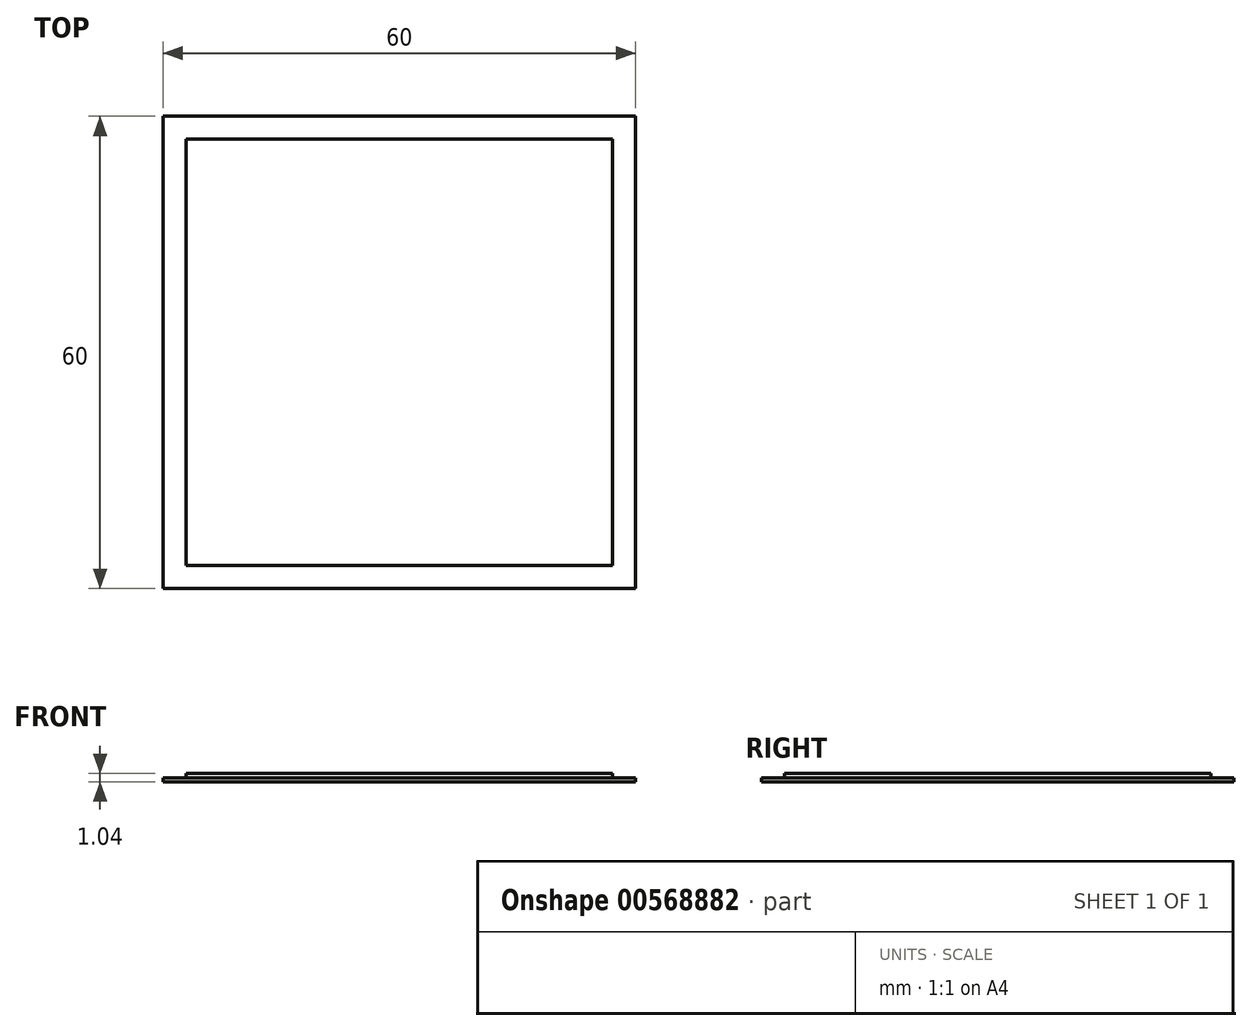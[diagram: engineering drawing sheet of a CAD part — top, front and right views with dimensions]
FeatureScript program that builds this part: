
annotation { "Feature Type Name" : "Feature", "Feature Type Description" : "" }
export const myFeature = defineFeature(function(context is Context, id is Id, definition is map)
    precondition{}
    {
        {
            var Q0;
            Q0=qCreatedBy(makeId("Top.planeOp"),FACE);
            var sketch = newSketch(context, id + "F0", { "sketchPlane" : qUnion([Q0])});
            skLineSegment(sketch, "E0.bottom", {"start": v(3, -3) * mm, "end": v(-3, -3) * mm});
            skLineSegment(sketch, "E0.top", {"start": v(3, 3) * mm, "end": v(-3, 3) * mm});
            skLineSegment(sketch, "E0.left", {"start": v(3, -3) * mm, "end": v(3, 3) * mm});
            skLineSegment(sketch, "E0.right", {"start": v(-3, -3) * mm, "end": v(-3, 3) * mm});
            skSolve(sketch);
        }
        {
            var Q0;
            Q0 = qSketchRegion(id + "F0", true);
            var Q1;
            Q1=makeQuery(id+"F0.imprint","IMPRINT",FACE,{"disambiguationData":[TD([[makeQuery(id+"F0.imprint","IMPRINT",EDGE,{"derivedFrom":sQuery(id+"F0.wireOp",EDGE,"3195768e-dd08-421b-a517-f94ed740182d")}),1.0]])]});
            var Q2;
            Q2=makeQuery(id+"F0.imprint","IMPRINT",FACE,{"disambiguationData":[TD([[makeQuery(id+"F0.imprint","IMPRINT",EDGE,{"derivedFrom":sQuery(id+"F0.wireOp",EDGE,"99365f39-84bf-4d14-bde5-4bdda7643e0d")}),1.0]])]});
            var Q3;
            Q3=makeQuery(id+"F0.imprint","IMPRINT",FACE,{"disambiguationData":[TD([[makeQuery(id+"F0.imprint","IMPRINT",EDGE,{"derivedFrom":sQuery(id+"F0.wireOp",EDGE,"a9b0deac-9651-4806-95d7-b4778e970440")}),1.0]])]});
            var Q4;
            Q4=makeQuery(id+"F0.imprint","IMPRINT",FACE,{"disambiguationData":[TD([[makeQuery(id+"F0.imprint","IMPRINT",EDGE,{"derivedFrom":sQuery(id+"F0.wireOp",EDGE,"e3f9c86c-c5da-4ea8-b7f3-f17e3de16e99")}),1.0]])]});
            var Q5;
            Q5=makeQuery(id+"F0.imprint","IMPRINT",FACE,{"disambiguationData":[TD([[makeQuery(id+"F0.imprint","IMPRINT",EDGE,{"derivedFrom":sQuery(id+"F0.wireOp",EDGE,"0799e189-6896-4580-8602-fb586a51e5e5")}),1.0]])]});
            var Q6;
            Q6=makeQuery(id+"F0.imprint","IMPRINT",FACE,{"disambiguationData":[TD([[makeQuery(id+"F0.imprint","IMPRINT",EDGE,{"derivedFrom":sQuery(id+"F0.wireOp",EDGE,"4af3724b-39f9-40e6-87d7-aee2c64644f4")}),1.0]])]});
            var Q7;
            Q7=makeQuery(id+"F0.imprint","IMPRINT",FACE,{"disambiguationData":[TD([[makeQuery(id+"F0.imprint","IMPRINT",EDGE,{"derivedFrom":sQuery(id+"F0.wireOp",EDGE,"dbd310c0-aaaf-4fef-bc50-6cb66c9705c9")}),1.0]])]});
            var Q8;
            Q8=makeQuery(id+"F0.imprint","IMPRINT",FACE,{"disambiguationData":[TD([[makeQuery(id+"F0.imprint","IMPRINT",EDGE,{"derivedFrom":sQuery(id+"F0.wireOp",EDGE,"8f1b4460-da73-453b-86da-44b5cc01f122")}),1.0]])]});
            var Q9;
            Q9=makeQuery(id+"F0.imprint","IMPRINT",FACE,{"disambiguationData":[TD([[makeQuery(id+"F0.imprint","IMPRINT",EDGE,{"derivedFrom":sQuery(id+"F0.wireOp",EDGE,"ee4c995a-49f5-4f9c-93ae-5fdf9cce8992")}),1.0]])]});
            var Q10;
            Q10=makeQuery(id+"F0.imprint","IMPRINT",FACE,{"disambiguationData":[TD([[makeQuery(id+"F0.imprint","IMPRINT",EDGE,{"derivedFrom":sQuery(id+"F0.wireOp",EDGE,"33e57519-050b-4a84-9a16-697477c51025")}),1.0]])]});
            var Q11;
            Q11=makeQuery(id+"F0.imprint","IMPRINT",FACE,{"disambiguationData":[TD([[makeQuery(id+"F0.imprint","IMPRINT",EDGE,{"derivedFrom":sQuery(id+"F0.wireOp",EDGE,"be71d767-2dd2-4a31-b7f5-905de18da15a")}),1.0]])]});
            var Q12;
            Q12=makeQuery(id+"F0.imprint","IMPRINT",FACE,{"disambiguationData":[TD([[makeQuery(id+"F0.imprint","IMPRINT",EDGE,{"derivedFrom":sQuery(id+"F0.wireOp",EDGE,"703af41d-b022-42bc-8811-11c2ffb21b86")}),1.0]])]});
            var Q13;
            Q13=makeQuery(id+"F0.imprint","IMPRINT",FACE,{"disambiguationData":[TD([[makeQuery(id+"F0.imprint","IMPRINT",EDGE,{"derivedFrom":sQuery(id+"F0.wireOp",EDGE,"1cf93dc1-08e6-4c8b-baeb-da0c2a0960a5")}),1.0]])]});
            var Q14;
            Q14=makeQuery(id+"F0.imprint","IMPRINT",FACE,{"disambiguationData":[TD([[makeQuery(id+"F0.imprint","IMPRINT",EDGE,{"derivedFrom":sQuery(id+"F0.wireOp",EDGE,"951dbc04-e7e7-431c-b509-9a55957cb495")}),1.0]])]});
            var Q15;
            Q15=makeQuery(id+"F0.imprint","IMPRINT",FACE,{"disambiguationData":[TD([[makeQuery(id+"F0.imprint","IMPRINT",EDGE,{"derivedFrom":sQuery(id+"F0.wireOp",EDGE,"82349083-6ecb-4763-8a3f-b2f68fb64006")}),1.0]])]});
            var Q16;
            Q16=makeQuery(id+"F0.imprint","IMPRINT",FACE,{"disambiguationData":[TD([[makeQuery(id+"F0.imprint","IMPRINT",EDGE,{"derivedFrom":sQuery(id+"F0.wireOp",EDGE,"40c397c2-dbba-4eb3-9c68-bade8745c26b")}),1.0]])]});
            var Q17;
            Q17=makeQuery(id+"F0.imprint","IMPRINT",FACE,{"disambiguationData":[TD([[makeQuery(id+"F0.imprint","IMPRINT",EDGE,{"derivedFrom":sQuery(id+"F0.wireOp",EDGE,"1296daf1-cca8-41f8-a248-591c8d4edc7d")}),1.0]])]});
            var Q18;
            Q18=makeQuery(id+"F0.imprint","IMPRINT",FACE,{"disambiguationData":[TD([[makeQuery(id+"F0.imprint","IMPRINT",EDGE,{"derivedFrom":sQuery(id+"F0.wireOp",EDGE,"f8264f38-76e0-493a-aef4-62b8dbf1ef44")}),-1.0]])]});
            var Q19;
            Q19=makeQuery(id+"F0.imprint","IMPRINT",FACE,{"disambiguationData":[TD([[makeQuery(id+"F0.imprint","IMPRINT",EDGE,{"derivedFrom":sQuery(id+"F0.wireOp",EDGE,"834d6977-e806-4c23-b116-ce7edfcfaa7b")}),-1.0]])]});
            var Q20;
            Q20=makeQuery(id+"F0.imprint","IMPRINT",FACE,{"disambiguationData":[TD([[makeQuery(id+"F0.imprint","IMPRINT",EDGE,{"derivedFrom":sQuery(id+"F0.wireOp",EDGE,"abdaa881-ba7a-4edb-bdbc-db0cbd3f6efc")}),-1.0]])]});
            var Q21;
            Q21=makeQuery(id+"F0.imprint","IMPRINT",FACE,{"disambiguationData":[TD([[makeQuery(id+"F0.imprint","IMPRINT",EDGE,{"derivedFrom":sQuery(id+"F0.wireOp",EDGE,"da8af10c-896a-4133-b8ce-ebc45f5c24c5")}),-1.0]])]});
            var Q22;
            Q22=makeQuery(id+"F0.imprint","IMPRINT",FACE,{"disambiguationData":[TD([[makeQuery(id+"F0.imprint","IMPRINT",EDGE,{"derivedFrom":sQuery(id+"F0.wireOp",EDGE,"85b238a3-1cd6-4965-8cfa-3052cf196f0d")}),1.0]])]});
            var Q23;
            Q23=makeQuery(id+"F0.imprint","IMPRINT",FACE,{"disambiguationData":[TD([[makeQuery(id+"F0.imprint","IMPRINT",EDGE,{"derivedFrom":sQuery(id+"F0.wireOp",EDGE,"65e1c758-dbae-4b52-ac89-c4899e5be1b6")}),1.0]])]});
            extrude(context, id + "F1", {"entities" : qUnion([Q0, Q1, Q2, Q3, Q4, Q5, Q6, Q7, Q8, Q9, Q10, Q11, Q12, Q13, Q14, Q15, Q16, Q17, Q18, Q19, Q20, Q21, Q22, Q23]), "depth" : 0.06 * mm, "offsetDistance" : 25 * mm});
        }
        {
            var Q0;
            Q0=makeQuery(id+"F1.opExtrude","SWEPT_BODY",BODY,{"disambiguationData":[OSD([sQuery(id+"F0.wireOp",EDGE,"E0.bottom"),sQuery(id+"F0.wireOp",EDGE,"E0.top"),sQuery(id+"F0.wireOp",EDGE,"E0.left"),sQuery(id+"F0.wireOp",EDGE,"E0.right"),sQuery(id+"F0.wireOp",EDGE,"3ec7afe0-a1e0-457c-be4a-088452004a96"),sQuery(id+"F0.wireOp",EDGE,"d83f218b-7086-4efd-8b13-d209db19827c"),sQuery(id+"F0.wireOp",EDGE,"02d8bd81-b223-4a02-9b2f-538ae8beb5a6"),sQuery(id+"F0.wireOp",EDGE,"2d902582-cd20-4641-8568-96b7fb684a02"),sQuery(id+"F0.wireOp",EDGE,"f5096a21-a806-46d9-b6c2-ae8de96a788b"),sQuery(id+"F0.wireOp",EDGE,"3b47cd1d-8fba-4731-8d0e-cda14d99b06e"),sQuery(id+"F0.wireOp",EDGE,"41564daa-fe03-4dbd-9e56-aa0510e19988"),sQuery(id+"F0.wireOp",EDGE,"02388e9d-f7fc-4dad-9147-57d1375461ec"),sQuery(id+"F0.wireOp",EDGE,"22264fa0-5d3e-4774-86a0-50946ccf6ead"),sQuery(id+"F0.wireOp",EDGE,"a467128b-4a78-4aa8-9340-e2e247e980d2"),sQuery(id+"F0.wireOp",EDGE,"1619cbc9-05f0-4f5a-8f65-62f3c9434277"),sQuery(id+"F0.wireOp",EDGE,"99e10741-56a3-4363-82b4-1b7282e7ca4c"),sQuery(id+"F0.wireOp",EDGE,"24693340-a1d5-4308-b41e-ebabe64e6a8c"),sQuery(id+"F0.wireOp",EDGE,"64b93bc5-bd2d-41f4-a006-fbb3c3e2de2e"),sQuery(id+"F0.wireOp",EDGE,"55426dc8-b2e5-4f94-be62-9a8d58c9ab38"),sQuery(id+"F0.wireOp",EDGE,"5bce8405-4400-4a37-8856-f7f68e24ea4c"),sQuery(id+"F0.wireOp",EDGE,"c21bd593-22bc-4b69-8e4e-1fb222cef98b"),sQuery(id+"F0.wireOp",EDGE,"f8c3e9e9-656d-4477-9170-02d9ece8e834"),sQuery(id+"F0.wireOp",EDGE,"8a779292-eed6-45a9-b757-0a415a321d37"),sQuery(id+"F0.wireOp",EDGE,"5f832a96-d78e-4e74-b481-aab9e5c15b8e"),sQuery(id+"F0.wireOp",EDGE,"430f9e32-9bfc-4471-b983-62e587525792"),sQuery(id+"F0.wireOp",EDGE,"9e28f7ca-141b-4c07-b7ad-4c5ca4b71de8"),sQuery(id+"F0.wireOp",EDGE,"7ab17df3-aba0-41db-9353-0b5ccab53e5f"),sQuery(id+"F0.wireOp",EDGE,"e171d48b-26fe-4f5a-a888-7f954c3a5218"),sQuery(id+"F0.wireOp",EDGE,"e79f6706-141e-4c0d-adc8-7167a5aa39dc"),sQuery(id+"F0.wireOp",EDGE,"c8e1bd4d-aee9-41e8-ade3-5be9cbb654e8"),sQuery(id+"F0.wireOp",EDGE,"47d54f73-4b4e-483b-a749-b05e58b45576"),sQuery(id+"F0.wireOp",EDGE,"7973314d-2740-4cf3-b868-1b8a999ba722"),sQuery(id+"F0.wireOp",EDGE,"720fcdf6-7b9d-4216-8e72-eb40a41dce0a"),sQuery(id+"F0.wireOp",EDGE,"d29978c5-a1be-4d4b-8944-da0213377966"),sQuery(id+"F0.wireOp",EDGE,"e5daffcd-b5ce-4dea-ac11-20f20ff523b4"),sQuery(id+"F0.wireOp",EDGE,"50641089-9504-40b9-8477-96adc3d40a89"),sQuery(id+"F0.wireOp",EDGE,"6d270dd2-b7c0-458e-a9ee-65726ff07b0c"),sQuery(id+"F0.wireOp",EDGE,"b3e48804-5e06-4876-8223-ffe42bf3636a"),sQuery(id+"F0.wireOp",EDGE,"63cc2df1-c457-4d14-b5f3-d92c72be0608"),sQuery(id+"F0.wireOp",EDGE,"811def09-c990-4daf-ba8c-b148da244ebc"),sQuery(id+"F0.wireOp",EDGE,"4d1e2a3c-fd62-4d4c-bcf6-9f666ab0c452"),sQuery(id+"F0.wireOp",EDGE,"81fce658-763d-4a5d-a611-0a742473717a"),sQuery(id+"F0.wireOp",EDGE,"f822a7c1-ac77-462a-b5c0-4338f93c980d"),sQuery(id+"F0.wireOp",EDGE,"f1bb49a8-6e90-4657-99b0-fe3ee6e9b850"),sQuery(id+"F0.wireOp",EDGE,"62310ddd-0304-494f-90b3-e6686b61077f"),sQuery(id+"F0.wireOp",EDGE,"c2033112-2bf2-40f2-861c-00d87bee8627"),sQuery(id+"F0.wireOp",EDGE,"14c75d5e-7332-4c27-bd92-261d4fd848ba"),sQuery(id+"F0.wireOp",EDGE,"22950e56-f2bd-479b-ad15-ca8860f234eb"),sQuery(id+"F0.wireOp",EDGE,"0c1f7b48-368b-462f-880e-93a51e1aa555"),sQuery(id+"F0.wireOp",EDGE,"b5a827ad-50b1-4835-9a05-472a480554c8"),sQuery(id+"F0.wireOp",EDGE,"44def7af-5edd-4bc8-b590-da631150d928"),sQuery(id+"F0.wireOp",EDGE,"5b539bd8-9961-45a0-92ed-a386129d0a0b"),sQuery(id+"F0.wireOp",EDGE,"e7b18de2-00d5-44c6-b284-184d2c0b6658"),sQuery(id+"F0.wireOp",EDGE,"d9bf9977-81ab-4193-b2fa-4848e88f6ea1"),sQuery(id+"F0.wireOp",EDGE,"5ebeac3d-4b27-4cb7-bf5d-219251f9516b"),sQuery(id+"F0.wireOp",EDGE,"a416a0db-305d-478f-8e7c-7a8594db7948"),sQuery(id+"F0.wireOp",EDGE,"5670b267-cfff-421d-b539-6a539cfda789"),sQuery(id+"F0.wireOp",EDGE,"3dac470b-4319-4a66-ae29-b8d3f215b9bd"),sQuery(id+"F0.wireOp",EDGE,"03b27164-48bf-4732-9087-733abdd1034d"),sQuery(id+"F0.wireOp",EDGE,"8120ee63-c910-4b66-ac7d-0f760dbf99e2"),sQuery(id+"F0.wireOp",EDGE,"c9e787c0-baf7-46a9-b42b-2670cd472db3"),sQuery(id+"F0.wireOp",EDGE,"851d0d47-70d4-462b-aa0f-03065de4ac0c"),sQuery(id+"F0.wireOp",EDGE,"e77e26e9-0bc8-48ac-b61c-24ad1caf3c9c"),sQuery(id+"F0.wireOp",EDGE,"d6e28216-d606-4f2b-8d32-bb6ccec41566"),sQuery(id+"F0.wireOp",EDGE,"8c67bd25-36d2-4afe-bd64-c387e52d00c2"),sQuery(id+"F0.wireOp",EDGE,"e4aac0d1-a521-48c7-9d6c-724ae50099b9"),sQuery(id+"F0.wireOp",EDGE,"61536177-4917-47db-bde2-8d2a4f733d81"),sQuery(id+"F0.wireOp",EDGE,"47ab3f07-b9b0-4f7d-aaf9-d7cfa683d4aa"),sQuery(id+"F0.wireOp",EDGE,"72710534-632b-4c55-849d-ec722133dbc1"),sQuery(id+"F0.wireOp",EDGE,"5e43d561-e149-44a2-9fca-b4b008a3a7d6"),sQuery(id+"F0.wireOp",EDGE,"9279be7f-0be9-4663-98e7-e996f2be473d"),sQuery(id+"F0.wireOp",EDGE,"c44d038a-da18-41ec-8afa-1d1866d1f861"),sQuery(id+"F0.wireOp",EDGE,"e3798a42-469f-46b9-9ab3-bacfc8b42f00"),sQuery(id+"F0.wireOp",EDGE,"f034fc37-7e18-494d-834f-c8e07136fe97"),sQuery(id+"F0.wireOp",EDGE,"ffba7b79-0caf-4550-9ef0-48fd2c2eedc0"),sQuery(id+"F0.wireOp",EDGE,"f7a3de90-2f3c-43dc-9883-e84d532b549c"),sQuery(id+"F0.wireOp",EDGE,"c750c932-4bbb-417d-bdea-0f72397a7019"),sQuery(id+"F0.wireOp",EDGE,"a3412e4e-3ed4-4017-94ce-3c13780d5bf9"),sQuery(id+"F0.wireOp",EDGE,"f6e69c40-12d3-4752-8b7f-c0431ab5c846"),sQuery(id+"F0.wireOp",EDGE,"767176a0-43e3-4645-a59e-1272894fbf7a"),sQuery(id+"F0.wireOp",EDGE,"6f2bbe3a-c317-49b8-94a2-a87eb011ea02"),sQuery(id+"F0.wireOp",EDGE,"a1520ac8-22ba-49e5-93e5-20ceff7b8af7"),sQuery(id+"F0.wireOp",EDGE,"cb4930a2-9a3a-4684-ab62-77c10cece2a2"),sQuery(id+"F0.wireOp",EDGE,"20b6dfe0-11c6-493f-8d24-8f66077ccf5c"),sQuery(id+"F0.wireOp",EDGE,"2ca8a1b8-9df9-411f-8d1c-6445228a5ca8"),sQuery(id+"F0.wireOp",EDGE,"699309a4-edb1-411f-8ef3-7794c42be602"),sQuery(id+"F0.wireOp",EDGE,"bd74286a-29d0-4114-a072-0032613366e6"),sQuery(id+"F0.wireOp",EDGE,"fc658b50-a5ca-4d86-a88e-b76cf9467b0b"),sQuery(id+"F0.wireOp",EDGE,"27fdd899-d6b1-4d30-8442-3c03dd78eba2"),sQuery(id+"F0.wireOp",EDGE,"440f6f4a-16b8-4354-8233-1d1744525dae"),sQuery(id+"F0.wireOp",EDGE,"3d98288c-f389-4f90-9d39-60cb79a00bb8"),sQuery(id+"F0.wireOp",EDGE,"f79bcbc1-5df4-4b7b-80fa-43563f779b76"),sQuery(id+"F0.wireOp",EDGE,"1051ae6e-5939-4fe6-8811-fbc80e0b9638"),sQuery(id+"F0.wireOp",EDGE,"76698742-e0db-49a3-82d9-61ed44e431b8"),sQuery(id+"F0.wireOp",EDGE,"ba61a141-cac1-4778-9c9e-74bcd335542e"),sQuery(id+"F0.wireOp",EDGE,"81f51e81-3098-4b38-81a7-bde5e4d849b4"),sQuery(id+"F0.wireOp",EDGE,"c7cc50c0-9e9f-467a-9f0c-185cd03e4846"),sQuery(id+"F0.wireOp",EDGE,"3275c11a-791a-4694-a09e-df3df0d70a3d"),sQuery(id+"F0.wireOp",EDGE,"bc3e4385-77d7-4447-8bec-42d880316bfd"),sQuery(id+"F0.wireOp",EDGE,"ea27d34e-d2f1-4b3e-92c9-6e89909bea16"),sQuery(id+"F0.wireOp",EDGE,"379d4164-5f7a-4c05-baa5-cc58e4694ce7"),sQuery(id+"F0.wireOp",EDGE,"1062bfd7-c4fc-4b28-b988-7fe4492de22f"),sQuery(id+"F0.wireOp",EDGE,"fc213567-08de-486d-b4ca-ff95bb5b6401"),sQuery(id+"F0.wireOp",EDGE,"a14c394f-738c-49f1-a45f-159cd0637914"),sQuery(id+"F0.wireOp",EDGE,"166781b6-f08b-48b1-bac9-12c9ea3421ab"),sQuery(id+"F0.wireOp",EDGE,"35f9fbb9-e8a9-44e7-8893-e82d580ff6ca"),sQuery(id+"F0.wireOp",EDGE,"d55b8e85-21c7-4f06-b75f-d413d399493a"),sQuery(id+"F0.wireOp",EDGE,"f78b1f4a-3af2-4aca-b1f1-9c95252bd1fc"),sQuery(id+"F0.wireOp",EDGE,"8ff1015e-a657-4219-b192-62bd4060579d"),sQuery(id+"F0.wireOp",EDGE,"712e7e8e-a0b3-4a78-b3cf-5035268c3b1b"),sQuery(id+"F0.wireOp",EDGE,"dd7306b4-5a59-4d03-b176-b2ecc48ed0c9"),sQuery(id+"F0.wireOp",EDGE,"a4f7c66e-2dea-453d-a349-4ee5712a776d"),sQuery(id+"F0.wireOp",EDGE,"eee453a0-aeb0-49ac-a5a0-f2e9f7f4152a"),sQuery(id+"F0.wireOp",EDGE,"b8c53693-8c12-4e66-8b60-6595c828f9ef"),sQuery(id+"F0.wireOp",EDGE,"ba798e71-e747-4192-bb8a-8c61b35e6316"),sQuery(id+"F0.wireOp",EDGE,"e1604eea-9b7d-491b-83e4-51499261206a"),sQuery(id+"F0.wireOp",EDGE,"bc5efcf9-bb2f-4e29-a1ca-58298c4f8a7b"),sQuery(id+"F0.wireOp",EDGE,"6319af28-edc9-4555-9ad3-ebef588b88ae"),sQuery(id+"F0.wireOp",EDGE,"2e15575d-92d4-45b8-aba9-d4b5887d4759"),sQuery(id+"F0.wireOp",EDGE,"593a8dbb-b7b4-4bd3-9e56-5ac97cc9a1ec"),sQuery(id+"F0.wireOp",EDGE,"02380fbd-832a-4dc9-aae5-dbf10ebaaf3d"),sQuery(id+"F0.wireOp",EDGE,"13981ab7-9961-4e34-9086-dceaa1c7b3be"),sQuery(id+"F0.wireOp",EDGE,"3a046d59-f46e-467a-9278-2a68960cf58b"),sQuery(id+"F0.wireOp",EDGE,"a75f2866-233f-4df0-b6f9-14dd6b91b060"),sQuery(id+"F0.wireOp",EDGE,"f2732e12-788a-45ca-9c56-273da7a29a0e"),sQuery(id+"F0.wireOp",EDGE,"8ee60f07-1099-4ca2-9ebe-5424af49e3b5"),sQuery(id+"F0.wireOp",EDGE,"4f58ddd7-5aa5-438a-b942-bca2248868eb"),sQuery(id+"F0.wireOp",EDGE,"ea4bc371-bac6-43d1-8ec8-77b3c77d1d08"),sQuery(id+"F0.wireOp",EDGE,"fabef4ac-eedc-4238-adcb-865e221dc712"),sQuery(id+"F0.wireOp",EDGE,"c34c20a1-9834-4408-bf79-1be559bfa9ba"),sQuery(id+"F0.wireOp",EDGE,"5e8330d4-b02b-4a67-8497-a16df57a01fc"),sQuery(id+"F0.wireOp",EDGE,"1ce77aba-b302-47d2-8b68-c2e856514517"),sQuery(id+"F0.wireOp",EDGE,"834b12ab-1ad9-49dd-b164-8d70879f156f"),sQuery(id+"F0.wireOp",EDGE,"bed03741-100b-4911-8924-3d714ec53786"),sQuery(id+"F0.wireOp",EDGE,"f5ef7e46-89d9-4f7d-8693-a5c8aed4e8d6"),sQuery(id+"F0.wireOp",EDGE,"3f11fecd-cc23-4907-9c92-c85356b89d33"),sQuery(id+"F0.wireOp",EDGE,"5e1d7c4c-f824-4253-95c8-758a53e5f7d8"),sQuery(id+"F0.wireOp",EDGE,"81e188b5-2422-419b-9d61-c4ff843a2b7d"),sQuery(id+"F0.wireOp",EDGE,"e9228d95-9eeb-42dc-909a-163fbb938afe"),sQuery(id+"F0.wireOp",EDGE,"959069a5-4158-4b4e-aaea-50d8de0d1250"),sQuery(id+"F0.wireOp",EDGE,"50333e4b-2514-429b-8c4f-ca88dfc82600"),sQuery(id+"F0.wireOp",EDGE,"075de889-d11b-4e8b-9c31-040acac3b58d"),sQuery(id+"F0.wireOp",EDGE,"c7c70318-40be-436f-b5fd-08fe0706d55e"),sQuery(id+"F0.wireOp",EDGE,"5723ddac-3b46-4be1-afdb-4c7638558a6f"),sQuery(id+"F0.wireOp",EDGE,"d590f57a-681e-43fc-ad37-4c356b537c3a"),sQuery(id+"F0.wireOp",EDGE,"f6af2cb9-de3d-4e7c-866f-a3e7c472d7b8"),sQuery(id+"F0.wireOp",EDGE,"b6c00460-730a-4222-a33a-3643a2ef3fe4"),sQuery(id+"F0.wireOp",EDGE,"827ff635-27c5-4321-831d-4920dab6c213"),sQuery(id+"F0.wireOp",EDGE,"38421385-35fb-40d3-bf68-990b4a57970c"),sQuery(id+"F0.wireOp",EDGE,"18ad6ecc-b386-4713-bde1-9b9bd5a2318a"),sQuery(id+"F0.wireOp",EDGE,"0711714c-1d40-418f-8cd7-8681d9630629"),sQuery(id+"F0.wireOp",EDGE,"98796be2-b74d-4e80-bb13-dd88d4f5ec73"),sQuery(id+"F0.wireOp",EDGE,"88c95ccb-a92a-4622-ad8b-6e7e745f93e2"),sQuery(id+"F0.wireOp",EDGE,"e3605e1b-24de-43cc-8fe1-493b685f07a9"),sQuery(id+"F0.wireOp",EDGE,"f781a5ef-2e9d-4487-aa95-33630d70acaa"),sQuery(id+"F0.wireOp",EDGE,"fd6c0f24-dea2-4d7b-a979-02eed4e90b37"),sQuery(id+"F0.wireOp",EDGE,"05fbe2cf-c617-47ae-a1cf-4fe9e66abefc"),sQuery(id+"F0.wireOp",EDGE,"7a299a4e-a918-4890-99c3-7a67ee3f4166"),sQuery(id+"F0.wireOp",EDGE,"0a5a90e0-eb3c-4e0d-ab2a-89f6e7f68dfe"),sQuery(id+"F0.wireOp",EDGE,"70afa412-88dc-4f5e-a859-925588698aba"),sQuery(id+"F0.wireOp",EDGE,"2913be52-9a0c-4146-a4c9-76e64dcde4e6"),sQuery(id+"F0.wireOp",EDGE,"d0417cf6-5bfb-45b9-a084-899a6a988cf6"),sQuery(id+"F0.wireOp",EDGE,"2538756b-0ef2-41bd-b8c8-6d272a99fe31"),sQuery(id+"F0.wireOp",EDGE,"0198ab2a-8068-43de-bfce-0b2b70d5decd"),sQuery(id+"F0.wireOp",EDGE,"31aaf3f3-bc7b-4674-810a-75f22c7ab986"),sQuery(id+"F0.wireOp",EDGE,"8fe21c58-7b24-4e10-9c93-26b82d9e6d21"),sQuery(id+"F0.wireOp",EDGE,"3a426131-fa73-4696-ac6e-bdb9b449d5ce"),sQuery(id+"F0.wireOp",EDGE,"03eeec74-ae2a-46bb-9ee7-4ceb3502b2a6"),sQuery(id+"F0.wireOp",EDGE,"618a0795-a880-4c47-997d-98bac031e887"),sQuery(id+"F0.wireOp",EDGE,"3ad50032-8811-49f1-96ac-81b191064997"),sQuery(id+"F0.wireOp",EDGE,"496fcda9-6dd8-4934-baf7-14d3f409cee7"),sQuery(id+"F0.wireOp",EDGE,"692feb32-5741-4b3b-9193-cd2f3880199d"),sQuery(id+"F0.wireOp",EDGE,"859ace9e-6eac-4f18-a080-abca9f5452dc"),sQuery(id+"F0.wireOp",EDGE,"0a587952-0d6a-4492-addb-1eb97c7d4114"),sQuery(id+"F0.wireOp",EDGE,"c014b403-4438-4a75-9310-698630d0f26c"),sQuery(id+"F0.wireOp",EDGE,"e4c50579-3f17-4124-8f98-613c4078bb63"),sQuery(id+"F0.wireOp",EDGE,"510b368e-4dd2-421a-a9d0-86b946da967d"),sQuery(id+"F0.wireOp",EDGE,"651565fc-69bc-4961-b2b7-ef0527e41ecc"),sQuery(id+"F0.wireOp",EDGE,"23e80a2d-6976-4a1c-a60a-a5e4b68532fd"),sQuery(id+"F0.wireOp",EDGE,"a6ad6e05-5a2c-4e61-9f80-cdbf757a204d"),sQuery(id+"F0.wireOp",EDGE,"3e5aa7f2-2fc2-4aac-a952-e5bcad74a832"),sQuery(id+"F0.wireOp",EDGE,"df52b165-db6a-4f60-bffd-e9240c9c772f"),sQuery(id+"F0.wireOp",EDGE,"c3733b21-a760-48e9-a77a-88576df8cad6"),sQuery(id+"F0.wireOp",EDGE,"ec350596-bf51-4731-b449-2f407bf6303f"),sQuery(id+"F0.wireOp",EDGE,"70cc3cca-0fee-441a-b4d7-96843ff51759"),sQuery(id+"F0.wireOp",EDGE,"c3d1a2ba-bd2a-49b8-bea6-459ef0d2576b"),sQuery(id+"F0.wireOp",EDGE,"23c7a7ae-7321-47e6-a06e-f4653b5178e5"),sQuery(id+"F0.wireOp",EDGE,"e487ad68-183a-4f24-9bd6-de54da96e15a"),sQuery(id+"F0.wireOp",EDGE,"5fa12f74-eda4-4c68-af2c-a4252f408fd3"),sQuery(id+"F0.wireOp",EDGE,"155640c1-ebf2-4dfb-8ef7-75cccd395f21"),sQuery(id+"F0.wireOp",EDGE,"e6ac35a8-d854-4e89-9e33-bea3e269d9a9"),sQuery(id+"F0.wireOp",EDGE,"cb9e2b8c-6de3-4701-937a-1e5628a11478"),sQuery(id+"F0.wireOp",EDGE,"e6808a8c-d175-4686-93c2-d832b162152e"),sQuery(id+"F0.wireOp",EDGE,"356ed25e-81ff-40a8-9200-19a22ad69f1a"),sQuery(id+"F0.wireOp",EDGE,"3b75a134-16d4-4a6b-bad6-df067ae33d35"),sQuery(id+"F0.wireOp",EDGE,"6826a5ab-7ce6-4ac5-b70b-e668ad123194"),sQuery(id+"F0.wireOp",EDGE,"4d99424e-51b7-426f-8c94-c72b14d11e31"),sQuery(id+"F0.wireOp",EDGE,"d860b5f2-e0dd-40a9-8acd-6e3a757f8406"),sQuery(id+"F0.wireOp",EDGE,"39f266b8-2d6b-452a-a185-b1af436a92a6"),sQuery(id+"F0.wireOp",EDGE,"31866575-b77f-4788-8f5d-84bcd0349519"),sQuery(id+"F0.wireOp",EDGE,"5d551245-3a28-4603-9d08-9c0ccb735e6d"),sQuery(id+"F0.wireOp",EDGE,"9b0dd94d-059d-4297-8c38-4640a45fed80"),sQuery(id+"F0.wireOp",EDGE,"2920166d-42de-4cff-aff8-3d29da85a708"),sQuery(id+"F0.wireOp",EDGE,"38e33062-00b2-423a-9adf-0dbdc295fc21"),sQuery(id+"F0.wireOp",EDGE,"817ef9cf-887c-4d38-8025-1a9fee5b0c85"),sQuery(id+"F0.wireOp",EDGE,"4d48468a-d922-400c-add1-5cda9d138ebd"),sQuery(id+"F0.wireOp",EDGE,"ff677f1f-a331-463e-ad12-0f0b2d816477"),sQuery(id+"F0.wireOp",EDGE,"0fe15785-9fea-410f-ad1f-32f88843b595"),sQuery(id+"F0.wireOp",EDGE,"8d09f6c3-07f2-4eb2-aa7f-694363c195a6"),sQuery(id+"F0.wireOp",EDGE,"ec3514e2-3f68-4b88-aecf-a0ee5f06dbea"),sQuery(id+"F0.wireOp",EDGE,"19cb8244-8a3e-4d20-b4f2-7ecd0c712cb2"),sQuery(id+"F0.wireOp",EDGE,"d1091000-42f3-4bcd-9e7a-0692b83df9ec"),sQuery(id+"F0.wireOp",EDGE,"3b397f38-0c49-45a4-a347-98b3a47d70fb"),sQuery(id+"F0.wireOp",EDGE,"d3a4285d-9d01-49b4-b990-b3f73cc7f7e6"),sQuery(id+"F0.wireOp",EDGE,"eed04ee1-c9da-4961-a22d-363b71bae0c2"),sQuery(id+"F0.wireOp",EDGE,"c6171e94-0cba-4356-a26f-247245c8c466"),sQuery(id+"F0.wireOp",EDGE,"6c7643e3-9710-4967-95d2-9ba02bf7ea3e"),sQuery(id+"F0.wireOp",EDGE,"a5f0d80a-626b-4f41-820c-24ba71a7cde6"),sQuery(id+"F0.wireOp",EDGE,"275f012e-7d73-4b9e-b8af-7366cfb6fb08"),sQuery(id+"F0.wireOp",EDGE,"dda7959b-0520-412b-a0df-24aa169fb8fa"),sQuery(id+"F0.wireOp",EDGE,"bd6a2b4a-0797-431f-b7b7-b4e64eae0bb1"),sQuery(id+"F0.wireOp",EDGE,"a1529b2f-f819-429b-97a1-27107fec5de5"),sQuery(id+"F0.wireOp",EDGE,"56fb065c-a381-4615-8b32-7e704d515f56"),sQuery(id+"F0.wireOp",EDGE,"3a80e261-097b-466e-b523-ebbeb2b08257"),sQuery(id+"F0.wireOp",EDGE,"aad8cfd8-81ef-4e44-8af1-503e01a83ad9"),sQuery(id+"F0.wireOp",EDGE,"384a4556-9810-4801-9165-3d7c89c49f93"),sQuery(id+"F0.wireOp",EDGE,"e80a3cc5-1d65-4b1f-a697-de30cccef087"),sQuery(id+"F0.wireOp",EDGE,"beb5745a-8d9d-4c3f-9ca8-9fae599df75e"),sQuery(id+"F0.wireOp",EDGE,"e636cc4a-5226-4be0-a810-a5596ba0a380"),sQuery(id+"F0.wireOp",EDGE,"11aa103c-fcc8-4654-b695-160f80f03844"),sQuery(id+"F0.wireOp",EDGE,"13544508-c267-4dfe-b823-0fcb28622b0a"),sQuery(id+"F0.wireOp",EDGE,"32665112-ab27-4cdc-b08d-6fbfa26e143d"),sQuery(id+"F0.wireOp",EDGE,"64d7f8b8-0fad-4658-a91b-32d9fbade6e0"),sQuery(id+"F0.wireOp",EDGE,"693aa929-2a0d-4d07-b657-d91b5e5a50a4"),sQuery(id+"F0.wireOp",EDGE,"562a9f06-3999-4e31-92ba-a9bce39a5457"),sQuery(id+"F0.wireOp",EDGE,"3550bb31-bca9-4bce-b05e-749f01d8052d"),sQuery(id+"F0.wireOp",EDGE,"bbf2bd7e-b04a-49ad-87d0-94be879a1fd7"),sQuery(id+"F0.wireOp",EDGE,"1fad1780-c111-45d6-814f-8d3daf33c57c"),sQuery(id+"F0.wireOp",EDGE,"46bed204-b29f-48ce-927f-8664db11d61a"),sQuery(id+"F0.wireOp",EDGE,"f0a3a87c-a356-4ed7-9ea9-3fe54c8eb788"),sQuery(id+"F0.wireOp",EDGE,"488fb58e-355f-4e3c-b1e7-120df6e007f1"),sQuery(id+"F0.wireOp",EDGE,"057317ff-4fa0-403f-9dcc-5dd07fa112e6"),sQuery(id+"F0.wireOp",EDGE,"776f4298-1da3-4d88-ad34-446ef64a6436"),sQuery(id+"F0.wireOp",EDGE,"05d2f769-4c8d-45ba-a53f-3ee7aa0143e9"),sQuery(id+"F0.wireOp",EDGE,"3acd6a5d-3e6a-44c9-add7-099d0dc45fd1"),sQuery(id+"F0.wireOp",EDGE,"99ef3a0c-bd7a-43b8-874e-5091dcbb12c6"),sQuery(id+"F0.wireOp",EDGE,"a745c91b-db9b-4d60-9eba-4c8d32b1ce48"),sQuery(id+"F0.wireOp",EDGE,"ae27dad9-0eac-4b26-995c-815bc9562704"),sQuery(id+"F0.wireOp",EDGE,"b1f83ba6-ca34-49e5-be1d-05832cf887cd"),sQuery(id+"F0.wireOp",EDGE,"8d0cbd76-b6bd-4cb3-a90e-8176a7b89b0b"),sQuery(id+"F0.wireOp",EDGE,"e28f3772-e90c-4ccd-a8f7-2999747c42b9"),sQuery(id+"F0.wireOp",EDGE,"d087fa0c-7451-4ade-9ee1-dc5deba4127e"),sQuery(id+"F0.wireOp",EDGE,"305cecbe-32df-4af8-9aa8-eb6e0cbefc33"),sQuery(id+"F0.wireOp",EDGE,"b276f448-4e9e-4b86-8792-3961f9ade319"),sQuery(id+"F0.wireOp",EDGE,"adf8b33b-826a-4871-b007-8920910c91b7"),sQuery(id+"F0.wireOp",EDGE,"dc45c407-1dac-4814-b0fc-ab15237525e3"),sQuery(id+"F0.wireOp",EDGE,"89c15a6f-255b-4596-a352-01cb142e8ea3"),sQuery(id+"F0.wireOp",EDGE,"891983f6-cd49-4685-b1c2-6261785afe29"),sQuery(id+"F0.wireOp",EDGE,"195d7b5e-cf70-4873-a130-775555191c23"),sQuery(id+"F0.wireOp",EDGE,"161664fa-06e0-4b53-aa7c-47aebda18fc0"),sQuery(id+"F0.wireOp",EDGE,"13462a86-41b2-4154-bb45-709530ddebf9"),sQuery(id+"F0.wireOp",EDGE,"1048e858-88a8-4d62-b03b-009175f937ff"),sQuery(id+"F0.wireOp",EDGE,"88706604-e75d-43fd-bb66-8c5ebd036529"),sQuery(id+"F0.wireOp",EDGE,"6223e2d5-1c3d-4484-9c8a-7c924faae836"),sQuery(id+"F0.wireOp",EDGE,"3f74fce0-9d09-47ec-b53f-1c2d4db3a1ab"),sQuery(id+"F0.wireOp",EDGE,"ddd09eff-a1ba-477a-987a-56e31009e4af"),sQuery(id+"F0.wireOp",EDGE,"6edb5fd7-54d7-42ad-92ee-4fd85836db77"),sQuery(id+"F0.wireOp",EDGE,"bc6cd693-f8fa-459a-9074-b617ec0104da"),sQuery(id+"F0.wireOp",EDGE,"132fc3af-a9a2-4640-87b1-e560ac0033a1"),sQuery(id+"F0.wireOp",EDGE,"508947bb-8de4-4d64-b81e-b9e2ca31af85"),sQuery(id+"F0.wireOp",EDGE,"263ae8a8-90c7-498b-adf2-94af4d08f381"),sQuery(id+"F0.wireOp",EDGE,"3c3fdada-33fa-4300-959f-1652c7e04f6f"),sQuery(id+"F0.wireOp",EDGE,"5a2aeb15-d6ef-4279-a2f0-f14d4b96b63e"),sQuery(id+"F0.wireOp",EDGE,"148bec1a-b59e-4291-9602-0e668bb3d098"),sQuery(id+"F0.wireOp",EDGE,"a1b19cf1-cf94-4a44-bc22-0c00d1b35e40"),sQuery(id+"F0.wireOp",EDGE,"b99aee4d-3f0d-48ee-b4ff-0ebc7f0d6d8a"),sQuery(id+"F0.wireOp",EDGE,"ecf27dbc-66c4-407c-8919-6ccf24f790f3"),sQuery(id+"F0.wireOp",EDGE,"84cf82ef-edac-41b9-a85a-52613d906b4f"),sQuery(id+"F0.wireOp",EDGE,"6f9bf3da-cc22-4046-8398-726881e65be8"),sQuery(id+"F0.wireOp",EDGE,"2cd02f45-4707-4b19-8dd1-68e3a048a7ed"),sQuery(id+"F0.wireOp",EDGE,"37396fa6-3296-48a8-b41d-f09d90a4feb7"),sQuery(id+"F0.wireOp",EDGE,"16ba9f7e-b05a-42c2-9539-ea36d1e6b86a"),sQuery(id+"F0.wireOp",EDGE,"d231a9ad-2026-44ee-a8e7-0275c1f8ec7d"),sQuery(id+"F0.wireOp",EDGE,"9f2dcf6f-a8de-437f-87c6-6b6e7ba86ed4"),sQuery(id+"F0.wireOp",EDGE,"52981f33-067a-4c2c-8828-b65ca661ad9c"),sQuery(id+"F0.wireOp",EDGE,"408cb5d9-231a-45ac-9bc4-41ac58c850e2"),sQuery(id+"F0.wireOp",EDGE,"9c21c1e0-d1b5-48d7-abac-f7b2b27de3de"),sQuery(id+"F0.wireOp",EDGE,"ffec0fd8-18a6-48fd-bf9a-7957bed396b8"),sQuery(id+"F0.wireOp",EDGE,"d5f5b610-cce5-4a58-adbd-be45ea3871aa"),sQuery(id+"F0.wireOp",EDGE,"eabe1d8d-9ed9-49f3-89ee-a4827284ac98"),sQuery(id+"F0.wireOp",EDGE,"cbc9e552-14e3-4b93-ae99-33b61fc300db"),sQuery(id+"F0.wireOp",EDGE,"30ecbc7d-613a-4bcc-817d-513a33f7f0e3"),sQuery(id+"F0.wireOp",EDGE,"18e8bb2b-b683-494f-a511-82aaf8420edb"),sQuery(id+"F0.wireOp",EDGE,"ddafc5e0-30d6-40e1-81d6-725c5972dba5"),sQuery(id+"F0.wireOp",EDGE,"fa8f1ce2-166e-48cb-afe0-128b0491fb0b"),sQuery(id+"F0.wireOp",EDGE,"1407d160-d278-4643-89c7-3521a8615b1f"),sQuery(id+"F0.wireOp",EDGE,"596a3357-e609-4669-af30-35b89a1584c6"),sQuery(id+"F0.wireOp",EDGE,"aaa4bf7b-662e-4ef3-a93a-3e9ffd297c4a"),sQuery(id+"F0.wireOp",EDGE,"9e65a868-0fb0-4d7e-9214-2ab33384a621"),sQuery(id+"F0.wireOp",EDGE,"8d5e906f-d52c-4eb1-9858-520727ad48c6"),sQuery(id+"F0.wireOp",EDGE,"cdc1a19b-cab9-41d1-a0a0-ce410699439c"),sQuery(id+"F0.wireOp",EDGE,"9b914fc0-16d4-47ca-8d9b-6efdd6fab2a3"),sQuery(id+"F0.wireOp",EDGE,"6e8fda0c-ef1d-458d-97ad-7745eaae0de2"),sQuery(id+"F0.wireOp",EDGE,"9db401f3-bab6-4f9c-a4f5-060f44c71ed1"),sQuery(id+"F0.wireOp",EDGE,"64e30ee5-41fe-43f3-8d91-b5800c139c95"),sQuery(id+"F0.wireOp",EDGE,"ec9cbeda-cb19-48ba-8dad-ec7cb6960f07"),sQuery(id+"F0.wireOp",EDGE,"92b309bb-47f7-4e8d-b569-b5f4bacc4261"),sQuery(id+"F0.wireOp",EDGE,"ef0f9529-8913-4cc2-bdb9-173a1dcbd115"),sQuery(id+"F0.wireOp",EDGE,"a2642eba-f641-4a26-a32b-bfcfb862dfa9"),sQuery(id+"F0.wireOp",EDGE,"8fec02c0-0363-4921-b789-f8c7a246b991"),sQuery(id+"F0.wireOp",EDGE,"b7c46eba-08fe-43a1-849b-bd1cca90a192"),sQuery(id+"F0.wireOp",EDGE,"6404b644-1840-45f7-8d0c-8accd017dd66"),sQuery(id+"F0.wireOp",EDGE,"93b70d59-cc48-402b-abd9-8d28f111c5ae"),sQuery(id+"F0.wireOp",EDGE,"0165fdec-1e62-4ad5-b3bc-38bb427360d7"),sQuery(id+"F0.wireOp",EDGE,"dccbc5c7-b9c2-4a71-bee8-2d60517ef9bd"),sQuery(id+"F0.wireOp",EDGE,"11e15b41-16a7-466e-96b0-076cef006174"),sQuery(id+"F0.wireOp",EDGE,"32dd4082-3509-4317-b6b9-6983ee8b7eff"),sQuery(id+"F0.wireOp",EDGE,"d55de4be-f282-485c-8cc2-362e4dcf16e6"),sQuery(id+"F0.wireOp",EDGE,"066d381d-f4a1-483b-8420-2492fa9c0dee"),sQuery(id+"F0.wireOp",EDGE,"5973b24d-27e9-4c40-b27f-8a40e30e9e32"),sQuery(id+"F0.wireOp",EDGE,"dd5682a7-0c74-4785-b55a-80176aa887f3"),sQuery(id+"F0.wireOp",EDGE,"8970e274-b150-45a8-bd0e-b3dda6f19f5b"),sQuery(id+"F0.wireOp",EDGE,"1a6e99f7-6c19-4570-8469-593ea103196b"),sQuery(id+"F0.wireOp",EDGE,"fb2402fe-453c-4e08-a8d0-2d908824c35c"),sQuery(id+"F0.wireOp",EDGE,"f908f7fd-2308-4a7d-b3b0-0a0b636c3764"),sQuery(id+"F0.wireOp",EDGE,"013f7eed-213f-4062-b37a-07f860009d78"),sQuery(id+"F0.wireOp",EDGE,"4a9e8910-ab63-4e98-8661-fd4f87db198f"),sQuery(id+"F0.wireOp",EDGE,"24a2a741-2185-4e06-9c02-27ec9086295c"),sQuery(id+"F0.wireOp",EDGE,"6835a710-b641-496c-bb60-bce9f4523c9e"),sQuery(id+"F0.wireOp",EDGE,"cdcfba0a-b4bd-403d-b96b-7301683a2622"),sQuery(id+"F0.wireOp",EDGE,"b9c45430-50bb-4e9d-8b0c-94a2aa1b7db1"),sQuery(id+"F0.wireOp",EDGE,"3d92a9fd-ad5b-4e3d-a7d9-05251f90bfbf"),sQuery(id+"F0.wireOp",EDGE,"6bdf556d-bc69-48f3-abf7-2d4d15e80244"),sQuery(id+"F0.wireOp",EDGE,"53b29f34-d141-49cf-8ecb-5610867f1fe1"),sQuery(id+"F0.wireOp",EDGE,"19573c38-7ee5-4907-b512-03d4f02fe7fb"),sQuery(id+"F0.wireOp",EDGE,"faf7ae07-8462-4f63-8af4-a3e6b0a81886"),sQuery(id+"F0.wireOp",EDGE,"05abe8ee-4be5-42de-ac33-4a24a8ee80d9"),sQuery(id+"F0.wireOp",EDGE,"de4761e7-ba1c-4691-850e-ea6e348e24be"),sQuery(id+"F0.wireOp",EDGE,"dac8c1c3-0d12-4fbf-b8ed-c2276810aec3"),sQuery(id+"F0.wireOp",EDGE,"3d50c741-c91f-4076-9353-8bc19711a71a"),sQuery(id+"F0.wireOp",EDGE,"dcb86853-e0ec-4ea4-8223-daa0ca295cb2"),sQuery(id+"F0.wireOp",EDGE,"4860a458-28ee-4d85-b6b2-514179390969"),sQuery(id+"F0.wireOp",EDGE,"863a4de6-e62c-4218-b5f0-2dd120242739"),sQuery(id+"F0.wireOp",EDGE,"1a4824a5-aa08-4c33-a72a-700e6606d007"),sQuery(id+"F0.wireOp",EDGE,"7da0cf67-c0e7-4bf9-b176-b73716ecd21e"),sQuery(id+"F0.wireOp",EDGE,"aee0c4cd-c753-4a05-b9bc-a1b32bcff9ab"),sQuery(id+"F0.wireOp",EDGE,"2b34d226-a438-4445-a074-3bbff589a12c"),sQuery(id+"F0.wireOp",EDGE,"ebb1c9a2-ae9c-45bc-8668-3fca7c21c9f8"),sQuery(id+"F0.wireOp",EDGE,"01c04197-1e48-4140-af38-0e1c6338c7cd"),sQuery(id+"F0.wireOp",EDGE,"49f0dd93-1389-4d00-81c6-36f6d01e0acc"),sQuery(id+"F0.wireOp",EDGE,"b4d31c4c-d272-4c9f-bae1-896e32a638b9"),sQuery(id+"F0.wireOp",EDGE,"0871fd1b-e3df-428e-9adf-ca3fcc696a25"),sQuery(id+"F0.wireOp",EDGE,"902e6c5c-9be4-49d6-99a8-803def05f00e"),sQuery(id+"F0.wireOp",EDGE,"03598667-7d25-4f0b-a50b-539104a50732"),sQuery(id+"F0.wireOp",EDGE,"190856f5-b755-44da-860d-ca5b4252228c"),sQuery(id+"F0.wireOp",EDGE,"6a1a2d63-a907-40fc-8bf7-ba97b39d8e7b"),sQuery(id+"F0.wireOp",EDGE,"fd5f3a51-52b9-4138-bb86-8b6a4700a89f"),sQuery(id+"F0.wireOp",EDGE,"2a3701fa-a3c5-4d80-b8ea-44c45627bcf0"),sQuery(id+"F0.wireOp",EDGE,"fa5d5fc2-ae96-4ab6-9e49-0351f26fc7b6"),sQuery(id+"F0.wireOp",EDGE,"e7ee2680-a35a-4d00-a959-63c1e9090b4c"),sQuery(id+"F0.wireOp",EDGE,"56cd987c-73de-43c7-b7e7-9d145fbb61d1"),sQuery(id+"F0.wireOp",EDGE,"5007d5d5-27f6-4491-896c-7dbb7ec46efb"),sQuery(id+"F0.wireOp",EDGE,"e190d2b4-efe9-4e46-acb6-eea77c7750eb"),sQuery(id+"F0.wireOp",EDGE,"479cbb70-0ac4-4098-9652-b2a87cac6553"),sQuery(id+"F0.wireOp",EDGE,"57c44ddd-76f8-49e1-83e0-e39e14421621"),sQuery(id+"F0.wireOp",EDGE,"b611a3f5-8dbc-4886-947f-fcd555503140"),sQuery(id+"F0.wireOp",EDGE,"06da85e9-838a-4f38-83cb-3d4113e69b32"),sQuery(id+"F0.wireOp",EDGE,"106c5fd0-f510-44a4-89f0-21162d4a1c0a"),sQuery(id+"F0.wireOp",EDGE,"5b6c80ac-1378-4d9a-af25-24f0d3f4cbac"),sQuery(id+"F0.wireOp",EDGE,"48948ce6-4ff7-4bbf-a070-428be44556bf"),sQuery(id+"F0.wireOp",EDGE,"ec884fcc-42de-4706-833d-90be3815d586"),sQuery(id+"F0.wireOp",EDGE,"81c4cbd6-e2ef-45cc-8291-ebd9ec264de1"),sQuery(id+"F0.wireOp",EDGE,"b2180cd8-9f8d-40fc-809e-6f038e9e6d7f"),sQuery(id+"F0.wireOp",EDGE,"b95729eb-fd2a-49de-b7c5-2099ac2c1fe1"),sQuery(id+"F0.wireOp",EDGE,"f341f5ef-ef4b-44d2-bbf0-2e3f0e31eab8"),sQuery(id+"F0.wireOp",EDGE,"a47b10b5-172f-4576-b746-98cc0bd9115f"),sQuery(id+"F0.wireOp",EDGE,"bdeb045e-e9e6-4f3d-bf3c-57d47329860d"),sQuery(id+"F0.wireOp",EDGE,"f97a3218-2a13-49ba-ad6f-89afafa004a2"),sQuery(id+"F0.wireOp",EDGE,"619c096f-86a8-4dfb-9653-5fd9eecd998a"),sQuery(id+"F0.wireOp",EDGE,"d0f89b8e-6007-4e81-9aee-9f3ad6569f13"),sQuery(id+"F0.wireOp",EDGE,"6790b9e0-7c1e-4f57-844e-70dc42300314"),sQuery(id+"F0.wireOp",EDGE,"cc83a62f-1fd4-47dd-8c3c-e763de5b27c2"),sQuery(id+"F0.wireOp",EDGE,"a35115cf-91f0-444a-90e6-3ff1a4b93f76"),sQuery(id+"F0.wireOp",EDGE,"1ddb8f84-f822-43b7-adaf-1f05a94ccb75"),sQuery(id+"F0.wireOp",EDGE,"47a3c889-4339-44a4-a945-e61c64b84eb7"),sQuery(id+"F0.wireOp",EDGE,"2af5b045-2a63-4e5f-ba14-8b5f69cc8cba"),sQuery(id+"F0.wireOp",EDGE,"f9e1c701-329e-48c4-b27f-765083167c74"),sQuery(id+"F0.wireOp",EDGE,"19618c68-4d1d-4cf7-91ca-0bdcb9d0fbf0"),sQuery(id+"F0.wireOp",EDGE,"23edb927-c75a-46ac-92eb-00791728a506"),sQuery(id+"F0.wireOp",EDGE,"2a8ff039-eef2-413c-a668-2a859320d89f"),sQuery(id+"F0.wireOp",EDGE,"fad287d6-2bb9-4622-accd-3ba0246237f3"),sQuery(id+"F0.wireOp",EDGE,"2cb2ba93-be74-46d4-88c6-69e04584695c"),sQuery(id+"F0.wireOp",EDGE,"5064c32e-df9e-488d-a9ad-9732fbd11f64"),sQuery(id+"F0.wireOp",EDGE,"1b72502b-0aad-4e50-9227-89f6630dab28"),sQuery(id+"F0.wireOp",EDGE,"5cb1ae26-d3e4-4358-87d9-602ca285b8bd"),sQuery(id+"F0.wireOp",EDGE,"7c32ab9f-19a5-4b67-a7f8-a0daddc378c4"),sQuery(id+"F0.wireOp",EDGE,"73296e7b-a954-4a39-99af-19c76bc3b81d"),sQuery(id+"F0.wireOp",EDGE,"64fbcc9c-0e51-43d4-8dc1-84c2bb7acfa4"),sQuery(id+"F0.wireOp",EDGE,"5e196178-a669-4fbb-b5b8-b5765a895a2f"),sQuery(id+"F0.wireOp",EDGE,"bab93f60-94f4-475b-a2a8-85b7d3f98929"),sQuery(id+"F0.wireOp",EDGE,"04e6edd2-5439-4c3a-8322-9073194e9b57"),sQuery(id+"F0.wireOp",EDGE,"5af41a84-4c87-4b43-9ddd-e31fddf844f1"),sQuery(id+"F0.wireOp",EDGE,"b8f01260-ba5f-4297-a4e8-81b4a7f9b968"),sQuery(id+"F0.wireOp",EDGE,"8f55b24c-2efe-498a-986b-860bc9d6cd62"),sQuery(id+"F0.wireOp",EDGE,"2c8e42cc-6f60-4f6a-be4c-85decde6bf3f"),sQuery(id+"F0.wireOp",EDGE,"70a84c8a-e315-4ed8-9662-987b4c45fff3"),sQuery(id+"F0.wireOp",EDGE,"220e9e1f-b452-49f1-a8c2-dc11710d8829"),sQuery(id+"F0.wireOp",EDGE,"9f378ead-aa27-47e6-8c62-cde23577b32d"),sQuery(id+"F0.wireOp",EDGE,"68de62c7-b686-45e9-9d1e-9fa7e5bc618e"),sQuery(id+"F0.wireOp",EDGE,"f2014a56-10f8-44ca-bf32-e221ee8ad32c"),sQuery(id+"F0.wireOp",EDGE,"cf6c1533-56d7-40ce-b47d-dd6e8e09b61c"),sQuery(id+"F0.wireOp",EDGE,"c721f733-9a75-4826-9c17-0644a6e1c414"),sQuery(id+"F0.wireOp",EDGE,"368b4ca7-e84b-4f92-981b-463213aeef25"),sQuery(id+"F0.wireOp",EDGE,"1c890408-7fd5-4f80-a989-c0cac3289d88"),sQuery(id+"F0.wireOp",EDGE,"d25b4a45-5b30-4ccf-9de1-d661d6489a37"),sQuery(id+"F0.wireOp",EDGE,"a107cb7b-62f0-4eb4-bf4d-3ed1c2a4ff78"),sQuery(id+"F0.wireOp",EDGE,"e5de749d-678c-46ca-b855-3fe615f08225"),sQuery(id+"F0.wireOp",EDGE,"2957ea33-4171-4f00-91c2-95ccdc445836"),sQuery(id+"F0.wireOp",EDGE,"83730173-db89-47a2-bcfc-1532d87d5f36"),sQuery(id+"F0.wireOp",EDGE,"56082139-6c9e-4a8e-8e40-eaf54a4f1120"),sQuery(id+"F0.wireOp",EDGE,"ea7689ac-adf6-457e-8852-03326ef56f7a"),sQuery(id+"F0.wireOp",EDGE,"5fb9af14-7811-4668-ac88-c56c07112ad6"),sQuery(id+"F0.wireOp",EDGE,"527925de-cf95-42d0-bb4d-5594059b2ff4"),sQuery(id+"F0.wireOp",EDGE,"74f4b52b-eebe-4d7b-b208-5bcd777e5ec2"),sQuery(id+"F0.wireOp",EDGE,"66314b9e-1996-4563-9226-e5e3be6b3aed"),sQuery(id+"F0.wireOp",EDGE,"1ead1fcb-a463-4bab-9d32-397705594f24"),sQuery(id+"F0.wireOp",EDGE,"613ce62b-f68f-4c15-a27c-9b50a5fa2a00"),sQuery(id+"F0.wireOp",EDGE,"a8c22376-5072-4371-b465-9ad4376e86dc"),sQuery(id+"F0.wireOp",EDGE,"08ef1cda-83df-40e6-84e5-941aed97a636"),sQuery(id+"F0.wireOp",EDGE,"251eacbe-8c6e-42fe-a1e3-71854ba044cf"),sQuery(id+"F0.wireOp",EDGE,"1dcf136b-b80e-497e-98d9-22fde25308dd"),sQuery(id+"F0.wireOp",EDGE,"4150e4c4-13a6-443e-92dc-7a9371a1877a"),sQuery(id+"F0.wireOp",EDGE,"29b06639-b109-4d70-9f8e-288401b0f229"),sQuery(id+"F0.wireOp",EDGE,"48c1294c-14a0-4b8b-9ad7-77ebedf7ee54"),sQuery(id+"F0.wireOp",EDGE,"25d626b8-3abd-43ef-9732-81caddf6bd82"),sQuery(id+"F0.wireOp",EDGE,"275b94ba-070b-4ead-a560-9e8b6b5bf311"),sQuery(id+"F0.wireOp",EDGE,"2933ded0-0d17-4d1d-846c-eeafafe6ccef"),sQuery(id+"F0.wireOp",EDGE,"5618fc39-da46-4527-93dd-0cc252efd7f7"),sQuery(id+"F0.wireOp",EDGE,"e13ba41f-e87c-4875-92d6-6a6be78c2523"),sQuery(id+"F0.wireOp",EDGE,"8c56cf67-9d34-4a0c-ab5b-c2c227bdd369"),sQuery(id+"F0.wireOp",EDGE,"29bf8a71-d6e7-4392-9fc8-749ee2964058"),sQuery(id+"F0.wireOp",EDGE,"b207ba18-1668-4809-ab9b-46f572db75c3"),sQuery(id+"F0.wireOp",EDGE,"16964af4-acd1-46d3-8050-b6c3ecf75b83"),sQuery(id+"F0.wireOp",EDGE,"6ecc3c55-6353-496e-acb4-d7247a16f50a"),sQuery(id+"F0.wireOp",EDGE,"6070db21-0c69-4749-b50e-18b8beab8b46"),sQuery(id+"F0.wireOp",EDGE,"c83d7944-b2e9-4616-958f-c815d7cbbe68"),sQuery(id+"F0.wireOp",EDGE,"5641a79a-c677-425c-b636-e1455cd0c030"),sQuery(id+"F0.wireOp",EDGE,"a5c13a0f-1164-448d-b50c-e6a205f75f86"),sQuery(id+"F0.wireOp",EDGE,"c35948c1-1d81-4a9d-9036-f8655d5d768b"),sQuery(id+"F0.wireOp",EDGE,"2c78cc5c-248a-4f40-af22-8a480499544e"),sQuery(id+"F0.wireOp",EDGE,"4c9af1d3-321e-43b7-8815-0e0836b24b58"),sQuery(id+"F0.wireOp",EDGE,"e9b215d5-5831-44a5-b760-fff7739d57ad"),sQuery(id+"F0.wireOp",EDGE,"2ba6f365-018e-40d0-9632-bde13f701955"),sQuery(id+"F0.wireOp",EDGE,"1d7c8e9c-567f-4ad6-a6e3-a809e78dc5fb"),sQuery(id+"F0.wireOp",EDGE,"72b6ff33-1d1d-488f-9fe8-152f75bf9776"),sQuery(id+"F0.wireOp",EDGE,"3ba2185f-48b3-4960-a53b-45459a3187af"),sQuery(id+"F0.wireOp",EDGE,"16b304db-3aab-46db-bd7c-6038e2d06a36"),sQuery(id+"F0.wireOp",EDGE,"f7b2b68c-f7c3-4f20-a51a-22e466f0231b"),sQuery(id+"F0.wireOp",EDGE,"991967c3-0b82-4b0e-bb55-12cab17636d5"),sQuery(id+"F0.wireOp",EDGE,"3576d61e-5b5e-4531-a86a-f9efaca913da"),sQuery(id+"F0.wireOp",EDGE,"c02db23e-b5ca-470f-ac65-69292ecf0cff"),sQuery(id+"F0.wireOp",EDGE,"eacbd2d9-2ed9-488f-944f-e8b7c3f78b3e"),sQuery(id+"F0.wireOp",EDGE,"1d0faf6c-a6d6-4096-9695-70604f8bad30"),sQuery(id+"F0.wireOp",EDGE,"ed5fb044-77ce-4ebb-a972-410f85b43bcb"),sQuery(id+"F0.wireOp",EDGE,"4df1c09a-3ffe-4816-8055-92edefc8a979"),sQuery(id+"F0.wireOp",EDGE,"5d4f7706-194f-48db-b873-a9f4989af888"),sQuery(id+"F0.wireOp",EDGE,"55cfc2c3-1ea2-49ca-93eb-e17f8b718343"),sQuery(id+"F0.wireOp",EDGE,"809a955d-ec6b-4ae8-a64a-96d2fa6f5298"),sQuery(id+"F0.wireOp",EDGE,"21cef66d-b80c-47da-a2dc-bc4cce8c7499"),sQuery(id+"F0.wireOp",EDGE,"bad0dfcd-52b2-4523-8167-51d2fa12cfee"),sQuery(id+"F0.wireOp",EDGE,"1e851b01-f015-45ca-a3bd-944fed59f9bd"),sQuery(id+"F0.wireOp",EDGE,"288ed6a4-c1e4-47b9-a233-7a95a7e455dc"),sQuery(id+"F0.wireOp",EDGE,"1eebe39a-53b4-499d-808d-a6975eb08b26"),sQuery(id+"F0.wireOp",EDGE,"1f64f298-b624-4d5f-93d8-653285cd1a5a"),sQuery(id+"F0.wireOp",EDGE,"7e1dfb90-5d4b-4035-8835-30a716cddff3"),sQuery(id+"F0.wireOp",EDGE,"a88f835b-43e7-4252-bb37-98e18cc451d9"),sQuery(id+"F0.wireOp",EDGE,"16d0170e-8391-4c54-84ce-0bbb9f535a07"),sQuery(id+"F0.wireOp",EDGE,"0879a2e5-c5f1-4117-9092-0e5e50c9141c"),sQuery(id+"F0.wireOp",EDGE,"05dcddf3-43ff-413f-b239-01f8f0f300ab"),sQuery(id+"F0.wireOp",EDGE,"04fccccf-0270-4038-a351-b721053f8429"),sQuery(id+"F0.wireOp",EDGE,"4faae2fc-fc27-4668-9f74-9cd9bee7b172"),sQuery(id+"F0.wireOp",EDGE,"05ca1c94-fa00-481d-a8e0-5a3ef8eaeacd"),sQuery(id+"F0.wireOp",EDGE,"d51a453d-3a9e-4675-93a8-59a99ec92bf4"),sQuery(id+"F0.wireOp",EDGE,"378b3c31-047d-46fb-b3a7-ac4ac1ba39b5"),sQuery(id+"F0.wireOp",EDGE,"82995fb6-bbff-4e37-9fca-e1cbc1db7ea8"),sQuery(id+"F0.wireOp",EDGE,"67563e4a-9b15-4152-867c-7c0e0df2a8c6"),sQuery(id+"F0.wireOp",EDGE,"6762e91b-83ed-4cbd-b532-a9b9ac7daf3f"),sQuery(id+"F0.wireOp",EDGE,"d3d51cab-dd0d-481e-b13f-520640a59d9e"),sQuery(id+"F0.wireOp",EDGE,"1ec3cf08-34fd-4720-93de-f84705f1b800"),sQuery(id+"F0.wireOp",EDGE,"37f301b2-37a0-4fdd-b58f-006c0550b2d5"),sQuery(id+"F0.wireOp",EDGE,"e19d5450-bd9a-4681-8df2-b78e537cea7e"),sQuery(id+"F0.wireOp",EDGE,"496c4abb-7432-4992-9ecb-fd8fb5807a96"),sQuery(id+"F0.wireOp",EDGE,"94930b1e-be43-476e-bbb5-0f71a74e4c82"),sQuery(id+"F0.wireOp",EDGE,"29bdb6a1-db5c-4b2f-a601-b8748da45dd4"),sQuery(id+"F0.wireOp",EDGE,"fdb63760-3eaf-4dbc-bb96-0ec81feeabb3"),sQuery(id+"F0.wireOp",EDGE,"6abc993b-5d6f-41e0-9d30-613df7748e2c"),sQuery(id+"F0.wireOp",EDGE,"cf51ced2-33cc-433d-a8e3-0a8e6ab4633e"),sQuery(id+"F0.wireOp",EDGE,"bd2df422-7c8b-4672-a167-a1e070c14377"),sQuery(id+"F0.wireOp",EDGE,"ac9b7676-6196-4fe7-8dc0-8b4c7f19035d"),sQuery(id+"F0.wireOp",EDGE,"0412b906-dab3-4683-8589-cecdf6cf9c8a"),sQuery(id+"F0.wireOp",EDGE,"6537b941-1335-4505-8017-8627c3c043be"),sQuery(id+"F0.wireOp",EDGE,"5f1e7276-0115-45c7-82e5-f330e3c2fb74"),sQuery(id+"F0.wireOp",EDGE,"a4489bfa-5ba1-44e6-b65f-7ed1139340bc"),sQuery(id+"F0.wireOp",EDGE,"23d198d4-9637-4b64-b350-3d9b97209b93"),sQuery(id+"F0.wireOp",EDGE,"42dc715e-67ce-47dd-bc7e-9565251bcfd0"),sQuery(id+"F0.wireOp",EDGE,"cd9e4183-7cc9-413d-bd94-20a9d3a74fc9"),sQuery(id+"F0.wireOp",EDGE,"03de00b4-bee8-4db3-8c6f-fbf8bb530c55"),sQuery(id+"F0.wireOp",EDGE,"8b2c66e1-2722-4951-8ff3-82a7355ef1c2"),sQuery(id+"F0.wireOp",EDGE,"7f58e016-16fa-4bda-becf-3a110b6b0ba8"),sQuery(id+"F0.wireOp",EDGE,"2e4b4eea-771e-44e1-a790-7858300a958c"),sQuery(id+"F0.wireOp",EDGE,"66edb572-61a0-458d-acb6-a9c38e7c9817"),sQuery(id+"F0.wireOp",EDGE,"ef92da9d-23fe-45d1-a911-75a33661f011"),sQuery(id+"F0.wireOp",EDGE,"5bfa7897-d6c6-48be-be5b-6def31250002"),sQuery(id+"F0.wireOp",EDGE,"8231bbcd-b2a9-4737-b60c-249983317a18"),sQuery(id+"F0.wireOp",EDGE,"fbc1c214-68d0-42ec-9c45-bee98f097555"),sQuery(id+"F0.wireOp",EDGE,"8a3a4b2a-3e59-4b07-8100-140c4c981be5"),sQuery(id+"F0.wireOp",EDGE,"7e709ee0-ea37-4f65-a946-660b1798bdf2"),sQuery(id+"F0.wireOp",EDGE,"500b1576-4e8a-47ef-af30-215078d273ce"),sQuery(id+"F0.wireOp",EDGE,"3c244ecb-d982-4908-a7af-12a24f38b454"),sQuery(id+"F0.wireOp",EDGE,"8de3b702-b5a6-42dc-b70a-b8532fbf20c6"),sQuery(id+"F0.wireOp",EDGE,"10e3de8a-fc30-4cff-9237-3e22bd9e3232"),sQuery(id+"F0.wireOp",EDGE,"b6f9acd2-4eee-4475-a5b4-9e1ce02e0f0a"),sQuery(id+"F0.wireOp",EDGE,"19d699ee-cbd7-4546-800e-109ea1046660"),sQuery(id+"F0.wireOp",EDGE,"8a712665-6dc5-4123-969b-d9c7bdb6eea8"),sQuery(id+"F0.wireOp",EDGE,"29c2415b-a683-44f6-9851-56f80d3d0f17"),sQuery(id+"F0.wireOp",EDGE,"fc8e5354-b49d-4e90-8587-4fad446cdc7a"),sQuery(id+"F0.wireOp",EDGE,"1d97e188-d88c-40ec-b67b-ebeadd9dbc9b"),sQuery(id+"F0.wireOp",EDGE,"83a5129d-c98b-4703-85cf-65f83663392a"),sQuery(id+"F0.wireOp",EDGE,"38459e7b-decf-425a-80e7-dd305edb38a6"),sQuery(id+"F0.wireOp",EDGE,"8a94d0ab-b270-411c-a6b1-3108556eeb98"),sQuery(id+"F0.wireOp",EDGE,"c00de532-d654-4b73-808b-7e7d03ecc37a"),sQuery(id+"F0.wireOp",EDGE,"9baffacd-999b-4c18-91c6-c5dda2931f50"),sQuery(id+"F0.wireOp",EDGE,"da6f64c5-5353-44d2-9fa2-6d1f2e632f35"),sQuery(id+"F0.wireOp",EDGE,"14e3b729-da8a-4127-8f21-d55b9a6fb4aa"),sQuery(id+"F0.wireOp",EDGE,"9df101d5-80ed-4980-8b55-10ecc94a02d8"),sQuery(id+"F0.wireOp",EDGE,"e638abd0-6801-4534-9919-44cde57cbd5b"),sQuery(id+"F0.wireOp",EDGE,"c0059b76-6e1b-4eaa-8415-b4e65df05b37"),sQuery(id+"F0.wireOp",EDGE,"c04777a8-102f-4856-b92a-2e358a58d09e"),sQuery(id+"F0.wireOp",EDGE,"9b06d21f-a5f0-48cc-8ba2-fa8c291e5086"),sQuery(id+"F0.wireOp",EDGE,"e7ee14ce-ee89-4084-aa7f-54b2d9003392"),sQuery(id+"F0.wireOp",EDGE,"8dc047b9-710b-48d6-adec-864b411053f1"),sQuery(id+"F0.wireOp",EDGE,"fb02d67f-8f5c-45fb-a3a7-b39d9548de9f"),sQuery(id+"F0.wireOp",EDGE,"3f1c47f8-75a6-4e30-ae12-d541cd37cc83"),sQuery(id+"F0.wireOp",EDGE,"ae22e717-8f71-49b8-9e39-3b406532921e"),sQuery(id+"F0.wireOp",EDGE,"22017561-5b3b-4ff9-b42c-8ec01e4276ca"),sQuery(id+"F0.wireOp",EDGE,"bed059a4-dd32-4a75-b05a-074b6281357f"),sQuery(id+"F0.wireOp",EDGE,"c0586c55-c3ea-4c35-a08c-15e696a43b99"),sQuery(id+"F0.wireOp",EDGE,"303c49fd-fa39-47ae-a902-4dccbb48fc6a"),sQuery(id+"F0.wireOp",EDGE,"fb68c198-0212-4bcb-bf57-08a5b7e91de6"),sQuery(id+"F0.wireOp",EDGE,"ee4d1f3c-998d-4543-9810-a37c8be260cc"),sQuery(id+"F0.wireOp",EDGE,"325099e8-ab89-4a35-a291-7fe3fc5821f3"),sQuery(id+"F0.wireOp",EDGE,"60f210ef-b77f-4b66-abb3-8deec2e0e0bb"),sQuery(id+"F0.wireOp",EDGE,"547cdca8-b857-4bb6-9f4f-58ef7bc8e838"),sQuery(id+"F0.wireOp",EDGE,"d16bc155-9374-4df2-b6f8-ff9b66236ed3"),sQuery(id+"F0.wireOp",EDGE,"9ef04104-79ef-4c74-9da8-eceb0cb3a4fe"),sQuery(id+"F0.wireOp",EDGE,"bcee84cf-422a-4575-87c7-1479d367d2cf"),sQuery(id+"F0.wireOp",EDGE,"b9c310c4-f7ad-4dbd-8673-34254f61f560"),sQuery(id+"F0.wireOp",EDGE,"497fc37e-f6f6-4b99-8b07-0360bc2a9d0e"),sQuery(id+"F0.wireOp",EDGE,"c10a195e-950b-4ef1-81a0-f20b35e1dadd"),sQuery(id+"F0.wireOp",EDGE,"ff1639dc-0830-432c-9654-0467c31231af"),sQuery(id+"F0.wireOp",EDGE,"23ad70da-acb1-4188-a4a8-c5af692e904a"),sQuery(id+"F0.wireOp",EDGE,"a8dd13a0-8968-46c5-acfa-195848781c1c"),sQuery(id+"F0.wireOp",EDGE,"8156b7ce-230b-48e1-aa1b-894d7316a82f"),sQuery(id+"F0.wireOp",EDGE,"b6facb5f-a5bd-40a4-9b11-e35c975b3f11"),sQuery(id+"F0.wireOp",EDGE,"07a15268-51ad-4d49-aca9-99fb6002e07d"),sQuery(id+"F0.wireOp",EDGE,"b56aef46-9202-4632-96a0-d00f2144ea35"),sQuery(id+"F0.wireOp",EDGE,"5439e26b-5952-4da8-bd75-4901e0e357cf"),sQuery(id+"F0.wireOp",EDGE,"127deab1-32e5-43cb-be08-b1c22e829773"),sQuery(id+"F0.wireOp",EDGE,"20ff72b7-5221-4f09-9edb-d3e930f05ba0"),sQuery(id+"F0.wireOp",EDGE,"1a24371d-c4cb-490c-97cd-55eedcdae095"),sQuery(id+"F0.wireOp",EDGE,"ea3ea07d-1b41-4802-b222-d96af10a48ef"),sQuery(id+"F0.wireOp",EDGE,"07ec1ecc-1a48-4fe7-b261-08e6caac05a2"),sQuery(id+"F0.wireOp",EDGE,"f6eee84f-0b84-41bf-92cd-571c99526fdb"),sQuery(id+"F0.wireOp",EDGE,"50106d84-7118-4f31-aab1-b25162fad229"),sQuery(id+"F0.wireOp",EDGE,"a8ec2e87-9788-4528-96c4-8cc6e6622ee4"),sQuery(id+"F0.wireOp",EDGE,"dd9bd91e-b22f-4125-8bc9-33acf8a34fb6"),sQuery(id+"F0.wireOp",EDGE,"23ceb77e-1dbe-4fb1-b360-71852dcd5f4f"),sQuery(id+"F0.wireOp",EDGE,"5971fce1-1edd-4e73-a59e-1bf903e028e7"),sQuery(id+"F0.wireOp",EDGE,"07e886e8-8b31-45f3-bf7e-5377ab8aaa6c"),sQuery(id+"F0.wireOp",EDGE,"b02181cd-1141-4195-931e-27cd5f67d936"),sQuery(id+"F0.wireOp",EDGE,"f404ba3d-95fe-497c-b900-a3e38243fd2c"),sQuery(id+"F0.wireOp",EDGE,"a724a2a2-e5d7-4f6e-b09d-3cee00442056"),sQuery(id+"F0.wireOp",EDGE,"826c2464-77cb-4336-9c5d-7eb6201290fe"),sQuery(id+"F0.wireOp",EDGE,"09e1373d-1870-49ef-8ab9-8036af7e093e"),sQuery(id+"F0.wireOp",EDGE,"14ebac5c-4536-4251-81bc-087c3384b32f"),sQuery(id+"F0.wireOp",EDGE,"bd8efbcf-97c7-41e9-8274-be8eab9fb382"),sQuery(id+"F0.wireOp",EDGE,"3e574c1f-8cdc-4690-b463-ff136dfcd360"),sQuery(id+"F0.wireOp",EDGE,"e4056e94-2d8a-4956-9234-2c9a5943a90a"),sQuery(id+"F0.wireOp",EDGE,"86da7161-c18f-49d9-93c7-1a22064837e4"),sQuery(id+"F0.wireOp",EDGE,"622f2018-0628-406c-9b5b-8f0f21c4a4dc"),sQuery(id+"F0.wireOp",EDGE,"0b9b8fe2-6d5f-4fa9-b0a1-efe2fda969b1"),sQuery(id+"F0.wireOp",EDGE,"5ef0ff38-6ebe-48cf-9e3e-1cfc3091928c"),sQuery(id+"F0.wireOp",EDGE,"78e54c78-bf96-4352-a758-ba91713fc725"),sQuery(id+"F0.wireOp",EDGE,"8e88edc4-cb30-4baf-968f-ebfe73424514"),sQuery(id+"F0.wireOp",EDGE,"8965327c-dd52-40d3-bf32-6a3949e96a9b"),sQuery(id+"F0.wireOp",EDGE,"8d87fff9-b896-4c97-bd6d-f2766d30679d"),sQuery(id+"F0.wireOp",EDGE,"89866aad-1e9a-4de7-a745-e64d56412f35"),sQuery(id+"F0.wireOp",EDGE,"905ac5f9-c21d-412c-8d54-d50402b60c54"),sQuery(id+"F0.wireOp",EDGE,"467ab422-03aa-417e-b913-b5e80ddb0c79"),sQuery(id+"F0.wireOp",EDGE,"58dbdb81-e612-40fb-95c5-ab7bf1a3d2de"),sQuery(id+"F0.wireOp",EDGE,"984d3f0b-13f2-487f-b755-4a0bba7058a4"),sQuery(id+"F0.wireOp",EDGE,"0a03f4d7-e756-4fd7-b006-fca0c5a48bca"),sQuery(id+"F0.wireOp",EDGE,"101bfc79-94c6-4c89-aecc-1a2471e45639"),sQuery(id+"F0.wireOp",EDGE,"bafda8bc-ec10-4e44-93de-7f3a36b19821"),sQuery(id+"F0.wireOp",EDGE,"057079dd-d07b-477b-8ded-5477aa495cb4"),sQuery(id+"F0.wireOp",EDGE,"1fb1e1a4-6633-473d-9e7c-d715702e041d"),sQuery(id+"F0.wireOp",EDGE,"06677649-1231-4f91-92a7-bae0b2f99e4e"),sQuery(id+"F0.wireOp",EDGE,"c673a0ec-5590-423f-b00a-c47544d5ce3e"),sQuery(id+"F0.wireOp",EDGE,"35866d11-f724-410c-99f3-ef9d173eaa3e"),sQuery(id+"F0.wireOp",EDGE,"50ebca05-b06f-4a84-9183-6c9ef9454d81"),sQuery(id+"F0.wireOp",EDGE,"02ccba90-f602-4031-b836-1d7658534b58"),sQuery(id+"F0.wireOp",EDGE,"d477b567-8937-45cc-afcc-cc7fd9d94498"),sQuery(id+"F0.wireOp",EDGE,"e7b6ada3-6ca2-4ffc-9d90-25d2595f40ac"),sQuery(id+"F0.wireOp",EDGE,"9892b1b2-e034-4a0d-a43c-ad3cfea8fe83"),sQuery(id+"F0.wireOp",EDGE,"7eb55d43-f956-4008-80c8-b4ab5805bcb7"),sQuery(id+"F0.wireOp",EDGE,"59a98bf0-71ee-4f28-abec-2204bb7d477a"),sQuery(id+"F0.wireOp",EDGE,"a879b169-3dcc-40eb-8ff6-a461203dd6dd"),sQuery(id+"F0.wireOp",EDGE,"fde519b3-a6ef-4a7d-aef6-996c976b111e"),sQuery(id+"F0.wireOp",EDGE,"1ae5a593-5d85-4dc8-86f0-c812bc5b5aba"),sQuery(id+"F0.wireOp",EDGE,"914f2caf-3d6b-4c35-ba92-f6993b2fbc88"),sQuery(id+"F0.wireOp",EDGE,"0f978844-0975-4ef8-8208-a486fd79bb82"),sQuery(id+"F0.wireOp",EDGE,"5a25cdce-64f0-4099-80ce-602216827c90"),sQuery(id+"F0.wireOp",EDGE,"d3bc9758-d3a8-4820-8c46-5f7e7d42b4e3"),sQuery(id+"F0.wireOp",EDGE,"17fd1400-0a30-4e68-a373-c4e5d2f26af7"),sQuery(id+"F0.wireOp",EDGE,"75660254-19bd-4f5f-a0a2-bcee4d00c499"),sQuery(id+"F0.wireOp",EDGE,"9e8646c9-e721-4e54-a392-2f54c8f7b81b"),sQuery(id+"F0.wireOp",EDGE,"9ab30725-9705-408f-a94e-ecf0a6bbe568"),sQuery(id+"F0.wireOp",EDGE,"308d3d82-aebc-4eb4-bfa0-cdf01e8c387e"),sQuery(id+"F0.wireOp",EDGE,"c0a0d6b5-ca63-4314-93ea-3eaaef76272b"),sQuery(id+"F0.wireOp",EDGE,"f757b01b-a185-4ce0-832d-5ad9c622d69f"),sQuery(id+"F0.wireOp",EDGE,"ab4fee9c-1f4b-4b8d-a66b-7a33e98ee4fa"),sQuery(id+"F0.wireOp",EDGE,"73d98c56-dcfc-443c-9903-d209168277be"),sQuery(id+"F0.wireOp",EDGE,"e73cdc64-0ab5-4634-a86d-ccacd0f9ba69"),sQuery(id+"F0.wireOp",EDGE,"a39e3194-2c4c-4f73-8f81-beee18b7d4fb"),sQuery(id+"F0.wireOp",EDGE,"2d2d454e-a145-4402-9430-90765ca3ef39"),sQuery(id+"F0.wireOp",EDGE,"9b395d58-f0b2-45b7-9d38-3ba5c381c6b3"),sQuery(id+"F0.wireOp",EDGE,"d6e9afce-2052-45c1-a3cd-bc5c770fcc30"),sQuery(id+"F0.wireOp",EDGE,"58005fae-83f3-48d1-a1f3-7d7777f9102a"),sQuery(id+"F0.wireOp",EDGE,"55503e77-bfe1-477f-b6fa-769a57791085"),sQuery(id+"F0.wireOp",EDGE,"e3dece3a-4bf9-41fe-b60e-19e8eb760ec8"),sQuery(id+"F0.wireOp",EDGE,"e225004e-7c7a-4b1a-9d9c-bd8d5587ed73"),sQuery(id+"F0.wireOp",EDGE,"cafc7d21-8e1d-4988-9c3d-06c1626d1c78"),sQuery(id+"F0.wireOp",EDGE,"ba598920-6e2e-4a75-bfbe-3ffb7267c3f5"),sQuery(id+"F0.wireOp",EDGE,"084abf44-e056-4a2d-a8fe-978bda86ebed"),sQuery(id+"F0.wireOp",EDGE,"17dad1b1-9393-4f55-915c-28a70ace4381"),sQuery(id+"F0.wireOp",EDGE,"cf9cfd1c-cf0f-46fc-97df-dc42e5e02bc1"),sQuery(id+"F0.wireOp",EDGE,"520eeedb-eaf4-49ce-9d4d-96e7e921b325"),sQuery(id+"F0.wireOp",EDGE,"3260c2d0-a2cf-4cdf-a4d5-f4cbabbaf893"),sQuery(id+"F0.wireOp",EDGE,"f982051d-3c11-4c54-829a-76b7c6ab8a72"),sQuery(id+"F0.wireOp",EDGE,"e1493711-f827-47d6-8ed1-1d269d3dc0ea"),sQuery(id+"F0.wireOp",EDGE,"da87f092-cb25-4d5d-91d0-7d91c7cbd832"),sQuery(id+"F0.wireOp",EDGE,"b42b8699-d04e-475a-819f-08834b8a2bf6"),sQuery(id+"F0.wireOp",EDGE,"db176a9b-6a75-4e8e-bdda-4bbc5e733d20"),sQuery(id+"F0.wireOp",EDGE,"c76bc4ed-5e99-4e89-92f0-be5fd1922589"),sQuery(id+"F0.wireOp",EDGE,"041b93a8-293a-47b3-8f3a-a8973a17d960"),sQuery(id+"F0.wireOp",EDGE,"ba561d6b-0882-440b-b78d-15d78bdf95ee"),sQuery(id+"F0.wireOp",EDGE,"ad989c4c-a779-4d37-9193-1c4c5a1f90d2"),sQuery(id+"F0.wireOp",EDGE,"ce10184d-55c2-488a-9e2b-e780ec6733b7"),sQuery(id+"F0.wireOp",EDGE,"92646d3e-ea16-4ce9-9b98-f3d2afacf624"),sQuery(id+"F0.wireOp",EDGE,"1fef100a-8b69-47c6-ad45-17a7e9016646"),sQuery(id+"F0.wireOp",EDGE,"a9abf371-aaae-4980-97c3-618588223727"),sQuery(id+"F0.wireOp",EDGE,"9c051174-52e1-4caa-a03b-b18f81b07894"),sQuery(id+"F0.wireOp",EDGE,"09011d5e-2227-49ee-8a4f-ca06ef3bf9c9"),sQuery(id+"F0.wireOp",EDGE,"61318397-4f19-4a74-8977-958978d30da7"),sQuery(id+"F0.wireOp",EDGE,"3dd6c7c8-d307-49b4-bd14-b574e65bdeda"),sQuery(id+"F0.wireOp",EDGE,"6d587b47-ad53-4508-8fc8-b49e35483090"),sQuery(id+"F0.wireOp",EDGE,"c7b96cc4-2c11-4c08-9bc1-964cc6eae071"),sQuery(id+"F0.wireOp",EDGE,"d368f493-27cc-4be4-929c-f14eaf5c93de"),sQuery(id+"F0.wireOp",EDGE,"a0ab345c-276c-4998-a397-334cc7dec3a7"),sQuery(id+"F0.wireOp",EDGE,"fda3a3b5-c850-4c64-9562-c1df2376066b")])]});
            var Q1;
            Q1=makeQuery(id+"F1.opExtrude","SWEPT_BODY",BODY,{"disambiguationData":[OSD([sQuery(id+"F0.wireOp",EDGE,"da8af10c-896a-4133-b8ce-ebc45f5c24c5"),sQuery(id+"F0.wireOp",EDGE,"fad43c48-8b96-4971-a3f8-a184fc84315d"),sQuery(id+"F0.wireOp",EDGE,"e824da6a-9a5d-4185-85a7-30f1779f5760"),sQuery(id+"F0.wireOp",EDGE,"e1f86524-0aa2-48b8-82f7-e1304b778493"),sQuery(id+"F0.wireOp",EDGE,"cedc760c-091d-4eff-80df-05e96602bab6"),sQuery(id+"F0.wireOp",EDGE,"4c4edb97-8102-4b1a-97ba-730e25cc4ce8"),sQuery(id+"F0.wireOp",EDGE,"1d077ac3-8147-4ec8-abbe-1a2426ff541b"),sQuery(id+"F0.wireOp",EDGE,"432a942c-892c-4fad-ad11-d3edb4bf1eae"),sQuery(id+"F0.wireOp",EDGE,"4a9af2a0-81e3-4ec4-9d85-930770fa216b"),sQuery(id+"F0.wireOp",EDGE,"c84b2160-e281-45ce-8bdd-d7112c410c7f"),sQuery(id+"F0.wireOp",EDGE,"8401ae59-d9e7-4d1c-a86d-2a7d002904f6"),sQuery(id+"F0.wireOp",EDGE,"a4cb5fc4-0534-4dde-9732-5f1b3187bb3d"),sQuery(id+"F0.wireOp",EDGE,"898f730d-662a-4e74-922f-5fdb97f3a5e6"),sQuery(id+"F0.wireOp",EDGE,"bc045cdd-e9af-4036-b57c-ab4c9277f3e0"),sQuery(id+"F0.wireOp",EDGE,"a17a652d-d068-4f66-8a43-3621f9fde6ec"),sQuery(id+"F0.wireOp",EDGE,"9ac69f94-cb6a-4ca2-aa46-a7017f96a846"),sQuery(id+"F0.wireOp",EDGE,"c0c1cd1f-fcfe-40e4-8eec-0c8a7bae0b72"),sQuery(id+"F0.wireOp",EDGE,"f961c44e-8911-4777-af77-bc67517e8ce9"),sQuery(id+"F0.wireOp",EDGE,"69a6b619-cc2c-402e-ac67-ac24db60b4dc"),sQuery(id+"F0.wireOp",EDGE,"b30eef3a-b403-4089-8567-fa634c93204e"),sQuery(id+"F0.wireOp",EDGE,"014f38a3-4935-4915-8f6b-a76ea6e17068"),sQuery(id+"F0.wireOp",EDGE,"e276b7f3-0eca-4ad4-b053-0de55390ecf7"),sQuery(id+"F0.wireOp",EDGE,"753451c3-ac60-496c-8a00-c56fb99ae01e"),sQuery(id+"F0.wireOp",EDGE,"485ea49e-4760-46a9-95e6-ca681362c593"),sQuery(id+"F0.wireOp",EDGE,"75978265-d901-4d3b-9aa6-4f3f6013a116"),sQuery(id+"F0.wireOp",EDGE,"d13b9512-d136-433b-94b0-8dab7293442f"),sQuery(id+"F0.wireOp",EDGE,"072bf8f9-adf3-4fe1-9208-2f138e797777"),sQuery(id+"F0.wireOp",EDGE,"5c50cb7f-f035-451e-8110-aca223018d2a"),sQuery(id+"F0.wireOp",EDGE,"5a7af554-05fd-4dd2-b9cd-08d602c1684c"),sQuery(id+"F0.wireOp",EDGE,"95910d90-95cf-4e20-bc45-3ab85eec725a"),sQuery(id+"F0.wireOp",EDGE,"d68d32cc-c6c8-434f-bb80-601df3c9029a"),sQuery(id+"F0.wireOp",EDGE,"af75c8e8-6c4a-4a6b-ae23-8a88c47c9d18"),sQuery(id+"F0.wireOp",EDGE,"126a8443-3b56-40b2-b22a-89680e5e0d0b"),sQuery(id+"F0.wireOp",EDGE,"bbd3bb65-f112-4ae4-ac6d-678825be19d4"),sQuery(id+"F0.wireOp",EDGE,"3a337f22-8a5d-4ead-a7c6-a825c502f9a7"),sQuery(id+"F0.wireOp",EDGE,"e70a4fe1-2f20-4b89-8bab-1af8f7172cf4"),sQuery(id+"F0.wireOp",EDGE,"ccd77402-fb58-4298-8050-fb7e9e5f4582")])]});
            var Q2;
            Q2=makeQuery(id+"F1.opExtrude","SWEPT_BODY",BODY,{"disambiguationData":[OSD([sQuery(id+"F0.wireOp",EDGE,"834d6977-e806-4c23-b116-ce7edfcfaa7b"),sQuery(id+"F0.wireOp",EDGE,"bbcfc019-eed5-43d7-a190-8ec99b558aa0"),sQuery(id+"F0.wireOp",EDGE,"9a4184db-0aae-4f45-ad7c-4b2b94c45a01"),sQuery(id+"F0.wireOp",EDGE,"8e69ba7a-3209-4999-ae18-25fcfc38a144"),sQuery(id+"F0.wireOp",EDGE,"f9f003bd-df55-431c-818b-a14cc66eb9e4"),sQuery(id+"F0.wireOp",EDGE,"1fe5a7f7-2ef1-4c5e-b3fd-84fa455971a0"),sQuery(id+"F0.wireOp",EDGE,"488f2699-b0ba-45a8-b50f-3d9fe69c2a8c"),sQuery(id+"F0.wireOp",EDGE,"c45a37f5-da09-469e-b9b8-35e389e3391e"),sQuery(id+"F0.wireOp",EDGE,"1a7d6763-7add-49c1-8f91-b479956b3bdd"),sQuery(id+"F0.wireOp",EDGE,"3c07824b-5e8d-4e3c-8e8e-63d60d567141"),sQuery(id+"F0.wireOp",EDGE,"cfbb93e0-6d08-40a2-ad55-468a279fb9d9"),sQuery(id+"F0.wireOp",EDGE,"83e9ae67-ec3b-4327-b88d-d63562766e85"),sQuery(id+"F0.wireOp",EDGE,"9f6ca2bb-afd0-4eb3-946d-e821414f4453"),sQuery(id+"F0.wireOp",EDGE,"78c4557f-24f0-4844-8723-1914135b9086"),sQuery(id+"F0.wireOp",EDGE,"729ab94b-8344-4b8d-86d0-70ca1228f094"),sQuery(id+"F0.wireOp",EDGE,"41dcdb67-f35a-43a6-904a-26b9d81cd482"),sQuery(id+"F0.wireOp",EDGE,"b589fc30-224c-45ae-8f04-c8f0b329a975"),sQuery(id+"F0.wireOp",EDGE,"ac93deb6-e36c-4faf-b7e8-be605a122d44"),sQuery(id+"F0.wireOp",EDGE,"cff47f3d-35f8-44f2-81e1-008e6c47914b"),sQuery(id+"F0.wireOp",EDGE,"60de687e-3e15-44c5-b952-e2ce6254445f"),sQuery(id+"F0.wireOp",EDGE,"b1016adb-9947-4184-b1bc-ce3563b3735c"),sQuery(id+"F0.wireOp",EDGE,"545d3c0b-898b-4230-ae14-f998d2998a38"),sQuery(id+"F0.wireOp",EDGE,"154a4b1b-c065-4acd-a0a5-c6c3c2832def"),sQuery(id+"F0.wireOp",EDGE,"fb88536a-74b1-4537-a401-69c9f17bdc00"),sQuery(id+"F0.wireOp",EDGE,"b475e7fb-895a-44d1-aec8-f6a768487a6f"),sQuery(id+"F0.wireOp",EDGE,"fb47703b-c7f4-4907-836e-a0efbfa74f83"),sQuery(id+"F0.wireOp",EDGE,"c7b333f8-5ea6-4e71-869c-a260f16f53c2"),sQuery(id+"F0.wireOp",EDGE,"7deb210f-5948-4701-bbd2-8f02af6f34d8"),sQuery(id+"F0.wireOp",EDGE,"969aaeec-a49e-46b4-9919-1400294a42b0"),sQuery(id+"F0.wireOp",EDGE,"1bce26d7-747b-45b6-b5c2-169380ec867a"),sQuery(id+"F0.wireOp",EDGE,"1e49d8df-43cc-42b2-959f-511e5fb61356"),sQuery(id+"F0.wireOp",EDGE,"e0888c83-f72d-4896-80da-29aa6788b278"),sQuery(id+"F0.wireOp",EDGE,"96df53eb-5a98-4fb5-9bb6-38855f902298"),sQuery(id+"F0.wireOp",EDGE,"6fda5c3f-91a0-4b64-a804-5b930671645c"),sQuery(id+"F0.wireOp",EDGE,"dd59d7a0-41b9-4586-8584-ad372d9d9feb"),sQuery(id+"F0.wireOp",EDGE,"7cdea323-e78b-44de-81f0-5ea57691cfc0"),sQuery(id+"F0.wireOp",EDGE,"66e5abd2-7fa9-44c8-8e12-07f4fd3415af"),sQuery(id+"F0.wireOp",EDGE,"c0484ff3-e252-449a-9aff-25e9b7fdd824"),sQuery(id+"F0.wireOp",EDGE,"861bec80-f9d2-41ad-a927-deec84385102"),sQuery(id+"F0.wireOp",EDGE,"18895a8b-b0e4-4d14-b739-38220920ed8d"),sQuery(id+"F0.wireOp",EDGE,"2b8d466d-bb64-47ce-997b-9fdb4208ba9e"),sQuery(id+"F0.wireOp",EDGE,"c5fe9e2a-daee-4458-85e5-73372f51893a"),sQuery(id+"F0.wireOp",EDGE,"5fafdeb4-5ee5-4335-9de2-32af32adf409"),sQuery(id+"F0.wireOp",EDGE,"38be46ad-3ba0-4f1e-ab98-6ef6957e0ad3"),sQuery(id+"F0.wireOp",EDGE,"81593a27-88fb-42ce-a11d-7b59687bab93"),sQuery(id+"F0.wireOp",EDGE,"b56e9680-86c7-4f64-9e97-b0da4090dff7"),sQuery(id+"F0.wireOp",EDGE,"9a9fe6b4-1034-4f95-80a4-a6c1065ced3d"),sQuery(id+"F0.wireOp",EDGE,"ddf392df-0001-4e82-81b9-2daa65fcbca3"),sQuery(id+"F0.wireOp",EDGE,"86624942-74a5-4a0d-9dd9-3b6386b9ca4d"),sQuery(id+"F0.wireOp",EDGE,"ac50c577-bb50-4b46-ac5c-ab5e28101c5e"),sQuery(id+"F0.wireOp",EDGE,"871f0b44-4c0f-4e86-82ab-2d257ee3cb12"),sQuery(id+"F0.wireOp",EDGE,"ff1c2565-fa25-4425-a86d-9ea9597e0e2b"),sQuery(id+"F0.wireOp",EDGE,"ac59df92-587e-4228-9d6c-9a40246f1372"),sQuery(id+"F0.wireOp",EDGE,"a3ebab74-9c75-4a4c-a4ff-db670de74b1c"),sQuery(id+"F0.wireOp",EDGE,"7c9abaaf-ef9b-4c60-bb6c-2ca3b4ed9fab"),sQuery(id+"F0.wireOp",EDGE,"162d51b3-2021-45a9-b29b-d1fc2d27acc7"),sQuery(id+"F0.wireOp",EDGE,"32ef2770-9bcd-4514-8f03-248a2e52f14b"),sQuery(id+"F0.wireOp",EDGE,"8c652639-17b5-4942-a16e-ae6208f1ae53"),sQuery(id+"F0.wireOp",EDGE,"9f8bae2a-d9d1-4f9e-977e-27c661ebd892"),sQuery(id+"F0.wireOp",EDGE,"7e25c861-4d42-4d47-9b62-378ede528c33"),sQuery(id+"F0.wireOp",EDGE,"1978665c-2d5b-4ddc-99a1-8abe01775d66"),sQuery(id+"F0.wireOp",EDGE,"75cddc41-74a4-48e9-a8cb-09f8045fe106"),sQuery(id+"F0.wireOp",EDGE,"364c012f-464a-405b-a0e1-bbddd11ab3aa")])]});
            var Q3;
            Q3=makeQuery(id+"F1.opExtrude","SWEPT_BODY",BODY,{"disambiguationData":[OSD([sQuery(id+"F0.wireOp",EDGE,"abdaa881-ba7a-4edb-bdbc-db0cbd3f6efc"),sQuery(id+"F0.wireOp",EDGE,"f8895262-161b-4711-b5da-c7ffd2a350af"),sQuery(id+"F0.wireOp",EDGE,"f49e5ece-0761-4cec-91d1-9bcc2200a900"),sQuery(id+"F0.wireOp",EDGE,"cfcd18ba-fdd5-469c-91bd-894e146aa95b"),sQuery(id+"F0.wireOp",EDGE,"afd42db7-46b9-4924-ba23-a08fdedc66ef"),sQuery(id+"F0.wireOp",EDGE,"fb143438-88c8-4788-8821-21e718cfb00b"),sQuery(id+"F0.wireOp",EDGE,"85c292fa-0e16-4b5d-a30a-18be1996600c"),sQuery(id+"F0.wireOp",EDGE,"ba9f27f5-d96c-40f4-a942-8830aae30a0e"),sQuery(id+"F0.wireOp",EDGE,"772db54a-8b9b-4e0d-9d04-fa1df947a18b"),sQuery(id+"F0.wireOp",EDGE,"9c6c19a0-8f18-4163-9b5e-3a948657e163"),sQuery(id+"F0.wireOp",EDGE,"47dc4b81-4111-4518-8220-22d75ea80592"),sQuery(id+"F0.wireOp",EDGE,"b12d8e1b-5cfd-4479-9421-75358dd440f7"),sQuery(id+"F0.wireOp",EDGE,"e3b0688f-fb9f-4df7-8a1c-6c69eec66f7c"),sQuery(id+"F0.wireOp",EDGE,"56673cb4-c2ff-4ddc-a764-ba91a0c65527"),sQuery(id+"F0.wireOp",EDGE,"b4ff2c96-af1f-44c3-bfcf-f014b856332c"),sQuery(id+"F0.wireOp",EDGE,"eef97820-e528-49c8-9d18-5cad30e9687e"),sQuery(id+"F0.wireOp",EDGE,"b9cbb424-48e6-4987-9ac9-c534665f57a3"),sQuery(id+"F0.wireOp",EDGE,"01f51e96-2d7a-4479-a9be-ba627a86642a"),sQuery(id+"F0.wireOp",EDGE,"69c21511-aab7-4d4f-9314-12972920d45b"),sQuery(id+"F0.wireOp",EDGE,"436ffd40-10bc-437e-a305-7a019e482c66"),sQuery(id+"F0.wireOp",EDGE,"33b36176-ac8f-4457-85b3-2a54d364cf0c"),sQuery(id+"F0.wireOp",EDGE,"0bc01331-38d7-48de-aef1-0b42b3685b72"),sQuery(id+"F0.wireOp",EDGE,"08d8f21f-2e7e-478d-8467-8154c10c2551"),sQuery(id+"F0.wireOp",EDGE,"4d8fcb29-c4ba-4d7a-b196-0818d4bc7f5d"),sQuery(id+"F0.wireOp",EDGE,"edc01665-8ce5-48e2-a884-5b0c2e6a62f1"),sQuery(id+"F0.wireOp",EDGE,"13170063-ef24-40c4-a6cc-f3ef1b29d7be"),sQuery(id+"F0.wireOp",EDGE,"ea421fa7-9d2e-4020-9c5c-427c74a14d84")])]});
            var Q4;
            Q4=makeQuery(id+"F1.opExtrude","SWEPT_BODY",BODY,{"disambiguationData":[OSD([sQuery(id+"F0.wireOp",EDGE,"f8264f38-76e0-493a-aef4-62b8dbf1ef44"),sQuery(id+"F0.wireOp",EDGE,"d8897f10-affa-437c-9764-e51b3f8e4fb5"),sQuery(id+"F0.wireOp",EDGE,"ebf8b383-b9a8-431a-9820-62c749c1b9d9"),sQuery(id+"F0.wireOp",EDGE,"e2816e06-6508-4cc7-b884-6f41445406bf"),sQuery(id+"F0.wireOp",EDGE,"fc5d0cf1-8162-4fc3-acb7-bc6d8a8da133"),sQuery(id+"F0.wireOp",EDGE,"46bf5116-ff26-431c-80e7-f5b44f581864"),sQuery(id+"F0.wireOp",EDGE,"81167a38-bb7d-44d3-9f94-87b2e889fb1a"),sQuery(id+"F0.wireOp",EDGE,"080497b4-9865-4f14-b752-0510f14b5fdb"),sQuery(id+"F0.wireOp",EDGE,"f1e4595e-1cc2-4526-ba90-8bd452b784c5"),sQuery(id+"F0.wireOp",EDGE,"afb072c2-5ed9-4193-a3e7-8909ea57c41c"),sQuery(id+"F0.wireOp",EDGE,"8971ca2a-99a0-4839-b2ca-5443215bc511"),sQuery(id+"F0.wireOp",EDGE,"dccb6175-b576-4c78-9e0b-9ebff6a19a64"),sQuery(id+"F0.wireOp",EDGE,"4a54dae4-934d-46be-8312-796a6487e6ef"),sQuery(id+"F0.wireOp",EDGE,"85b91a2e-3c40-426e-84d6-2563701cfc6c"),sQuery(id+"F0.wireOp",EDGE,"33c3f32e-8e5c-4755-a765-329ba88c8bb7"),sQuery(id+"F0.wireOp",EDGE,"4de21b76-b660-481c-8e4c-19d6af45992a"),sQuery(id+"F0.wireOp",EDGE,"e6cea38e-7f07-48ef-8f73-0ab99a1210f6"),sQuery(id+"F0.wireOp",EDGE,"f31502d5-fc1e-4c9e-a77d-627467fbc7eb"),sQuery(id+"F0.wireOp",EDGE,"f4c4f95d-b029-4d27-b07a-8363059b6d8d"),sQuery(id+"F0.wireOp",EDGE,"d0579631-1e8f-4c22-a40a-e55f1683e7d4"),sQuery(id+"F0.wireOp",EDGE,"ced2008a-de6e-41b8-8516-fb0cce489d81"),sQuery(id+"F0.wireOp",EDGE,"70ce0675-d606-48a0-baa7-191ecdd1761f"),sQuery(id+"F0.wireOp",EDGE,"de6fcb88-4c05-4d6f-a4a8-a49d7c915b99"),sQuery(id+"F0.wireOp",EDGE,"e2c35a7f-3195-4b58-ab43-128dac7b8a54"),sQuery(id+"F0.wireOp",EDGE,"b6bbed9d-981b-4b4b-a50b-dddcf5991096"),sQuery(id+"F0.wireOp",EDGE,"af6f39af-9986-4983-8323-862af6664aa7"),sQuery(id+"F0.wireOp",EDGE,"2536ecd0-8fd4-443d-87d2-e26b2c1ecfea"),sQuery(id+"F0.wireOp",EDGE,"99d9e848-9d33-4a72-8b31-ab048eee31b3"),sQuery(id+"F0.wireOp",EDGE,"cf332e66-b020-4fa5-a5e3-780ec89063b7"),sQuery(id+"F0.wireOp",EDGE,"0a7ca1e3-4fef-4496-bdc9-832b12135c57"),sQuery(id+"F0.wireOp",EDGE,"cf019119-8762-4829-b210-9dd5020cd454"),sQuery(id+"F0.wireOp",EDGE,"5c01ba5f-257d-4158-b2d2-ddb4cba41e60"),sQuery(id+"F0.wireOp",EDGE,"0f108e4b-2557-465b-9f11-ec35a8fff2e6"),sQuery(id+"F0.wireOp",EDGE,"1aacafbf-d299-4384-b4b3-674371db8afd"),sQuery(id+"F0.wireOp",EDGE,"3e854f72-ab69-4580-bd07-726a14d0d7e4"),sQuery(id+"F0.wireOp",EDGE,"12a495ea-355e-4a8f-ade2-e31f4b15c56f"),sQuery(id+"F0.wireOp",EDGE,"df0b72c0-568a-406e-9e39-1cadae64f46f"),sQuery(id+"F0.wireOp",EDGE,"5ddbf886-8df0-4983-8dcb-b448269bf126"),sQuery(id+"F0.wireOp",EDGE,"1e4f65e0-a5bc-423e-b177-d95b3970842f"),sQuery(id+"F0.wireOp",EDGE,"a09cb809-06aa-4f42-af00-5e926e1700a1")])]});
            var Q5;
            Q5=makeQuery(id+"F1.opExtrude","SWEPT_BODY",BODY,{"disambiguationData":[OSD([sQuery(id+"F0.wireOp",EDGE,"85b238a3-1cd6-4965-8cfa-3052cf196f0d"),sQuery(id+"F0.wireOp",EDGE,"70edcf11-fbc5-4599-a71e-9b550eab2f90"),sQuery(id+"F0.wireOp",EDGE,"5a6780af-b702-4be3-afdd-3dca98534a88"),sQuery(id+"F0.wireOp",EDGE,"bae35ea5-85ca-4c89-bdd8-2898bc6a1e68"),sQuery(id+"F0.wireOp",EDGE,"01bb16dc-0673-4a44-83de-c37bc0aa209e"),sQuery(id+"F0.wireOp",EDGE,"7255d6e3-bb35-4340-98a5-1c55be13c511"),sQuery(id+"F0.wireOp",EDGE,"ee4e2727-4cd4-4d0c-8d13-57f2bbc0301d"),sQuery(id+"F0.wireOp",EDGE,"a04b9af4-1979-4680-8793-a24c63298af2"),sQuery(id+"F0.wireOp",EDGE,"146f780b-d1fa-4398-8347-460315796d2c"),sQuery(id+"F0.wireOp",EDGE,"4b62b659-aad4-408b-9277-186feadfaf43"),sQuery(id+"F0.wireOp",EDGE,"913d4862-f2a9-4e08-9746-09ebece39780"),sQuery(id+"F0.wireOp",EDGE,"3ae381d7-7efa-4169-8e5d-3d56b06bd280"),sQuery(id+"F0.wireOp",EDGE,"bc3f93e8-5710-4636-b266-7057c4d39d64"),sQuery(id+"F0.wireOp",EDGE,"54a30c0a-e1f7-4c67-8191-5bfce738994f"),sQuery(id+"F0.wireOp",EDGE,"1af8a38a-8d64-4526-be99-68604aadbfa7"),sQuery(id+"F0.wireOp",EDGE,"6c88c0c8-9c46-4eb2-9bde-14b1b02206fb"),sQuery(id+"F0.wireOp",EDGE,"f47671a0-db6f-4dd8-be4f-8aded57ab578"),sQuery(id+"F0.wireOp",EDGE,"f2fa72e2-7b67-4f99-b215-01f0421dae37"),sQuery(id+"F0.wireOp",EDGE,"2110f30a-bba8-4cdf-a2e2-ac46314e948e"),sQuery(id+"F0.wireOp",EDGE,"d7996510-a69a-4084-ad8c-a72c00f51dfe"),sQuery(id+"F0.wireOp",EDGE,"7c38496c-6790-47e2-a559-613f01789d50"),sQuery(id+"F0.wireOp",EDGE,"02855af9-b67a-4a19-943a-73c938888430"),sQuery(id+"F0.wireOp",EDGE,"94441b53-03fe-4a1f-a9fe-d1992a78a6a7"),sQuery(id+"F0.wireOp",EDGE,"93dd7935-908e-4a76-958e-bb14ae0c67f6"),sQuery(id+"F0.wireOp",EDGE,"14d8fffe-8ab9-4d0b-9dc1-18e0b0667027"),sQuery(id+"F0.wireOp",EDGE,"63c54116-b1a2-4b26-8252-670ede0e7d0a"),sQuery(id+"F0.wireOp",EDGE,"5a47e90a-58d7-43fe-9853-1f9cb66a5e61"),sQuery(id+"F0.wireOp",EDGE,"57215f64-f05b-42fe-9a27-8fb6dbfa4f0a"),sQuery(id+"F0.wireOp",EDGE,"46d0d38d-68f6-4915-b9b9-4b6da60aa98f"),sQuery(id+"F0.wireOp",EDGE,"c1ba83dd-3b30-4382-9a8e-09465e651ef5"),sQuery(id+"F0.wireOp",EDGE,"70a7736d-9afd-41f1-871a-e92eb515e714"),sQuery(id+"F0.wireOp",EDGE,"34261fba-a2c5-40d6-8575-bda6afdd00ca")])]});
            var Q6;
            Q6=makeQuery(id+"F1.opExtrude","SWEPT_BODY",BODY,{"disambiguationData":[OSD([sQuery(id+"F0.wireOp",EDGE,"65e1c758-dbae-4b52-ac89-c4899e5be1b6"),sQuery(id+"F0.wireOp",EDGE,"6fd0cb1d-9cda-4887-98d1-188edc325bba"),sQuery(id+"F0.wireOp",EDGE,"b63dcb22-cdc6-459d-8258-5d11f2a21b64"),sQuery(id+"F0.wireOp",EDGE,"238f7e32-69f7-439e-8c3f-d5b2fca109d1"),sQuery(id+"F0.wireOp",EDGE,"eaccb499-a832-4193-9241-1820b82b02ae"),sQuery(id+"F0.wireOp",EDGE,"8f5315dd-865b-4b8f-854e-f0be736f4d01"),sQuery(id+"F0.wireOp",EDGE,"d743e7e8-76e2-4366-adf2-4b7635e813d6"),sQuery(id+"F0.wireOp",EDGE,"80638b0b-a855-4703-9f04-e4721920dbfa"),sQuery(id+"F0.wireOp",EDGE,"11277302-57ab-4fb1-810d-7ab629cf953a"),sQuery(id+"F0.wireOp",EDGE,"7d8c8dd7-6264-4372-a371-ef4d35750084"),sQuery(id+"F0.wireOp",EDGE,"a4e5db81-dec4-41e6-8cd4-ba84cb84489b"),sQuery(id+"F0.wireOp",EDGE,"a45b2837-c160-45a1-a3ab-14e6d80dc04f"),sQuery(id+"F0.wireOp",EDGE,"7e8a8949-ef33-412b-803e-79ee4ab58fe1"),sQuery(id+"F0.wireOp",EDGE,"a638f4b8-450f-426d-82dd-fc4e6d093d95"),sQuery(id+"F0.wireOp",EDGE,"76ebcb0d-1716-49a7-bf6b-ccac2a9c7c2b"),sQuery(id+"F0.wireOp",EDGE,"0ba12e77-94d9-4bf8-9d25-edd8eeb623e6"),sQuery(id+"F0.wireOp",EDGE,"a247a5f8-7273-47ac-92f8-db608fcdc2a2"),sQuery(id+"F0.wireOp",EDGE,"af3f62ef-aa4c-4107-a732-7e5039f71f50"),sQuery(id+"F0.wireOp",EDGE,"e4175979-e9bf-4a8d-85c2-a2a5a119980f"),sQuery(id+"F0.wireOp",EDGE,"1fde1c44-c2ab-41d5-813c-a697ea59fc9f"),sQuery(id+"F0.wireOp",EDGE,"f1619ab8-78c8-4f7b-86e9-77cd9515e302"),sQuery(id+"F0.wireOp",EDGE,"1f2e3aff-d41e-438e-ba2a-0905688e443b"),sQuery(id+"F0.wireOp",EDGE,"bcf3dbe1-711a-41b9-8464-bb562f66deec"),sQuery(id+"F0.wireOp",EDGE,"1da650cd-9852-471b-befe-912197337acb"),sQuery(id+"F0.wireOp",EDGE,"541591e6-93c5-4ed9-a47d-d0f5f5540662"),sQuery(id+"F0.wireOp",EDGE,"599c93b8-85ec-4fe5-af88-17749cdfc58f"),sQuery(id+"F0.wireOp",EDGE,"2c374f98-06e7-475a-9abd-4d0ae29f07b1"),sQuery(id+"F0.wireOp",EDGE,"250285ac-59aa-42e8-b82d-edf32f8e71ab"),sQuery(id+"F0.wireOp",EDGE,"5beca186-5c3a-489c-904f-7fbfd7f2e08a"),sQuery(id+"F0.wireOp",EDGE,"06a673dd-3b56-423a-8f4e-3421e38e8780"),sQuery(id+"F0.wireOp",EDGE,"c2b7b29b-a481-478e-a8e7-92f43f83adfb"),sQuery(id+"F0.wireOp",EDGE,"764a73a9-e478-4a54-9631-e927ed2e01e8")])]});
            var Q7;
            Q7=qCreatedBy(makeId("Origin.pointOp"),VERTEX);
            transform(context, id + "F2", {"entities" : qUnion([Q0, Q1, Q2, Q3, Q4, Q5, Q6]), "transformType" : TransformType.SCALE_UNIFORMLY, "scale" : 10, "scalePoint" : qUnion([Q7]), "makeCopy" : false});
        }
        {
            var Q0;
            Q0=qCreatedBy(makeId("Top.planeOp"),FACE);
            cPlane(context, id + "F3", {"entities" : qUnion([Q0]), "cplaneType" : CPlaneType.OFFSET, "offset" : 2 * mm, "width" : 150 * mm, "height" : 150 * mm});
        }
        {
            var Q0;
            Q0=qCreatedBy(id+"F3.planeOp",FACE);
            var sketch = newSketch(context, id + "F4", { "sketchPlane" : qUnion([Q0])});
            skLineSegment(sketch, "E1.bottom", {"start": v(-30, -30) * mm, "end": v(30, -30) * mm});
            skLineSegment(sketch, "E1.top", {"start": v(-30, 30) * mm, "end": v(30, 30) * mm});
            skLineSegment(sketch, "E1.left", {"start": v(-30, -30) * mm, "end": v(-30, 30) * mm});
            skLineSegment(sketch, "E1.right", {"start": v(30, -30) * mm, "end": v(30, 30) * mm});
            skSolve(sketch);
        }
        {
            var Q0;
            Q0 = qSketchRegion(id + "F4", true);
            extrude(context, id + "F5", {"entities" : qUnion([Q0]), "oppositeDirection" : true, "depth" : 2.5 * mm, "offsetDistance" : 25 * mm, "hasSecondDirection" : true, "secondDirectionOppositeDirection" : true, "secondDirectionDepth" : 2 * mm});
        }
        {
            var Q0;
            Q0=makeQuery(id+"F1.opExtrude","SWEPT_BODY",BODY,{"disambiguationData":[OSD([sQuery(id+"F0.wireOp",EDGE,"E0.bottom"),sQuery(id+"F0.wireOp",EDGE,"E0.top"),sQuery(id+"F0.wireOp",EDGE,"E0.left"),sQuery(id+"F0.wireOp",EDGE,"E0.right"),sQuery(id+"F0.wireOp",EDGE,"3ec7afe0-a1e0-457c-be4a-088452004a96"),sQuery(id+"F0.wireOp",EDGE,"d83f218b-7086-4efd-8b13-d209db19827c"),sQuery(id+"F0.wireOp",EDGE,"02d8bd81-b223-4a02-9b2f-538ae8beb5a6"),sQuery(id+"F0.wireOp",EDGE,"2d902582-cd20-4641-8568-96b7fb684a02"),sQuery(id+"F0.wireOp",EDGE,"f5096a21-a806-46d9-b6c2-ae8de96a788b"),sQuery(id+"F0.wireOp",EDGE,"3b47cd1d-8fba-4731-8d0e-cda14d99b06e"),sQuery(id+"F0.wireOp",EDGE,"41564daa-fe03-4dbd-9e56-aa0510e19988"),sQuery(id+"F0.wireOp",EDGE,"02388e9d-f7fc-4dad-9147-57d1375461ec"),sQuery(id+"F0.wireOp",EDGE,"22264fa0-5d3e-4774-86a0-50946ccf6ead"),sQuery(id+"F0.wireOp",EDGE,"a467128b-4a78-4aa8-9340-e2e247e980d2"),sQuery(id+"F0.wireOp",EDGE,"1619cbc9-05f0-4f5a-8f65-62f3c9434277"),sQuery(id+"F0.wireOp",EDGE,"99e10741-56a3-4363-82b4-1b7282e7ca4c"),sQuery(id+"F0.wireOp",EDGE,"24693340-a1d5-4308-b41e-ebabe64e6a8c"),sQuery(id+"F0.wireOp",EDGE,"64b93bc5-bd2d-41f4-a006-fbb3c3e2de2e"),sQuery(id+"F0.wireOp",EDGE,"55426dc8-b2e5-4f94-be62-9a8d58c9ab38"),sQuery(id+"F0.wireOp",EDGE,"5bce8405-4400-4a37-8856-f7f68e24ea4c"),sQuery(id+"F0.wireOp",EDGE,"c21bd593-22bc-4b69-8e4e-1fb222cef98b"),sQuery(id+"F0.wireOp",EDGE,"f8c3e9e9-656d-4477-9170-02d9ece8e834"),sQuery(id+"F0.wireOp",EDGE,"8a779292-eed6-45a9-b757-0a415a321d37"),sQuery(id+"F0.wireOp",EDGE,"5f832a96-d78e-4e74-b481-aab9e5c15b8e"),sQuery(id+"F0.wireOp",EDGE,"430f9e32-9bfc-4471-b983-62e587525792"),sQuery(id+"F0.wireOp",EDGE,"9e28f7ca-141b-4c07-b7ad-4c5ca4b71de8"),sQuery(id+"F0.wireOp",EDGE,"7ab17df3-aba0-41db-9353-0b5ccab53e5f"),sQuery(id+"F0.wireOp",EDGE,"e171d48b-26fe-4f5a-a888-7f954c3a5218"),sQuery(id+"F0.wireOp",EDGE,"e79f6706-141e-4c0d-adc8-7167a5aa39dc"),sQuery(id+"F0.wireOp",EDGE,"c8e1bd4d-aee9-41e8-ade3-5be9cbb654e8"),sQuery(id+"F0.wireOp",EDGE,"47d54f73-4b4e-483b-a749-b05e58b45576"),sQuery(id+"F0.wireOp",EDGE,"7973314d-2740-4cf3-b868-1b8a999ba722"),sQuery(id+"F0.wireOp",EDGE,"720fcdf6-7b9d-4216-8e72-eb40a41dce0a"),sQuery(id+"F0.wireOp",EDGE,"d29978c5-a1be-4d4b-8944-da0213377966"),sQuery(id+"F0.wireOp",EDGE,"e5daffcd-b5ce-4dea-ac11-20f20ff523b4"),sQuery(id+"F0.wireOp",EDGE,"50641089-9504-40b9-8477-96adc3d40a89"),sQuery(id+"F0.wireOp",EDGE,"6d270dd2-b7c0-458e-a9ee-65726ff07b0c"),sQuery(id+"F0.wireOp",EDGE,"b3e48804-5e06-4876-8223-ffe42bf3636a"),sQuery(id+"F0.wireOp",EDGE,"63cc2df1-c457-4d14-b5f3-d92c72be0608"),sQuery(id+"F0.wireOp",EDGE,"811def09-c990-4daf-ba8c-b148da244ebc"),sQuery(id+"F0.wireOp",EDGE,"4d1e2a3c-fd62-4d4c-bcf6-9f666ab0c452"),sQuery(id+"F0.wireOp",EDGE,"81fce658-763d-4a5d-a611-0a742473717a"),sQuery(id+"F0.wireOp",EDGE,"f822a7c1-ac77-462a-b5c0-4338f93c980d"),sQuery(id+"F0.wireOp",EDGE,"f1bb49a8-6e90-4657-99b0-fe3ee6e9b850"),sQuery(id+"F0.wireOp",EDGE,"62310ddd-0304-494f-90b3-e6686b61077f"),sQuery(id+"F0.wireOp",EDGE,"c2033112-2bf2-40f2-861c-00d87bee8627"),sQuery(id+"F0.wireOp",EDGE,"14c75d5e-7332-4c27-bd92-261d4fd848ba"),sQuery(id+"F0.wireOp",EDGE,"22950e56-f2bd-479b-ad15-ca8860f234eb"),sQuery(id+"F0.wireOp",EDGE,"0c1f7b48-368b-462f-880e-93a51e1aa555"),sQuery(id+"F0.wireOp",EDGE,"b5a827ad-50b1-4835-9a05-472a480554c8"),sQuery(id+"F0.wireOp",EDGE,"44def7af-5edd-4bc8-b590-da631150d928"),sQuery(id+"F0.wireOp",EDGE,"5b539bd8-9961-45a0-92ed-a386129d0a0b"),sQuery(id+"F0.wireOp",EDGE,"e7b18de2-00d5-44c6-b284-184d2c0b6658"),sQuery(id+"F0.wireOp",EDGE,"d9bf9977-81ab-4193-b2fa-4848e88f6ea1"),sQuery(id+"F0.wireOp",EDGE,"5ebeac3d-4b27-4cb7-bf5d-219251f9516b"),sQuery(id+"F0.wireOp",EDGE,"a416a0db-305d-478f-8e7c-7a8594db7948"),sQuery(id+"F0.wireOp",EDGE,"5670b267-cfff-421d-b539-6a539cfda789"),sQuery(id+"F0.wireOp",EDGE,"3dac470b-4319-4a66-ae29-b8d3f215b9bd"),sQuery(id+"F0.wireOp",EDGE,"03b27164-48bf-4732-9087-733abdd1034d"),sQuery(id+"F0.wireOp",EDGE,"8120ee63-c910-4b66-ac7d-0f760dbf99e2"),sQuery(id+"F0.wireOp",EDGE,"c9e787c0-baf7-46a9-b42b-2670cd472db3"),sQuery(id+"F0.wireOp",EDGE,"851d0d47-70d4-462b-aa0f-03065de4ac0c"),sQuery(id+"F0.wireOp",EDGE,"e77e26e9-0bc8-48ac-b61c-24ad1caf3c9c"),sQuery(id+"F0.wireOp",EDGE,"d6e28216-d606-4f2b-8d32-bb6ccec41566"),sQuery(id+"F0.wireOp",EDGE,"8c67bd25-36d2-4afe-bd64-c387e52d00c2"),sQuery(id+"F0.wireOp",EDGE,"e4aac0d1-a521-48c7-9d6c-724ae50099b9"),sQuery(id+"F0.wireOp",EDGE,"61536177-4917-47db-bde2-8d2a4f733d81"),sQuery(id+"F0.wireOp",EDGE,"47ab3f07-b9b0-4f7d-aaf9-d7cfa683d4aa"),sQuery(id+"F0.wireOp",EDGE,"72710534-632b-4c55-849d-ec722133dbc1"),sQuery(id+"F0.wireOp",EDGE,"5e43d561-e149-44a2-9fca-b4b008a3a7d6"),sQuery(id+"F0.wireOp",EDGE,"9279be7f-0be9-4663-98e7-e996f2be473d"),sQuery(id+"F0.wireOp",EDGE,"c44d038a-da18-41ec-8afa-1d1866d1f861"),sQuery(id+"F0.wireOp",EDGE,"e3798a42-469f-46b9-9ab3-bacfc8b42f00"),sQuery(id+"F0.wireOp",EDGE,"f034fc37-7e18-494d-834f-c8e07136fe97"),sQuery(id+"F0.wireOp",EDGE,"ffba7b79-0caf-4550-9ef0-48fd2c2eedc0"),sQuery(id+"F0.wireOp",EDGE,"f7a3de90-2f3c-43dc-9883-e84d532b549c"),sQuery(id+"F0.wireOp",EDGE,"c750c932-4bbb-417d-bdea-0f72397a7019"),sQuery(id+"F0.wireOp",EDGE,"a3412e4e-3ed4-4017-94ce-3c13780d5bf9"),sQuery(id+"F0.wireOp",EDGE,"f6e69c40-12d3-4752-8b7f-c0431ab5c846"),sQuery(id+"F0.wireOp",EDGE,"767176a0-43e3-4645-a59e-1272894fbf7a"),sQuery(id+"F0.wireOp",EDGE,"6f2bbe3a-c317-49b8-94a2-a87eb011ea02"),sQuery(id+"F0.wireOp",EDGE,"a1520ac8-22ba-49e5-93e5-20ceff7b8af7"),sQuery(id+"F0.wireOp",EDGE,"cb4930a2-9a3a-4684-ab62-77c10cece2a2"),sQuery(id+"F0.wireOp",EDGE,"20b6dfe0-11c6-493f-8d24-8f66077ccf5c"),sQuery(id+"F0.wireOp",EDGE,"2ca8a1b8-9df9-411f-8d1c-6445228a5ca8"),sQuery(id+"F0.wireOp",EDGE,"699309a4-edb1-411f-8ef3-7794c42be602"),sQuery(id+"F0.wireOp",EDGE,"bd74286a-29d0-4114-a072-0032613366e6"),sQuery(id+"F0.wireOp",EDGE,"fc658b50-a5ca-4d86-a88e-b76cf9467b0b"),sQuery(id+"F0.wireOp",EDGE,"27fdd899-d6b1-4d30-8442-3c03dd78eba2"),sQuery(id+"F0.wireOp",EDGE,"440f6f4a-16b8-4354-8233-1d1744525dae"),sQuery(id+"F0.wireOp",EDGE,"3d98288c-f389-4f90-9d39-60cb79a00bb8"),sQuery(id+"F0.wireOp",EDGE,"f79bcbc1-5df4-4b7b-80fa-43563f779b76"),sQuery(id+"F0.wireOp",EDGE,"1051ae6e-5939-4fe6-8811-fbc80e0b9638"),sQuery(id+"F0.wireOp",EDGE,"76698742-e0db-49a3-82d9-61ed44e431b8"),sQuery(id+"F0.wireOp",EDGE,"ba61a141-cac1-4778-9c9e-74bcd335542e"),sQuery(id+"F0.wireOp",EDGE,"81f51e81-3098-4b38-81a7-bde5e4d849b4"),sQuery(id+"F0.wireOp",EDGE,"c7cc50c0-9e9f-467a-9f0c-185cd03e4846"),sQuery(id+"F0.wireOp",EDGE,"3275c11a-791a-4694-a09e-df3df0d70a3d"),sQuery(id+"F0.wireOp",EDGE,"bc3e4385-77d7-4447-8bec-42d880316bfd"),sQuery(id+"F0.wireOp",EDGE,"ea27d34e-d2f1-4b3e-92c9-6e89909bea16"),sQuery(id+"F0.wireOp",EDGE,"379d4164-5f7a-4c05-baa5-cc58e4694ce7"),sQuery(id+"F0.wireOp",EDGE,"1062bfd7-c4fc-4b28-b988-7fe4492de22f"),sQuery(id+"F0.wireOp",EDGE,"fc213567-08de-486d-b4ca-ff95bb5b6401"),sQuery(id+"F0.wireOp",EDGE,"a14c394f-738c-49f1-a45f-159cd0637914"),sQuery(id+"F0.wireOp",EDGE,"166781b6-f08b-48b1-bac9-12c9ea3421ab"),sQuery(id+"F0.wireOp",EDGE,"35f9fbb9-e8a9-44e7-8893-e82d580ff6ca"),sQuery(id+"F0.wireOp",EDGE,"d55b8e85-21c7-4f06-b75f-d413d399493a"),sQuery(id+"F0.wireOp",EDGE,"f78b1f4a-3af2-4aca-b1f1-9c95252bd1fc"),sQuery(id+"F0.wireOp",EDGE,"8ff1015e-a657-4219-b192-62bd4060579d"),sQuery(id+"F0.wireOp",EDGE,"712e7e8e-a0b3-4a78-b3cf-5035268c3b1b"),sQuery(id+"F0.wireOp",EDGE,"dd7306b4-5a59-4d03-b176-b2ecc48ed0c9"),sQuery(id+"F0.wireOp",EDGE,"a4f7c66e-2dea-453d-a349-4ee5712a776d"),sQuery(id+"F0.wireOp",EDGE,"eee453a0-aeb0-49ac-a5a0-f2e9f7f4152a"),sQuery(id+"F0.wireOp",EDGE,"b8c53693-8c12-4e66-8b60-6595c828f9ef"),sQuery(id+"F0.wireOp",EDGE,"ba798e71-e747-4192-bb8a-8c61b35e6316"),sQuery(id+"F0.wireOp",EDGE,"e1604eea-9b7d-491b-83e4-51499261206a"),sQuery(id+"F0.wireOp",EDGE,"bc5efcf9-bb2f-4e29-a1ca-58298c4f8a7b"),sQuery(id+"F0.wireOp",EDGE,"6319af28-edc9-4555-9ad3-ebef588b88ae"),sQuery(id+"F0.wireOp",EDGE,"2e15575d-92d4-45b8-aba9-d4b5887d4759"),sQuery(id+"F0.wireOp",EDGE,"593a8dbb-b7b4-4bd3-9e56-5ac97cc9a1ec"),sQuery(id+"F0.wireOp",EDGE,"02380fbd-832a-4dc9-aae5-dbf10ebaaf3d"),sQuery(id+"F0.wireOp",EDGE,"13981ab7-9961-4e34-9086-dceaa1c7b3be"),sQuery(id+"F0.wireOp",EDGE,"3a046d59-f46e-467a-9278-2a68960cf58b"),sQuery(id+"F0.wireOp",EDGE,"a75f2866-233f-4df0-b6f9-14dd6b91b060"),sQuery(id+"F0.wireOp",EDGE,"f2732e12-788a-45ca-9c56-273da7a29a0e"),sQuery(id+"F0.wireOp",EDGE,"8ee60f07-1099-4ca2-9ebe-5424af49e3b5"),sQuery(id+"F0.wireOp",EDGE,"4f58ddd7-5aa5-438a-b942-bca2248868eb"),sQuery(id+"F0.wireOp",EDGE,"ea4bc371-bac6-43d1-8ec8-77b3c77d1d08"),sQuery(id+"F0.wireOp",EDGE,"fabef4ac-eedc-4238-adcb-865e221dc712"),sQuery(id+"F0.wireOp",EDGE,"c34c20a1-9834-4408-bf79-1be559bfa9ba"),sQuery(id+"F0.wireOp",EDGE,"5e8330d4-b02b-4a67-8497-a16df57a01fc"),sQuery(id+"F0.wireOp",EDGE,"1ce77aba-b302-47d2-8b68-c2e856514517"),sQuery(id+"F0.wireOp",EDGE,"834b12ab-1ad9-49dd-b164-8d70879f156f"),sQuery(id+"F0.wireOp",EDGE,"bed03741-100b-4911-8924-3d714ec53786"),sQuery(id+"F0.wireOp",EDGE,"f5ef7e46-89d9-4f7d-8693-a5c8aed4e8d6"),sQuery(id+"F0.wireOp",EDGE,"3f11fecd-cc23-4907-9c92-c85356b89d33"),sQuery(id+"F0.wireOp",EDGE,"5e1d7c4c-f824-4253-95c8-758a53e5f7d8"),sQuery(id+"F0.wireOp",EDGE,"81e188b5-2422-419b-9d61-c4ff843a2b7d"),sQuery(id+"F0.wireOp",EDGE,"e9228d95-9eeb-42dc-909a-163fbb938afe"),sQuery(id+"F0.wireOp",EDGE,"959069a5-4158-4b4e-aaea-50d8de0d1250"),sQuery(id+"F0.wireOp",EDGE,"50333e4b-2514-429b-8c4f-ca88dfc82600"),sQuery(id+"F0.wireOp",EDGE,"075de889-d11b-4e8b-9c31-040acac3b58d"),sQuery(id+"F0.wireOp",EDGE,"c7c70318-40be-436f-b5fd-08fe0706d55e"),sQuery(id+"F0.wireOp",EDGE,"5723ddac-3b46-4be1-afdb-4c7638558a6f"),sQuery(id+"F0.wireOp",EDGE,"d590f57a-681e-43fc-ad37-4c356b537c3a"),sQuery(id+"F0.wireOp",EDGE,"f6af2cb9-de3d-4e7c-866f-a3e7c472d7b8"),sQuery(id+"F0.wireOp",EDGE,"b6c00460-730a-4222-a33a-3643a2ef3fe4"),sQuery(id+"F0.wireOp",EDGE,"827ff635-27c5-4321-831d-4920dab6c213"),sQuery(id+"F0.wireOp",EDGE,"38421385-35fb-40d3-bf68-990b4a57970c"),sQuery(id+"F0.wireOp",EDGE,"18ad6ecc-b386-4713-bde1-9b9bd5a2318a"),sQuery(id+"F0.wireOp",EDGE,"0711714c-1d40-418f-8cd7-8681d9630629"),sQuery(id+"F0.wireOp",EDGE,"98796be2-b74d-4e80-bb13-dd88d4f5ec73"),sQuery(id+"F0.wireOp",EDGE,"88c95ccb-a92a-4622-ad8b-6e7e745f93e2"),sQuery(id+"F0.wireOp",EDGE,"e3605e1b-24de-43cc-8fe1-493b685f07a9"),sQuery(id+"F0.wireOp",EDGE,"f781a5ef-2e9d-4487-aa95-33630d70acaa"),sQuery(id+"F0.wireOp",EDGE,"fd6c0f24-dea2-4d7b-a979-02eed4e90b37"),sQuery(id+"F0.wireOp",EDGE,"05fbe2cf-c617-47ae-a1cf-4fe9e66abefc"),sQuery(id+"F0.wireOp",EDGE,"7a299a4e-a918-4890-99c3-7a67ee3f4166"),sQuery(id+"F0.wireOp",EDGE,"0a5a90e0-eb3c-4e0d-ab2a-89f6e7f68dfe"),sQuery(id+"F0.wireOp",EDGE,"70afa412-88dc-4f5e-a859-925588698aba"),sQuery(id+"F0.wireOp",EDGE,"2913be52-9a0c-4146-a4c9-76e64dcde4e6"),sQuery(id+"F0.wireOp",EDGE,"d0417cf6-5bfb-45b9-a084-899a6a988cf6"),sQuery(id+"F0.wireOp",EDGE,"2538756b-0ef2-41bd-b8c8-6d272a99fe31"),sQuery(id+"F0.wireOp",EDGE,"0198ab2a-8068-43de-bfce-0b2b70d5decd"),sQuery(id+"F0.wireOp",EDGE,"31aaf3f3-bc7b-4674-810a-75f22c7ab986"),sQuery(id+"F0.wireOp",EDGE,"8fe21c58-7b24-4e10-9c93-26b82d9e6d21"),sQuery(id+"F0.wireOp",EDGE,"3a426131-fa73-4696-ac6e-bdb9b449d5ce"),sQuery(id+"F0.wireOp",EDGE,"03eeec74-ae2a-46bb-9ee7-4ceb3502b2a6"),sQuery(id+"F0.wireOp",EDGE,"618a0795-a880-4c47-997d-98bac031e887"),sQuery(id+"F0.wireOp",EDGE,"3ad50032-8811-49f1-96ac-81b191064997"),sQuery(id+"F0.wireOp",EDGE,"496fcda9-6dd8-4934-baf7-14d3f409cee7"),sQuery(id+"F0.wireOp",EDGE,"692feb32-5741-4b3b-9193-cd2f3880199d"),sQuery(id+"F0.wireOp",EDGE,"859ace9e-6eac-4f18-a080-abca9f5452dc"),sQuery(id+"F0.wireOp",EDGE,"0a587952-0d6a-4492-addb-1eb97c7d4114"),sQuery(id+"F0.wireOp",EDGE,"c014b403-4438-4a75-9310-698630d0f26c"),sQuery(id+"F0.wireOp",EDGE,"e4c50579-3f17-4124-8f98-613c4078bb63"),sQuery(id+"F0.wireOp",EDGE,"510b368e-4dd2-421a-a9d0-86b946da967d"),sQuery(id+"F0.wireOp",EDGE,"651565fc-69bc-4961-b2b7-ef0527e41ecc"),sQuery(id+"F0.wireOp",EDGE,"23e80a2d-6976-4a1c-a60a-a5e4b68532fd"),sQuery(id+"F0.wireOp",EDGE,"a6ad6e05-5a2c-4e61-9f80-cdbf757a204d"),sQuery(id+"F0.wireOp",EDGE,"3e5aa7f2-2fc2-4aac-a952-e5bcad74a832"),sQuery(id+"F0.wireOp",EDGE,"df52b165-db6a-4f60-bffd-e9240c9c772f"),sQuery(id+"F0.wireOp",EDGE,"c3733b21-a760-48e9-a77a-88576df8cad6"),sQuery(id+"F0.wireOp",EDGE,"ec350596-bf51-4731-b449-2f407bf6303f"),sQuery(id+"F0.wireOp",EDGE,"70cc3cca-0fee-441a-b4d7-96843ff51759"),sQuery(id+"F0.wireOp",EDGE,"c3d1a2ba-bd2a-49b8-bea6-459ef0d2576b"),sQuery(id+"F0.wireOp",EDGE,"23c7a7ae-7321-47e6-a06e-f4653b5178e5"),sQuery(id+"F0.wireOp",EDGE,"e487ad68-183a-4f24-9bd6-de54da96e15a"),sQuery(id+"F0.wireOp",EDGE,"5fa12f74-eda4-4c68-af2c-a4252f408fd3"),sQuery(id+"F0.wireOp",EDGE,"155640c1-ebf2-4dfb-8ef7-75cccd395f21"),sQuery(id+"F0.wireOp",EDGE,"e6ac35a8-d854-4e89-9e33-bea3e269d9a9"),sQuery(id+"F0.wireOp",EDGE,"cb9e2b8c-6de3-4701-937a-1e5628a11478"),sQuery(id+"F0.wireOp",EDGE,"e6808a8c-d175-4686-93c2-d832b162152e"),sQuery(id+"F0.wireOp",EDGE,"356ed25e-81ff-40a8-9200-19a22ad69f1a"),sQuery(id+"F0.wireOp",EDGE,"3b75a134-16d4-4a6b-bad6-df067ae33d35"),sQuery(id+"F0.wireOp",EDGE,"6826a5ab-7ce6-4ac5-b70b-e668ad123194"),sQuery(id+"F0.wireOp",EDGE,"4d99424e-51b7-426f-8c94-c72b14d11e31"),sQuery(id+"F0.wireOp",EDGE,"d860b5f2-e0dd-40a9-8acd-6e3a757f8406"),sQuery(id+"F0.wireOp",EDGE,"39f266b8-2d6b-452a-a185-b1af436a92a6"),sQuery(id+"F0.wireOp",EDGE,"31866575-b77f-4788-8f5d-84bcd0349519"),sQuery(id+"F0.wireOp",EDGE,"5d551245-3a28-4603-9d08-9c0ccb735e6d"),sQuery(id+"F0.wireOp",EDGE,"9b0dd94d-059d-4297-8c38-4640a45fed80"),sQuery(id+"F0.wireOp",EDGE,"2920166d-42de-4cff-aff8-3d29da85a708"),sQuery(id+"F0.wireOp",EDGE,"38e33062-00b2-423a-9adf-0dbdc295fc21"),sQuery(id+"F0.wireOp",EDGE,"817ef9cf-887c-4d38-8025-1a9fee5b0c85"),sQuery(id+"F0.wireOp",EDGE,"4d48468a-d922-400c-add1-5cda9d138ebd"),sQuery(id+"F0.wireOp",EDGE,"ff677f1f-a331-463e-ad12-0f0b2d816477"),sQuery(id+"F0.wireOp",EDGE,"0fe15785-9fea-410f-ad1f-32f88843b595"),sQuery(id+"F0.wireOp",EDGE,"8d09f6c3-07f2-4eb2-aa7f-694363c195a6"),sQuery(id+"F0.wireOp",EDGE,"ec3514e2-3f68-4b88-aecf-a0ee5f06dbea"),sQuery(id+"F0.wireOp",EDGE,"19cb8244-8a3e-4d20-b4f2-7ecd0c712cb2"),sQuery(id+"F0.wireOp",EDGE,"d1091000-42f3-4bcd-9e7a-0692b83df9ec"),sQuery(id+"F0.wireOp",EDGE,"3b397f38-0c49-45a4-a347-98b3a47d70fb"),sQuery(id+"F0.wireOp",EDGE,"d3a4285d-9d01-49b4-b990-b3f73cc7f7e6"),sQuery(id+"F0.wireOp",EDGE,"eed04ee1-c9da-4961-a22d-363b71bae0c2"),sQuery(id+"F0.wireOp",EDGE,"c6171e94-0cba-4356-a26f-247245c8c466"),sQuery(id+"F0.wireOp",EDGE,"6c7643e3-9710-4967-95d2-9ba02bf7ea3e"),sQuery(id+"F0.wireOp",EDGE,"a5f0d80a-626b-4f41-820c-24ba71a7cde6"),sQuery(id+"F0.wireOp",EDGE,"275f012e-7d73-4b9e-b8af-7366cfb6fb08"),sQuery(id+"F0.wireOp",EDGE,"dda7959b-0520-412b-a0df-24aa169fb8fa"),sQuery(id+"F0.wireOp",EDGE,"bd6a2b4a-0797-431f-b7b7-b4e64eae0bb1"),sQuery(id+"F0.wireOp",EDGE,"a1529b2f-f819-429b-97a1-27107fec5de5"),sQuery(id+"F0.wireOp",EDGE,"56fb065c-a381-4615-8b32-7e704d515f56"),sQuery(id+"F0.wireOp",EDGE,"3a80e261-097b-466e-b523-ebbeb2b08257"),sQuery(id+"F0.wireOp",EDGE,"aad8cfd8-81ef-4e44-8af1-503e01a83ad9"),sQuery(id+"F0.wireOp",EDGE,"384a4556-9810-4801-9165-3d7c89c49f93"),sQuery(id+"F0.wireOp",EDGE,"e80a3cc5-1d65-4b1f-a697-de30cccef087"),sQuery(id+"F0.wireOp",EDGE,"beb5745a-8d9d-4c3f-9ca8-9fae599df75e"),sQuery(id+"F0.wireOp",EDGE,"e636cc4a-5226-4be0-a810-a5596ba0a380"),sQuery(id+"F0.wireOp",EDGE,"11aa103c-fcc8-4654-b695-160f80f03844"),sQuery(id+"F0.wireOp",EDGE,"13544508-c267-4dfe-b823-0fcb28622b0a"),sQuery(id+"F0.wireOp",EDGE,"32665112-ab27-4cdc-b08d-6fbfa26e143d"),sQuery(id+"F0.wireOp",EDGE,"64d7f8b8-0fad-4658-a91b-32d9fbade6e0"),sQuery(id+"F0.wireOp",EDGE,"693aa929-2a0d-4d07-b657-d91b5e5a50a4"),sQuery(id+"F0.wireOp",EDGE,"562a9f06-3999-4e31-92ba-a9bce39a5457"),sQuery(id+"F0.wireOp",EDGE,"3550bb31-bca9-4bce-b05e-749f01d8052d"),sQuery(id+"F0.wireOp",EDGE,"bbf2bd7e-b04a-49ad-87d0-94be879a1fd7"),sQuery(id+"F0.wireOp",EDGE,"1fad1780-c111-45d6-814f-8d3daf33c57c"),sQuery(id+"F0.wireOp",EDGE,"46bed204-b29f-48ce-927f-8664db11d61a"),sQuery(id+"F0.wireOp",EDGE,"f0a3a87c-a356-4ed7-9ea9-3fe54c8eb788"),sQuery(id+"F0.wireOp",EDGE,"488fb58e-355f-4e3c-b1e7-120df6e007f1"),sQuery(id+"F0.wireOp",EDGE,"057317ff-4fa0-403f-9dcc-5dd07fa112e6"),sQuery(id+"F0.wireOp",EDGE,"776f4298-1da3-4d88-ad34-446ef64a6436"),sQuery(id+"F0.wireOp",EDGE,"05d2f769-4c8d-45ba-a53f-3ee7aa0143e9"),sQuery(id+"F0.wireOp",EDGE,"3acd6a5d-3e6a-44c9-add7-099d0dc45fd1"),sQuery(id+"F0.wireOp",EDGE,"99ef3a0c-bd7a-43b8-874e-5091dcbb12c6"),sQuery(id+"F0.wireOp",EDGE,"a745c91b-db9b-4d60-9eba-4c8d32b1ce48"),sQuery(id+"F0.wireOp",EDGE,"ae27dad9-0eac-4b26-995c-815bc9562704"),sQuery(id+"F0.wireOp",EDGE,"b1f83ba6-ca34-49e5-be1d-05832cf887cd"),sQuery(id+"F0.wireOp",EDGE,"8d0cbd76-b6bd-4cb3-a90e-8176a7b89b0b"),sQuery(id+"F0.wireOp",EDGE,"e28f3772-e90c-4ccd-a8f7-2999747c42b9"),sQuery(id+"F0.wireOp",EDGE,"d087fa0c-7451-4ade-9ee1-dc5deba4127e"),sQuery(id+"F0.wireOp",EDGE,"305cecbe-32df-4af8-9aa8-eb6e0cbefc33"),sQuery(id+"F0.wireOp",EDGE,"b276f448-4e9e-4b86-8792-3961f9ade319"),sQuery(id+"F0.wireOp",EDGE,"adf8b33b-826a-4871-b007-8920910c91b7"),sQuery(id+"F0.wireOp",EDGE,"dc45c407-1dac-4814-b0fc-ab15237525e3"),sQuery(id+"F0.wireOp",EDGE,"89c15a6f-255b-4596-a352-01cb142e8ea3"),sQuery(id+"F0.wireOp",EDGE,"891983f6-cd49-4685-b1c2-6261785afe29"),sQuery(id+"F0.wireOp",EDGE,"195d7b5e-cf70-4873-a130-775555191c23"),sQuery(id+"F0.wireOp",EDGE,"161664fa-06e0-4b53-aa7c-47aebda18fc0"),sQuery(id+"F0.wireOp",EDGE,"13462a86-41b2-4154-bb45-709530ddebf9"),sQuery(id+"F0.wireOp",EDGE,"1048e858-88a8-4d62-b03b-009175f937ff"),sQuery(id+"F0.wireOp",EDGE,"88706604-e75d-43fd-bb66-8c5ebd036529"),sQuery(id+"F0.wireOp",EDGE,"6223e2d5-1c3d-4484-9c8a-7c924faae836"),sQuery(id+"F0.wireOp",EDGE,"3f74fce0-9d09-47ec-b53f-1c2d4db3a1ab"),sQuery(id+"F0.wireOp",EDGE,"ddd09eff-a1ba-477a-987a-56e31009e4af"),sQuery(id+"F0.wireOp",EDGE,"6edb5fd7-54d7-42ad-92ee-4fd85836db77"),sQuery(id+"F0.wireOp",EDGE,"bc6cd693-f8fa-459a-9074-b617ec0104da"),sQuery(id+"F0.wireOp",EDGE,"132fc3af-a9a2-4640-87b1-e560ac0033a1"),sQuery(id+"F0.wireOp",EDGE,"508947bb-8de4-4d64-b81e-b9e2ca31af85"),sQuery(id+"F0.wireOp",EDGE,"263ae8a8-90c7-498b-adf2-94af4d08f381"),sQuery(id+"F0.wireOp",EDGE,"3c3fdada-33fa-4300-959f-1652c7e04f6f"),sQuery(id+"F0.wireOp",EDGE,"5a2aeb15-d6ef-4279-a2f0-f14d4b96b63e"),sQuery(id+"F0.wireOp",EDGE,"148bec1a-b59e-4291-9602-0e668bb3d098"),sQuery(id+"F0.wireOp",EDGE,"a1b19cf1-cf94-4a44-bc22-0c00d1b35e40"),sQuery(id+"F0.wireOp",EDGE,"b99aee4d-3f0d-48ee-b4ff-0ebc7f0d6d8a"),sQuery(id+"F0.wireOp",EDGE,"ecf27dbc-66c4-407c-8919-6ccf24f790f3"),sQuery(id+"F0.wireOp",EDGE,"84cf82ef-edac-41b9-a85a-52613d906b4f"),sQuery(id+"F0.wireOp",EDGE,"6f9bf3da-cc22-4046-8398-726881e65be8"),sQuery(id+"F0.wireOp",EDGE,"2cd02f45-4707-4b19-8dd1-68e3a048a7ed"),sQuery(id+"F0.wireOp",EDGE,"37396fa6-3296-48a8-b41d-f09d90a4feb7"),sQuery(id+"F0.wireOp",EDGE,"16ba9f7e-b05a-42c2-9539-ea36d1e6b86a"),sQuery(id+"F0.wireOp",EDGE,"d231a9ad-2026-44ee-a8e7-0275c1f8ec7d"),sQuery(id+"F0.wireOp",EDGE,"9f2dcf6f-a8de-437f-87c6-6b6e7ba86ed4"),sQuery(id+"F0.wireOp",EDGE,"52981f33-067a-4c2c-8828-b65ca661ad9c"),sQuery(id+"F0.wireOp",EDGE,"408cb5d9-231a-45ac-9bc4-41ac58c850e2"),sQuery(id+"F0.wireOp",EDGE,"9c21c1e0-d1b5-48d7-abac-f7b2b27de3de"),sQuery(id+"F0.wireOp",EDGE,"ffec0fd8-18a6-48fd-bf9a-7957bed396b8"),sQuery(id+"F0.wireOp",EDGE,"d5f5b610-cce5-4a58-adbd-be45ea3871aa"),sQuery(id+"F0.wireOp",EDGE,"eabe1d8d-9ed9-49f3-89ee-a4827284ac98"),sQuery(id+"F0.wireOp",EDGE,"cbc9e552-14e3-4b93-ae99-33b61fc300db"),sQuery(id+"F0.wireOp",EDGE,"30ecbc7d-613a-4bcc-817d-513a33f7f0e3"),sQuery(id+"F0.wireOp",EDGE,"18e8bb2b-b683-494f-a511-82aaf8420edb"),sQuery(id+"F0.wireOp",EDGE,"ddafc5e0-30d6-40e1-81d6-725c5972dba5"),sQuery(id+"F0.wireOp",EDGE,"fa8f1ce2-166e-48cb-afe0-128b0491fb0b"),sQuery(id+"F0.wireOp",EDGE,"1407d160-d278-4643-89c7-3521a8615b1f"),sQuery(id+"F0.wireOp",EDGE,"596a3357-e609-4669-af30-35b89a1584c6"),sQuery(id+"F0.wireOp",EDGE,"aaa4bf7b-662e-4ef3-a93a-3e9ffd297c4a"),sQuery(id+"F0.wireOp",EDGE,"9e65a868-0fb0-4d7e-9214-2ab33384a621"),sQuery(id+"F0.wireOp",EDGE,"8d5e906f-d52c-4eb1-9858-520727ad48c6"),sQuery(id+"F0.wireOp",EDGE,"cdc1a19b-cab9-41d1-a0a0-ce410699439c"),sQuery(id+"F0.wireOp",EDGE,"9b914fc0-16d4-47ca-8d9b-6efdd6fab2a3"),sQuery(id+"F0.wireOp",EDGE,"6e8fda0c-ef1d-458d-97ad-7745eaae0de2"),sQuery(id+"F0.wireOp",EDGE,"9db401f3-bab6-4f9c-a4f5-060f44c71ed1"),sQuery(id+"F0.wireOp",EDGE,"64e30ee5-41fe-43f3-8d91-b5800c139c95"),sQuery(id+"F0.wireOp",EDGE,"ec9cbeda-cb19-48ba-8dad-ec7cb6960f07"),sQuery(id+"F0.wireOp",EDGE,"92b309bb-47f7-4e8d-b569-b5f4bacc4261"),sQuery(id+"F0.wireOp",EDGE,"ef0f9529-8913-4cc2-bdb9-173a1dcbd115"),sQuery(id+"F0.wireOp",EDGE,"a2642eba-f641-4a26-a32b-bfcfb862dfa9"),sQuery(id+"F0.wireOp",EDGE,"8fec02c0-0363-4921-b789-f8c7a246b991"),sQuery(id+"F0.wireOp",EDGE,"b7c46eba-08fe-43a1-849b-bd1cca90a192"),sQuery(id+"F0.wireOp",EDGE,"6404b644-1840-45f7-8d0c-8accd017dd66"),sQuery(id+"F0.wireOp",EDGE,"93b70d59-cc48-402b-abd9-8d28f111c5ae"),sQuery(id+"F0.wireOp",EDGE,"0165fdec-1e62-4ad5-b3bc-38bb427360d7"),sQuery(id+"F0.wireOp",EDGE,"dccbc5c7-b9c2-4a71-bee8-2d60517ef9bd"),sQuery(id+"F0.wireOp",EDGE,"11e15b41-16a7-466e-96b0-076cef006174"),sQuery(id+"F0.wireOp",EDGE,"32dd4082-3509-4317-b6b9-6983ee8b7eff"),sQuery(id+"F0.wireOp",EDGE,"d55de4be-f282-485c-8cc2-362e4dcf16e6"),sQuery(id+"F0.wireOp",EDGE,"066d381d-f4a1-483b-8420-2492fa9c0dee"),sQuery(id+"F0.wireOp",EDGE,"5973b24d-27e9-4c40-b27f-8a40e30e9e32"),sQuery(id+"F0.wireOp",EDGE,"dd5682a7-0c74-4785-b55a-80176aa887f3"),sQuery(id+"F0.wireOp",EDGE,"8970e274-b150-45a8-bd0e-b3dda6f19f5b"),sQuery(id+"F0.wireOp",EDGE,"1a6e99f7-6c19-4570-8469-593ea103196b"),sQuery(id+"F0.wireOp",EDGE,"fb2402fe-453c-4e08-a8d0-2d908824c35c"),sQuery(id+"F0.wireOp",EDGE,"f908f7fd-2308-4a7d-b3b0-0a0b636c3764"),sQuery(id+"F0.wireOp",EDGE,"013f7eed-213f-4062-b37a-07f860009d78"),sQuery(id+"F0.wireOp",EDGE,"4a9e8910-ab63-4e98-8661-fd4f87db198f"),sQuery(id+"F0.wireOp",EDGE,"24a2a741-2185-4e06-9c02-27ec9086295c"),sQuery(id+"F0.wireOp",EDGE,"6835a710-b641-496c-bb60-bce9f4523c9e"),sQuery(id+"F0.wireOp",EDGE,"cdcfba0a-b4bd-403d-b96b-7301683a2622"),sQuery(id+"F0.wireOp",EDGE,"b9c45430-50bb-4e9d-8b0c-94a2aa1b7db1"),sQuery(id+"F0.wireOp",EDGE,"3d92a9fd-ad5b-4e3d-a7d9-05251f90bfbf"),sQuery(id+"F0.wireOp",EDGE,"6bdf556d-bc69-48f3-abf7-2d4d15e80244"),sQuery(id+"F0.wireOp",EDGE,"53b29f34-d141-49cf-8ecb-5610867f1fe1"),sQuery(id+"F0.wireOp",EDGE,"19573c38-7ee5-4907-b512-03d4f02fe7fb"),sQuery(id+"F0.wireOp",EDGE,"faf7ae07-8462-4f63-8af4-a3e6b0a81886"),sQuery(id+"F0.wireOp",EDGE,"05abe8ee-4be5-42de-ac33-4a24a8ee80d9"),sQuery(id+"F0.wireOp",EDGE,"de4761e7-ba1c-4691-850e-ea6e348e24be"),sQuery(id+"F0.wireOp",EDGE,"dac8c1c3-0d12-4fbf-b8ed-c2276810aec3"),sQuery(id+"F0.wireOp",EDGE,"3d50c741-c91f-4076-9353-8bc19711a71a"),sQuery(id+"F0.wireOp",EDGE,"dcb86853-e0ec-4ea4-8223-daa0ca295cb2"),sQuery(id+"F0.wireOp",EDGE,"4860a458-28ee-4d85-b6b2-514179390969"),sQuery(id+"F0.wireOp",EDGE,"863a4de6-e62c-4218-b5f0-2dd120242739"),sQuery(id+"F0.wireOp",EDGE,"1a4824a5-aa08-4c33-a72a-700e6606d007"),sQuery(id+"F0.wireOp",EDGE,"7da0cf67-c0e7-4bf9-b176-b73716ecd21e"),sQuery(id+"F0.wireOp",EDGE,"aee0c4cd-c753-4a05-b9bc-a1b32bcff9ab"),sQuery(id+"F0.wireOp",EDGE,"2b34d226-a438-4445-a074-3bbff589a12c"),sQuery(id+"F0.wireOp",EDGE,"ebb1c9a2-ae9c-45bc-8668-3fca7c21c9f8"),sQuery(id+"F0.wireOp",EDGE,"01c04197-1e48-4140-af38-0e1c6338c7cd"),sQuery(id+"F0.wireOp",EDGE,"49f0dd93-1389-4d00-81c6-36f6d01e0acc"),sQuery(id+"F0.wireOp",EDGE,"b4d31c4c-d272-4c9f-bae1-896e32a638b9"),sQuery(id+"F0.wireOp",EDGE,"0871fd1b-e3df-428e-9adf-ca3fcc696a25"),sQuery(id+"F0.wireOp",EDGE,"902e6c5c-9be4-49d6-99a8-803def05f00e"),sQuery(id+"F0.wireOp",EDGE,"03598667-7d25-4f0b-a50b-539104a50732"),sQuery(id+"F0.wireOp",EDGE,"190856f5-b755-44da-860d-ca5b4252228c"),sQuery(id+"F0.wireOp",EDGE,"6a1a2d63-a907-40fc-8bf7-ba97b39d8e7b"),sQuery(id+"F0.wireOp",EDGE,"fd5f3a51-52b9-4138-bb86-8b6a4700a89f"),sQuery(id+"F0.wireOp",EDGE,"2a3701fa-a3c5-4d80-b8ea-44c45627bcf0"),sQuery(id+"F0.wireOp",EDGE,"fa5d5fc2-ae96-4ab6-9e49-0351f26fc7b6"),sQuery(id+"F0.wireOp",EDGE,"e7ee2680-a35a-4d00-a959-63c1e9090b4c"),sQuery(id+"F0.wireOp",EDGE,"56cd987c-73de-43c7-b7e7-9d145fbb61d1"),sQuery(id+"F0.wireOp",EDGE,"5007d5d5-27f6-4491-896c-7dbb7ec46efb"),sQuery(id+"F0.wireOp",EDGE,"e190d2b4-efe9-4e46-acb6-eea77c7750eb"),sQuery(id+"F0.wireOp",EDGE,"479cbb70-0ac4-4098-9652-b2a87cac6553"),sQuery(id+"F0.wireOp",EDGE,"57c44ddd-76f8-49e1-83e0-e39e14421621"),sQuery(id+"F0.wireOp",EDGE,"b611a3f5-8dbc-4886-947f-fcd555503140"),sQuery(id+"F0.wireOp",EDGE,"06da85e9-838a-4f38-83cb-3d4113e69b32"),sQuery(id+"F0.wireOp",EDGE,"106c5fd0-f510-44a4-89f0-21162d4a1c0a"),sQuery(id+"F0.wireOp",EDGE,"5b6c80ac-1378-4d9a-af25-24f0d3f4cbac"),sQuery(id+"F0.wireOp",EDGE,"48948ce6-4ff7-4bbf-a070-428be44556bf"),sQuery(id+"F0.wireOp",EDGE,"ec884fcc-42de-4706-833d-90be3815d586"),sQuery(id+"F0.wireOp",EDGE,"81c4cbd6-e2ef-45cc-8291-ebd9ec264de1"),sQuery(id+"F0.wireOp",EDGE,"b2180cd8-9f8d-40fc-809e-6f038e9e6d7f"),sQuery(id+"F0.wireOp",EDGE,"b95729eb-fd2a-49de-b7c5-2099ac2c1fe1"),sQuery(id+"F0.wireOp",EDGE,"f341f5ef-ef4b-44d2-bbf0-2e3f0e31eab8"),sQuery(id+"F0.wireOp",EDGE,"a47b10b5-172f-4576-b746-98cc0bd9115f"),sQuery(id+"F0.wireOp",EDGE,"bdeb045e-e9e6-4f3d-bf3c-57d47329860d"),sQuery(id+"F0.wireOp",EDGE,"f97a3218-2a13-49ba-ad6f-89afafa004a2"),sQuery(id+"F0.wireOp",EDGE,"619c096f-86a8-4dfb-9653-5fd9eecd998a"),sQuery(id+"F0.wireOp",EDGE,"d0f89b8e-6007-4e81-9aee-9f3ad6569f13"),sQuery(id+"F0.wireOp",EDGE,"6790b9e0-7c1e-4f57-844e-70dc42300314"),sQuery(id+"F0.wireOp",EDGE,"cc83a62f-1fd4-47dd-8c3c-e763de5b27c2"),sQuery(id+"F0.wireOp",EDGE,"a35115cf-91f0-444a-90e6-3ff1a4b93f76"),sQuery(id+"F0.wireOp",EDGE,"1ddb8f84-f822-43b7-adaf-1f05a94ccb75"),sQuery(id+"F0.wireOp",EDGE,"47a3c889-4339-44a4-a945-e61c64b84eb7"),sQuery(id+"F0.wireOp",EDGE,"2af5b045-2a63-4e5f-ba14-8b5f69cc8cba"),sQuery(id+"F0.wireOp",EDGE,"f9e1c701-329e-48c4-b27f-765083167c74"),sQuery(id+"F0.wireOp",EDGE,"19618c68-4d1d-4cf7-91ca-0bdcb9d0fbf0"),sQuery(id+"F0.wireOp",EDGE,"23edb927-c75a-46ac-92eb-00791728a506"),sQuery(id+"F0.wireOp",EDGE,"2a8ff039-eef2-413c-a668-2a859320d89f"),sQuery(id+"F0.wireOp",EDGE,"fad287d6-2bb9-4622-accd-3ba0246237f3"),sQuery(id+"F0.wireOp",EDGE,"2cb2ba93-be74-46d4-88c6-69e04584695c"),sQuery(id+"F0.wireOp",EDGE,"5064c32e-df9e-488d-a9ad-9732fbd11f64"),sQuery(id+"F0.wireOp",EDGE,"1b72502b-0aad-4e50-9227-89f6630dab28"),sQuery(id+"F0.wireOp",EDGE,"5cb1ae26-d3e4-4358-87d9-602ca285b8bd"),sQuery(id+"F0.wireOp",EDGE,"7c32ab9f-19a5-4b67-a7f8-a0daddc378c4"),sQuery(id+"F0.wireOp",EDGE,"73296e7b-a954-4a39-99af-19c76bc3b81d"),sQuery(id+"F0.wireOp",EDGE,"64fbcc9c-0e51-43d4-8dc1-84c2bb7acfa4"),sQuery(id+"F0.wireOp",EDGE,"5e196178-a669-4fbb-b5b8-b5765a895a2f"),sQuery(id+"F0.wireOp",EDGE,"bab93f60-94f4-475b-a2a8-85b7d3f98929"),sQuery(id+"F0.wireOp",EDGE,"04e6edd2-5439-4c3a-8322-9073194e9b57"),sQuery(id+"F0.wireOp",EDGE,"5af41a84-4c87-4b43-9ddd-e31fddf844f1"),sQuery(id+"F0.wireOp",EDGE,"b8f01260-ba5f-4297-a4e8-81b4a7f9b968"),sQuery(id+"F0.wireOp",EDGE,"8f55b24c-2efe-498a-986b-860bc9d6cd62"),sQuery(id+"F0.wireOp",EDGE,"2c8e42cc-6f60-4f6a-be4c-85decde6bf3f"),sQuery(id+"F0.wireOp",EDGE,"70a84c8a-e315-4ed8-9662-987b4c45fff3"),sQuery(id+"F0.wireOp",EDGE,"220e9e1f-b452-49f1-a8c2-dc11710d8829"),sQuery(id+"F0.wireOp",EDGE,"9f378ead-aa27-47e6-8c62-cde23577b32d"),sQuery(id+"F0.wireOp",EDGE,"68de62c7-b686-45e9-9d1e-9fa7e5bc618e"),sQuery(id+"F0.wireOp",EDGE,"f2014a56-10f8-44ca-bf32-e221ee8ad32c"),sQuery(id+"F0.wireOp",EDGE,"cf6c1533-56d7-40ce-b47d-dd6e8e09b61c"),sQuery(id+"F0.wireOp",EDGE,"c721f733-9a75-4826-9c17-0644a6e1c414"),sQuery(id+"F0.wireOp",EDGE,"368b4ca7-e84b-4f92-981b-463213aeef25"),sQuery(id+"F0.wireOp",EDGE,"1c890408-7fd5-4f80-a989-c0cac3289d88"),sQuery(id+"F0.wireOp",EDGE,"d25b4a45-5b30-4ccf-9de1-d661d6489a37"),sQuery(id+"F0.wireOp",EDGE,"a107cb7b-62f0-4eb4-bf4d-3ed1c2a4ff78"),sQuery(id+"F0.wireOp",EDGE,"e5de749d-678c-46ca-b855-3fe615f08225"),sQuery(id+"F0.wireOp",EDGE,"2957ea33-4171-4f00-91c2-95ccdc445836"),sQuery(id+"F0.wireOp",EDGE,"83730173-db89-47a2-bcfc-1532d87d5f36"),sQuery(id+"F0.wireOp",EDGE,"56082139-6c9e-4a8e-8e40-eaf54a4f1120"),sQuery(id+"F0.wireOp",EDGE,"ea7689ac-adf6-457e-8852-03326ef56f7a"),sQuery(id+"F0.wireOp",EDGE,"5fb9af14-7811-4668-ac88-c56c07112ad6"),sQuery(id+"F0.wireOp",EDGE,"527925de-cf95-42d0-bb4d-5594059b2ff4"),sQuery(id+"F0.wireOp",EDGE,"74f4b52b-eebe-4d7b-b208-5bcd777e5ec2"),sQuery(id+"F0.wireOp",EDGE,"66314b9e-1996-4563-9226-e5e3be6b3aed"),sQuery(id+"F0.wireOp",EDGE,"1ead1fcb-a463-4bab-9d32-397705594f24"),sQuery(id+"F0.wireOp",EDGE,"613ce62b-f68f-4c15-a27c-9b50a5fa2a00"),sQuery(id+"F0.wireOp",EDGE,"a8c22376-5072-4371-b465-9ad4376e86dc"),sQuery(id+"F0.wireOp",EDGE,"08ef1cda-83df-40e6-84e5-941aed97a636"),sQuery(id+"F0.wireOp",EDGE,"251eacbe-8c6e-42fe-a1e3-71854ba044cf"),sQuery(id+"F0.wireOp",EDGE,"1dcf136b-b80e-497e-98d9-22fde25308dd"),sQuery(id+"F0.wireOp",EDGE,"4150e4c4-13a6-443e-92dc-7a9371a1877a"),sQuery(id+"F0.wireOp",EDGE,"29b06639-b109-4d70-9f8e-288401b0f229"),sQuery(id+"F0.wireOp",EDGE,"48c1294c-14a0-4b8b-9ad7-77ebedf7ee54"),sQuery(id+"F0.wireOp",EDGE,"25d626b8-3abd-43ef-9732-81caddf6bd82"),sQuery(id+"F0.wireOp",EDGE,"275b94ba-070b-4ead-a560-9e8b6b5bf311"),sQuery(id+"F0.wireOp",EDGE,"2933ded0-0d17-4d1d-846c-eeafafe6ccef"),sQuery(id+"F0.wireOp",EDGE,"5618fc39-da46-4527-93dd-0cc252efd7f7"),sQuery(id+"F0.wireOp",EDGE,"e13ba41f-e87c-4875-92d6-6a6be78c2523"),sQuery(id+"F0.wireOp",EDGE,"8c56cf67-9d34-4a0c-ab5b-c2c227bdd369"),sQuery(id+"F0.wireOp",EDGE,"29bf8a71-d6e7-4392-9fc8-749ee2964058"),sQuery(id+"F0.wireOp",EDGE,"b207ba18-1668-4809-ab9b-46f572db75c3"),sQuery(id+"F0.wireOp",EDGE,"16964af4-acd1-46d3-8050-b6c3ecf75b83"),sQuery(id+"F0.wireOp",EDGE,"6ecc3c55-6353-496e-acb4-d7247a16f50a"),sQuery(id+"F0.wireOp",EDGE,"6070db21-0c69-4749-b50e-18b8beab8b46"),sQuery(id+"F0.wireOp",EDGE,"c83d7944-b2e9-4616-958f-c815d7cbbe68"),sQuery(id+"F0.wireOp",EDGE,"5641a79a-c677-425c-b636-e1455cd0c030"),sQuery(id+"F0.wireOp",EDGE,"a5c13a0f-1164-448d-b50c-e6a205f75f86"),sQuery(id+"F0.wireOp",EDGE,"c35948c1-1d81-4a9d-9036-f8655d5d768b"),sQuery(id+"F0.wireOp",EDGE,"2c78cc5c-248a-4f40-af22-8a480499544e"),sQuery(id+"F0.wireOp",EDGE,"4c9af1d3-321e-43b7-8815-0e0836b24b58"),sQuery(id+"F0.wireOp",EDGE,"e9b215d5-5831-44a5-b760-fff7739d57ad"),sQuery(id+"F0.wireOp",EDGE,"2ba6f365-018e-40d0-9632-bde13f701955"),sQuery(id+"F0.wireOp",EDGE,"1d7c8e9c-567f-4ad6-a6e3-a809e78dc5fb"),sQuery(id+"F0.wireOp",EDGE,"72b6ff33-1d1d-488f-9fe8-152f75bf9776"),sQuery(id+"F0.wireOp",EDGE,"3ba2185f-48b3-4960-a53b-45459a3187af"),sQuery(id+"F0.wireOp",EDGE,"16b304db-3aab-46db-bd7c-6038e2d06a36"),sQuery(id+"F0.wireOp",EDGE,"f7b2b68c-f7c3-4f20-a51a-22e466f0231b"),sQuery(id+"F0.wireOp",EDGE,"991967c3-0b82-4b0e-bb55-12cab17636d5"),sQuery(id+"F0.wireOp",EDGE,"3576d61e-5b5e-4531-a86a-f9efaca913da"),sQuery(id+"F0.wireOp",EDGE,"c02db23e-b5ca-470f-ac65-69292ecf0cff"),sQuery(id+"F0.wireOp",EDGE,"eacbd2d9-2ed9-488f-944f-e8b7c3f78b3e"),sQuery(id+"F0.wireOp",EDGE,"1d0faf6c-a6d6-4096-9695-70604f8bad30"),sQuery(id+"F0.wireOp",EDGE,"ed5fb044-77ce-4ebb-a972-410f85b43bcb"),sQuery(id+"F0.wireOp",EDGE,"4df1c09a-3ffe-4816-8055-92edefc8a979"),sQuery(id+"F0.wireOp",EDGE,"5d4f7706-194f-48db-b873-a9f4989af888"),sQuery(id+"F0.wireOp",EDGE,"55cfc2c3-1ea2-49ca-93eb-e17f8b718343"),sQuery(id+"F0.wireOp",EDGE,"809a955d-ec6b-4ae8-a64a-96d2fa6f5298"),sQuery(id+"F0.wireOp",EDGE,"21cef66d-b80c-47da-a2dc-bc4cce8c7499"),sQuery(id+"F0.wireOp",EDGE,"bad0dfcd-52b2-4523-8167-51d2fa12cfee"),sQuery(id+"F0.wireOp",EDGE,"1e851b01-f015-45ca-a3bd-944fed59f9bd"),sQuery(id+"F0.wireOp",EDGE,"288ed6a4-c1e4-47b9-a233-7a95a7e455dc"),sQuery(id+"F0.wireOp",EDGE,"1eebe39a-53b4-499d-808d-a6975eb08b26"),sQuery(id+"F0.wireOp",EDGE,"1f64f298-b624-4d5f-93d8-653285cd1a5a"),sQuery(id+"F0.wireOp",EDGE,"7e1dfb90-5d4b-4035-8835-30a716cddff3"),sQuery(id+"F0.wireOp",EDGE,"a88f835b-43e7-4252-bb37-98e18cc451d9"),sQuery(id+"F0.wireOp",EDGE,"16d0170e-8391-4c54-84ce-0bbb9f535a07"),sQuery(id+"F0.wireOp",EDGE,"0879a2e5-c5f1-4117-9092-0e5e50c9141c"),sQuery(id+"F0.wireOp",EDGE,"05dcddf3-43ff-413f-b239-01f8f0f300ab"),sQuery(id+"F0.wireOp",EDGE,"04fccccf-0270-4038-a351-b721053f8429"),sQuery(id+"F0.wireOp",EDGE,"4faae2fc-fc27-4668-9f74-9cd9bee7b172"),sQuery(id+"F0.wireOp",EDGE,"05ca1c94-fa00-481d-a8e0-5a3ef8eaeacd"),sQuery(id+"F0.wireOp",EDGE,"d51a453d-3a9e-4675-93a8-59a99ec92bf4"),sQuery(id+"F0.wireOp",EDGE,"378b3c31-047d-46fb-b3a7-ac4ac1ba39b5"),sQuery(id+"F0.wireOp",EDGE,"82995fb6-bbff-4e37-9fca-e1cbc1db7ea8"),sQuery(id+"F0.wireOp",EDGE,"67563e4a-9b15-4152-867c-7c0e0df2a8c6"),sQuery(id+"F0.wireOp",EDGE,"6762e91b-83ed-4cbd-b532-a9b9ac7daf3f"),sQuery(id+"F0.wireOp",EDGE,"d3d51cab-dd0d-481e-b13f-520640a59d9e"),sQuery(id+"F0.wireOp",EDGE,"1ec3cf08-34fd-4720-93de-f84705f1b800"),sQuery(id+"F0.wireOp",EDGE,"37f301b2-37a0-4fdd-b58f-006c0550b2d5"),sQuery(id+"F0.wireOp",EDGE,"e19d5450-bd9a-4681-8df2-b78e537cea7e"),sQuery(id+"F0.wireOp",EDGE,"496c4abb-7432-4992-9ecb-fd8fb5807a96"),sQuery(id+"F0.wireOp",EDGE,"94930b1e-be43-476e-bbb5-0f71a74e4c82"),sQuery(id+"F0.wireOp",EDGE,"29bdb6a1-db5c-4b2f-a601-b8748da45dd4"),sQuery(id+"F0.wireOp",EDGE,"fdb63760-3eaf-4dbc-bb96-0ec81feeabb3"),sQuery(id+"F0.wireOp",EDGE,"6abc993b-5d6f-41e0-9d30-613df7748e2c"),sQuery(id+"F0.wireOp",EDGE,"cf51ced2-33cc-433d-a8e3-0a8e6ab4633e"),sQuery(id+"F0.wireOp",EDGE,"bd2df422-7c8b-4672-a167-a1e070c14377"),sQuery(id+"F0.wireOp",EDGE,"ac9b7676-6196-4fe7-8dc0-8b4c7f19035d"),sQuery(id+"F0.wireOp",EDGE,"0412b906-dab3-4683-8589-cecdf6cf9c8a"),sQuery(id+"F0.wireOp",EDGE,"6537b941-1335-4505-8017-8627c3c043be"),sQuery(id+"F0.wireOp",EDGE,"5f1e7276-0115-45c7-82e5-f330e3c2fb74"),sQuery(id+"F0.wireOp",EDGE,"a4489bfa-5ba1-44e6-b65f-7ed1139340bc"),sQuery(id+"F0.wireOp",EDGE,"23d198d4-9637-4b64-b350-3d9b97209b93"),sQuery(id+"F0.wireOp",EDGE,"42dc715e-67ce-47dd-bc7e-9565251bcfd0"),sQuery(id+"F0.wireOp",EDGE,"cd9e4183-7cc9-413d-bd94-20a9d3a74fc9"),sQuery(id+"F0.wireOp",EDGE,"03de00b4-bee8-4db3-8c6f-fbf8bb530c55"),sQuery(id+"F0.wireOp",EDGE,"8b2c66e1-2722-4951-8ff3-82a7355ef1c2"),sQuery(id+"F0.wireOp",EDGE,"7f58e016-16fa-4bda-becf-3a110b6b0ba8"),sQuery(id+"F0.wireOp",EDGE,"2e4b4eea-771e-44e1-a790-7858300a958c"),sQuery(id+"F0.wireOp",EDGE,"66edb572-61a0-458d-acb6-a9c38e7c9817"),sQuery(id+"F0.wireOp",EDGE,"ef92da9d-23fe-45d1-a911-75a33661f011"),sQuery(id+"F0.wireOp",EDGE,"5bfa7897-d6c6-48be-be5b-6def31250002"),sQuery(id+"F0.wireOp",EDGE,"8231bbcd-b2a9-4737-b60c-249983317a18"),sQuery(id+"F0.wireOp",EDGE,"fbc1c214-68d0-42ec-9c45-bee98f097555"),sQuery(id+"F0.wireOp",EDGE,"8a3a4b2a-3e59-4b07-8100-140c4c981be5"),sQuery(id+"F0.wireOp",EDGE,"7e709ee0-ea37-4f65-a946-660b1798bdf2"),sQuery(id+"F0.wireOp",EDGE,"500b1576-4e8a-47ef-af30-215078d273ce"),sQuery(id+"F0.wireOp",EDGE,"3c244ecb-d982-4908-a7af-12a24f38b454"),sQuery(id+"F0.wireOp",EDGE,"8de3b702-b5a6-42dc-b70a-b8532fbf20c6"),sQuery(id+"F0.wireOp",EDGE,"10e3de8a-fc30-4cff-9237-3e22bd9e3232"),sQuery(id+"F0.wireOp",EDGE,"b6f9acd2-4eee-4475-a5b4-9e1ce02e0f0a"),sQuery(id+"F0.wireOp",EDGE,"19d699ee-cbd7-4546-800e-109ea1046660"),sQuery(id+"F0.wireOp",EDGE,"8a712665-6dc5-4123-969b-d9c7bdb6eea8"),sQuery(id+"F0.wireOp",EDGE,"29c2415b-a683-44f6-9851-56f80d3d0f17"),sQuery(id+"F0.wireOp",EDGE,"fc8e5354-b49d-4e90-8587-4fad446cdc7a"),sQuery(id+"F0.wireOp",EDGE,"1d97e188-d88c-40ec-b67b-ebeadd9dbc9b"),sQuery(id+"F0.wireOp",EDGE,"83a5129d-c98b-4703-85cf-65f83663392a"),sQuery(id+"F0.wireOp",EDGE,"38459e7b-decf-425a-80e7-dd305edb38a6"),sQuery(id+"F0.wireOp",EDGE,"8a94d0ab-b270-411c-a6b1-3108556eeb98"),sQuery(id+"F0.wireOp",EDGE,"c00de532-d654-4b73-808b-7e7d03ecc37a"),sQuery(id+"F0.wireOp",EDGE,"9baffacd-999b-4c18-91c6-c5dda2931f50"),sQuery(id+"F0.wireOp",EDGE,"da6f64c5-5353-44d2-9fa2-6d1f2e632f35"),sQuery(id+"F0.wireOp",EDGE,"14e3b729-da8a-4127-8f21-d55b9a6fb4aa"),sQuery(id+"F0.wireOp",EDGE,"9df101d5-80ed-4980-8b55-10ecc94a02d8"),sQuery(id+"F0.wireOp",EDGE,"e638abd0-6801-4534-9919-44cde57cbd5b"),sQuery(id+"F0.wireOp",EDGE,"c0059b76-6e1b-4eaa-8415-b4e65df05b37"),sQuery(id+"F0.wireOp",EDGE,"c04777a8-102f-4856-b92a-2e358a58d09e"),sQuery(id+"F0.wireOp",EDGE,"9b06d21f-a5f0-48cc-8ba2-fa8c291e5086"),sQuery(id+"F0.wireOp",EDGE,"e7ee14ce-ee89-4084-aa7f-54b2d9003392"),sQuery(id+"F0.wireOp",EDGE,"8dc047b9-710b-48d6-adec-864b411053f1"),sQuery(id+"F0.wireOp",EDGE,"fb02d67f-8f5c-45fb-a3a7-b39d9548de9f"),sQuery(id+"F0.wireOp",EDGE,"3f1c47f8-75a6-4e30-ae12-d541cd37cc83"),sQuery(id+"F0.wireOp",EDGE,"ae22e717-8f71-49b8-9e39-3b406532921e"),sQuery(id+"F0.wireOp",EDGE,"22017561-5b3b-4ff9-b42c-8ec01e4276ca"),sQuery(id+"F0.wireOp",EDGE,"bed059a4-dd32-4a75-b05a-074b6281357f"),sQuery(id+"F0.wireOp",EDGE,"c0586c55-c3ea-4c35-a08c-15e696a43b99"),sQuery(id+"F0.wireOp",EDGE,"303c49fd-fa39-47ae-a902-4dccbb48fc6a"),sQuery(id+"F0.wireOp",EDGE,"fb68c198-0212-4bcb-bf57-08a5b7e91de6"),sQuery(id+"F0.wireOp",EDGE,"ee4d1f3c-998d-4543-9810-a37c8be260cc"),sQuery(id+"F0.wireOp",EDGE,"325099e8-ab89-4a35-a291-7fe3fc5821f3"),sQuery(id+"F0.wireOp",EDGE,"60f210ef-b77f-4b66-abb3-8deec2e0e0bb"),sQuery(id+"F0.wireOp",EDGE,"547cdca8-b857-4bb6-9f4f-58ef7bc8e838"),sQuery(id+"F0.wireOp",EDGE,"d16bc155-9374-4df2-b6f8-ff9b66236ed3"),sQuery(id+"F0.wireOp",EDGE,"9ef04104-79ef-4c74-9da8-eceb0cb3a4fe"),sQuery(id+"F0.wireOp",EDGE,"bcee84cf-422a-4575-87c7-1479d367d2cf"),sQuery(id+"F0.wireOp",EDGE,"b9c310c4-f7ad-4dbd-8673-34254f61f560"),sQuery(id+"F0.wireOp",EDGE,"497fc37e-f6f6-4b99-8b07-0360bc2a9d0e"),sQuery(id+"F0.wireOp",EDGE,"c10a195e-950b-4ef1-81a0-f20b35e1dadd"),sQuery(id+"F0.wireOp",EDGE,"ff1639dc-0830-432c-9654-0467c31231af"),sQuery(id+"F0.wireOp",EDGE,"23ad70da-acb1-4188-a4a8-c5af692e904a"),sQuery(id+"F0.wireOp",EDGE,"a8dd13a0-8968-46c5-acfa-195848781c1c"),sQuery(id+"F0.wireOp",EDGE,"8156b7ce-230b-48e1-aa1b-894d7316a82f"),sQuery(id+"F0.wireOp",EDGE,"b6facb5f-a5bd-40a4-9b11-e35c975b3f11"),sQuery(id+"F0.wireOp",EDGE,"07a15268-51ad-4d49-aca9-99fb6002e07d"),sQuery(id+"F0.wireOp",EDGE,"b56aef46-9202-4632-96a0-d00f2144ea35"),sQuery(id+"F0.wireOp",EDGE,"5439e26b-5952-4da8-bd75-4901e0e357cf"),sQuery(id+"F0.wireOp",EDGE,"127deab1-32e5-43cb-be08-b1c22e829773"),sQuery(id+"F0.wireOp",EDGE,"20ff72b7-5221-4f09-9edb-d3e930f05ba0"),sQuery(id+"F0.wireOp",EDGE,"1a24371d-c4cb-490c-97cd-55eedcdae095"),sQuery(id+"F0.wireOp",EDGE,"ea3ea07d-1b41-4802-b222-d96af10a48ef"),sQuery(id+"F0.wireOp",EDGE,"07ec1ecc-1a48-4fe7-b261-08e6caac05a2"),sQuery(id+"F0.wireOp",EDGE,"f6eee84f-0b84-41bf-92cd-571c99526fdb"),sQuery(id+"F0.wireOp",EDGE,"50106d84-7118-4f31-aab1-b25162fad229"),sQuery(id+"F0.wireOp",EDGE,"a8ec2e87-9788-4528-96c4-8cc6e6622ee4"),sQuery(id+"F0.wireOp",EDGE,"dd9bd91e-b22f-4125-8bc9-33acf8a34fb6"),sQuery(id+"F0.wireOp",EDGE,"23ceb77e-1dbe-4fb1-b360-71852dcd5f4f"),sQuery(id+"F0.wireOp",EDGE,"5971fce1-1edd-4e73-a59e-1bf903e028e7"),sQuery(id+"F0.wireOp",EDGE,"07e886e8-8b31-45f3-bf7e-5377ab8aaa6c"),sQuery(id+"F0.wireOp",EDGE,"b02181cd-1141-4195-931e-27cd5f67d936"),sQuery(id+"F0.wireOp",EDGE,"f404ba3d-95fe-497c-b900-a3e38243fd2c"),sQuery(id+"F0.wireOp",EDGE,"a724a2a2-e5d7-4f6e-b09d-3cee00442056"),sQuery(id+"F0.wireOp",EDGE,"826c2464-77cb-4336-9c5d-7eb6201290fe"),sQuery(id+"F0.wireOp",EDGE,"09e1373d-1870-49ef-8ab9-8036af7e093e"),sQuery(id+"F0.wireOp",EDGE,"14ebac5c-4536-4251-81bc-087c3384b32f"),sQuery(id+"F0.wireOp",EDGE,"bd8efbcf-97c7-41e9-8274-be8eab9fb382"),sQuery(id+"F0.wireOp",EDGE,"3e574c1f-8cdc-4690-b463-ff136dfcd360"),sQuery(id+"F0.wireOp",EDGE,"e4056e94-2d8a-4956-9234-2c9a5943a90a"),sQuery(id+"F0.wireOp",EDGE,"86da7161-c18f-49d9-93c7-1a22064837e4"),sQuery(id+"F0.wireOp",EDGE,"622f2018-0628-406c-9b5b-8f0f21c4a4dc"),sQuery(id+"F0.wireOp",EDGE,"0b9b8fe2-6d5f-4fa9-b0a1-efe2fda969b1"),sQuery(id+"F0.wireOp",EDGE,"5ef0ff38-6ebe-48cf-9e3e-1cfc3091928c"),sQuery(id+"F0.wireOp",EDGE,"78e54c78-bf96-4352-a758-ba91713fc725"),sQuery(id+"F0.wireOp",EDGE,"8e88edc4-cb30-4baf-968f-ebfe73424514"),sQuery(id+"F0.wireOp",EDGE,"8965327c-dd52-40d3-bf32-6a3949e96a9b"),sQuery(id+"F0.wireOp",EDGE,"8d87fff9-b896-4c97-bd6d-f2766d30679d"),sQuery(id+"F0.wireOp",EDGE,"89866aad-1e9a-4de7-a745-e64d56412f35"),sQuery(id+"F0.wireOp",EDGE,"905ac5f9-c21d-412c-8d54-d50402b60c54"),sQuery(id+"F0.wireOp",EDGE,"467ab422-03aa-417e-b913-b5e80ddb0c79"),sQuery(id+"F0.wireOp",EDGE,"58dbdb81-e612-40fb-95c5-ab7bf1a3d2de"),sQuery(id+"F0.wireOp",EDGE,"984d3f0b-13f2-487f-b755-4a0bba7058a4"),sQuery(id+"F0.wireOp",EDGE,"0a03f4d7-e756-4fd7-b006-fca0c5a48bca"),sQuery(id+"F0.wireOp",EDGE,"101bfc79-94c6-4c89-aecc-1a2471e45639"),sQuery(id+"F0.wireOp",EDGE,"bafda8bc-ec10-4e44-93de-7f3a36b19821"),sQuery(id+"F0.wireOp",EDGE,"057079dd-d07b-477b-8ded-5477aa495cb4"),sQuery(id+"F0.wireOp",EDGE,"1fb1e1a4-6633-473d-9e7c-d715702e041d"),sQuery(id+"F0.wireOp",EDGE,"06677649-1231-4f91-92a7-bae0b2f99e4e"),sQuery(id+"F0.wireOp",EDGE,"c673a0ec-5590-423f-b00a-c47544d5ce3e"),sQuery(id+"F0.wireOp",EDGE,"35866d11-f724-410c-99f3-ef9d173eaa3e"),sQuery(id+"F0.wireOp",EDGE,"50ebca05-b06f-4a84-9183-6c9ef9454d81"),sQuery(id+"F0.wireOp",EDGE,"02ccba90-f602-4031-b836-1d7658534b58"),sQuery(id+"F0.wireOp",EDGE,"d477b567-8937-45cc-afcc-cc7fd9d94498"),sQuery(id+"F0.wireOp",EDGE,"e7b6ada3-6ca2-4ffc-9d90-25d2595f40ac"),sQuery(id+"F0.wireOp",EDGE,"9892b1b2-e034-4a0d-a43c-ad3cfea8fe83"),sQuery(id+"F0.wireOp",EDGE,"7eb55d43-f956-4008-80c8-b4ab5805bcb7"),sQuery(id+"F0.wireOp",EDGE,"59a98bf0-71ee-4f28-abec-2204bb7d477a"),sQuery(id+"F0.wireOp",EDGE,"a879b169-3dcc-40eb-8ff6-a461203dd6dd"),sQuery(id+"F0.wireOp",EDGE,"fde519b3-a6ef-4a7d-aef6-996c976b111e"),sQuery(id+"F0.wireOp",EDGE,"1ae5a593-5d85-4dc8-86f0-c812bc5b5aba"),sQuery(id+"F0.wireOp",EDGE,"914f2caf-3d6b-4c35-ba92-f6993b2fbc88"),sQuery(id+"F0.wireOp",EDGE,"0f978844-0975-4ef8-8208-a486fd79bb82"),sQuery(id+"F0.wireOp",EDGE,"5a25cdce-64f0-4099-80ce-602216827c90"),sQuery(id+"F0.wireOp",EDGE,"d3bc9758-d3a8-4820-8c46-5f7e7d42b4e3"),sQuery(id+"F0.wireOp",EDGE,"17fd1400-0a30-4e68-a373-c4e5d2f26af7"),sQuery(id+"F0.wireOp",EDGE,"75660254-19bd-4f5f-a0a2-bcee4d00c499"),sQuery(id+"F0.wireOp",EDGE,"9e8646c9-e721-4e54-a392-2f54c8f7b81b"),sQuery(id+"F0.wireOp",EDGE,"9ab30725-9705-408f-a94e-ecf0a6bbe568"),sQuery(id+"F0.wireOp",EDGE,"308d3d82-aebc-4eb4-bfa0-cdf01e8c387e"),sQuery(id+"F0.wireOp",EDGE,"c0a0d6b5-ca63-4314-93ea-3eaaef76272b"),sQuery(id+"F0.wireOp",EDGE,"f757b01b-a185-4ce0-832d-5ad9c622d69f"),sQuery(id+"F0.wireOp",EDGE,"ab4fee9c-1f4b-4b8d-a66b-7a33e98ee4fa"),sQuery(id+"F0.wireOp",EDGE,"73d98c56-dcfc-443c-9903-d209168277be"),sQuery(id+"F0.wireOp",EDGE,"e73cdc64-0ab5-4634-a86d-ccacd0f9ba69"),sQuery(id+"F0.wireOp",EDGE,"a39e3194-2c4c-4f73-8f81-beee18b7d4fb"),sQuery(id+"F0.wireOp",EDGE,"2d2d454e-a145-4402-9430-90765ca3ef39"),sQuery(id+"F0.wireOp",EDGE,"9b395d58-f0b2-45b7-9d38-3ba5c381c6b3"),sQuery(id+"F0.wireOp",EDGE,"d6e9afce-2052-45c1-a3cd-bc5c770fcc30"),sQuery(id+"F0.wireOp",EDGE,"58005fae-83f3-48d1-a1f3-7d7777f9102a"),sQuery(id+"F0.wireOp",EDGE,"55503e77-bfe1-477f-b6fa-769a57791085"),sQuery(id+"F0.wireOp",EDGE,"e3dece3a-4bf9-41fe-b60e-19e8eb760ec8"),sQuery(id+"F0.wireOp",EDGE,"e225004e-7c7a-4b1a-9d9c-bd8d5587ed73"),sQuery(id+"F0.wireOp",EDGE,"cafc7d21-8e1d-4988-9c3d-06c1626d1c78"),sQuery(id+"F0.wireOp",EDGE,"ba598920-6e2e-4a75-bfbe-3ffb7267c3f5"),sQuery(id+"F0.wireOp",EDGE,"084abf44-e056-4a2d-a8fe-978bda86ebed"),sQuery(id+"F0.wireOp",EDGE,"17dad1b1-9393-4f55-915c-28a70ace4381"),sQuery(id+"F0.wireOp",EDGE,"cf9cfd1c-cf0f-46fc-97df-dc42e5e02bc1"),sQuery(id+"F0.wireOp",EDGE,"520eeedb-eaf4-49ce-9d4d-96e7e921b325"),sQuery(id+"F0.wireOp",EDGE,"3260c2d0-a2cf-4cdf-a4d5-f4cbabbaf893"),sQuery(id+"F0.wireOp",EDGE,"f982051d-3c11-4c54-829a-76b7c6ab8a72"),sQuery(id+"F0.wireOp",EDGE,"e1493711-f827-47d6-8ed1-1d269d3dc0ea"),sQuery(id+"F0.wireOp",EDGE,"da87f092-cb25-4d5d-91d0-7d91c7cbd832"),sQuery(id+"F0.wireOp",EDGE,"b42b8699-d04e-475a-819f-08834b8a2bf6"),sQuery(id+"F0.wireOp",EDGE,"db176a9b-6a75-4e8e-bdda-4bbc5e733d20"),sQuery(id+"F0.wireOp",EDGE,"c76bc4ed-5e99-4e89-92f0-be5fd1922589"),sQuery(id+"F0.wireOp",EDGE,"041b93a8-293a-47b3-8f3a-a8973a17d960"),sQuery(id+"F0.wireOp",EDGE,"ba561d6b-0882-440b-b78d-15d78bdf95ee"),sQuery(id+"F0.wireOp",EDGE,"ad989c4c-a779-4d37-9193-1c4c5a1f90d2"),sQuery(id+"F0.wireOp",EDGE,"ce10184d-55c2-488a-9e2b-e780ec6733b7"),sQuery(id+"F0.wireOp",EDGE,"92646d3e-ea16-4ce9-9b98-f3d2afacf624"),sQuery(id+"F0.wireOp",EDGE,"1fef100a-8b69-47c6-ad45-17a7e9016646"),sQuery(id+"F0.wireOp",EDGE,"a9abf371-aaae-4980-97c3-618588223727"),sQuery(id+"F0.wireOp",EDGE,"9c051174-52e1-4caa-a03b-b18f81b07894"),sQuery(id+"F0.wireOp",EDGE,"09011d5e-2227-49ee-8a4f-ca06ef3bf9c9"),sQuery(id+"F0.wireOp",EDGE,"61318397-4f19-4a74-8977-958978d30da7"),sQuery(id+"F0.wireOp",EDGE,"3dd6c7c8-d307-49b4-bd14-b574e65bdeda"),sQuery(id+"F0.wireOp",EDGE,"6d587b47-ad53-4508-8fc8-b49e35483090"),sQuery(id+"F0.wireOp",EDGE,"c7b96cc4-2c11-4c08-9bc1-964cc6eae071"),sQuery(id+"F0.wireOp",EDGE,"d368f493-27cc-4be4-929c-f14eaf5c93de"),sQuery(id+"F0.wireOp",EDGE,"a0ab345c-276c-4998-a397-334cc7dec3a7"),sQuery(id+"F0.wireOp",EDGE,"fda3a3b5-c850-4c64-9562-c1df2376066b")])]});
            var Q1;
            Q1=qCreatedBy(makeId("Origin.pointOp"),VERTEX);
            var Q2;
            Q2=qCreatedBy(makeId("Origin.pointOp"),VERTEX);
            transform(context, id + "F6", {"entities" : qUnion([Q0]), "transformType" : TransformType.SCALE_UNIFORMLY, "scale" : 54.18 / 60, "scalePoint" : qUnion([Q2]), "makeCopy" : false});
        }
    });
